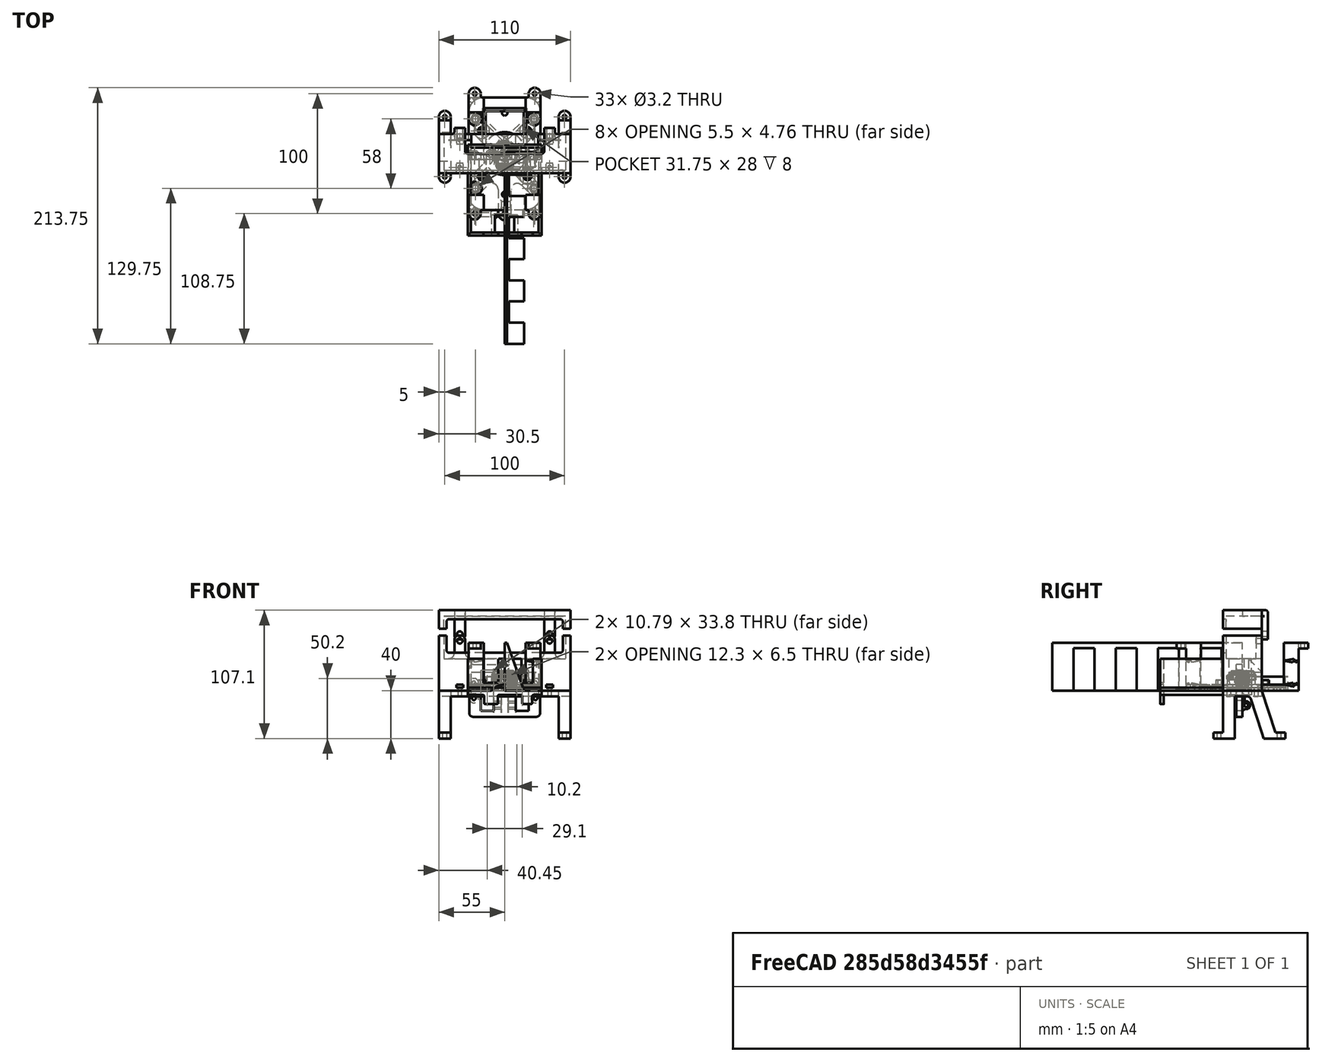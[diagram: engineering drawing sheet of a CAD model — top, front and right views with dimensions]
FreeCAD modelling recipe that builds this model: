
FCSTD DOCUMENT  (FreeCAD 1.0R39109 (Git))
Label: emaxx-kybernetes-mounts
License: All rights reserved
LicenseURL: http://en.wikipedia.org/wiki/All_rights_reserved
objects: Sketcher::SketchObject×61, PartDesign::Pad×32, PartDesign::Pocket×29, PartDesign::Fillet×29, PartDesign::Body×15, App::Part×15, Mesh::Feature×2, Spreadsheet::Sheet×1, PartDesign::SubtractivePrism×1, Part::Feature×1
note: 411 computed .brp shape members not serialized (recipe doc carries the construction recipe); baked Part::Feature solids carry a one-line shape summary decoded from their .brp

FEATURE [Sketcher::SketchObject] Sketch  label="ArduinoBoxOutlineSketch"
  ArcFitTolerance = 0
  AttachmentSupport = -> [XY_Plane001]
  FullyConstrained = true
  MakeInternals = false
  MapMode = 5
  expr: Constraints[0] = <<parameters>>.chassis_hole_diameter
  expr: Constraints[103] = <<parameters>>.margin + <<parameters>>.wall_depth + 0.25 mm
  expr: Constraints[114] = <<parameters>>.esc_width / 2 + <<parameters>>.wall_depth
  expr: Constraints[115] = <<parameters>>.esc_width / 2 + <<parameters>>.wall_depth
  expr: Constraints[121] = <<parameters>>.esc_height + <<parameters>>.wall_depth
  expr: Constraints[1] = <<parameters>>.chassis_hole_diameter
  expr: Constraints[2] = <<parameters>>.chassis_hole_spacing / 2
  expr: Constraints[4] = <<parameters>>.chassis_hole_spacing / 2
  expr: Constraints[5] = <<parameters>>.arduino_width / 2
  expr: Constraints[75] = <<parameters>>.arduino_hole1_offset_x
  expr: Constraints[77] = <<parameters>>.arduino_standoff_diameter
  expr: Constraints[78] = <<parameters>>.arduino_hole1_offset_y
  expr: Constraints[80] = <<parameters>>.arduino_standoff_diameter
  expr: Constraints[81] = <<parameters>>.arduino_standoff_diameter
  expr: Constraints[84] = <<parameters>>.arduino_standoff_diameter
  expr: Constraints[85] = <<parameters>>.arduino_hole3_offset_x
  expr: Constraints[86] = <<parameters>>.arduino_hole3_offset_y
  expr: Constraints[87] = <<parameters>>.arduino_hole4_offset_y
  expr: Constraints[88] = <<parameters>>.arduino_hole4_offset_x
  expr: Constraints[89] = <<parameters>>.arduino_hole2_offset_x
  expr: Constraints[90] = <<parameters>>.arduino_hole2_offset_y
  expr: Constraints[93] = <<parameters>>.arduino_length
  expr: Constraints[94] = <<parameters>>.wall_depth + <<parameters>>.margin + 1.75 mm
  expr: Constraints[96] = <<parameters>>.wall_depth + 5.75 mm / 2 + <<parameters>>.margin
  expr: Constraints[99] = <<parameters>>.wall_depth + 5.75 mm / 2 + <<parameters>>.margin
  sketch-geometry (43):
    g0: Circle CenterX=-25.25 CenterY=0 CenterZ=0 NormalX=0 NormalY=0 NormalZ=1 AngleXU=0 Radius=1.6
    g1: Circle CenterX=25.25 CenterY=0 CenterZ=0 NormalX=0 NormalY=0 NormalZ=1 AngleXU=0 Radius=1.6
    g2: GeomPoint [constr] X=26.67 Y=-65.54 Z=0
    g3: LineSegment StartX=26.88 StartY=-51.57 StartZ=0 EndX=25.505 EndY=-49.1884 EndZ=0
    g4: LineSegment StartX=25.505 StartY=-49.1884 StartZ=0 EndX=22.755 EndY=-49.1884 EndZ=0
    g5: LineSegment StartX=22.755 StartY=-49.1884 StartZ=0 EndX=21.38 EndY=-51.57 EndZ=0
    g6: LineSegment StartX=21.38 StartY=-51.57 StartZ=0 EndX=22.755 EndY=-53.9516 EndZ=0
    g7: LineSegment StartX=22.755 StartY=-53.9516 StartZ=0 EndX=25.505 EndY=-53.9516 EndZ=0
    g8: LineSegment StartX=25.505 StartY=-53.9516 StartZ=0 EndX=26.88 EndY=-51.57 EndZ=0
    g9: Circle [constr] CenterX=24.13 CenterY=-51.57 CenterZ=0 NormalX=0 NormalY=0 NormalZ=1 AngleXU=0 Radius=2.75
    g10: LineSegment StartX=-6.14 StartY=0.5 StartZ=0 EndX=-7.515 EndY=2.88157 EndZ=0
    g11: LineSegment StartX=-7.515 StartY=2.88157 StartZ=0 EndX=-10.265 EndY=2.88157 EndZ=0
    g12: LineSegment StartX=-10.265 StartY=2.88157 StartZ=0 EndX=-11.64 EndY=0.5 EndZ=0
    g13: LineSegment StartX=-11.64 StartY=0.5 StartZ=0 EndX=-10.265 EndY=-1.88157 EndZ=0
    g14: LineSegment StartX=-10.265 StartY=-1.88157 StartZ=0 EndX=-7.515 EndY=-1.88157 EndZ=0
    g15: LineSegment StartX=-7.515 StartY=-1.88157 StartZ=0 EndX=-6.14 EndY=0.5 EndZ=0
    g16: Circle [constr] CenterX=-8.89 CenterY=0.5 CenterZ=0 NormalX=0 NormalY=0 NormalZ=1 AngleXU=0 Radius=2.75
    g17: LineSegment StartX=20.425 StartY=-1.88157 StartZ=0 EndX=21.8 EndY=0.5 EndZ=0
    g18: LineSegment StartX=21.8 StartY=0.5 StartZ=0 EndX=20.425 EndY=2.88157 EndZ=0
    g19: LineSegment StartX=20.425 StartY=2.88157 StartZ=0 EndX=17.675 EndY=2.88157 EndZ=0
    g20: LineSegment StartX=17.675 StartY=2.88157 StartZ=0 EndX=16.3 EndY=0.5 EndZ=0
    g21: LineSegment StartX=16.3 StartY=0.5 StartZ=0 EndX=17.675 EndY=-1.88157 EndZ=0
    g22: LineSegment StartX=17.675 StartY=-1.88157 StartZ=0 EndX=20.425 EndY=-1.88157 EndZ=0
    g23: Circle [constr] CenterX=19.05 CenterY=0.5 CenterZ=0 NormalX=0 NormalY=0 NormalZ=1 AngleXU=0 Radius=2.75
    g24: LineSegment StartX=-22.755 StartY=-52.6816 StartZ=0 EndX=-21.38 EndY=-50.3 EndZ=0
    g25: LineSegment StartX=-21.38 StartY=-50.3 StartZ=0 EndX=-22.755 EndY=-47.9184 EndZ=0
    g26: LineSegment StartX=-22.755 StartY=-47.9184 StartZ=0 EndX=-25.505 EndY=-47.9184 EndZ=0
    g27: LineSegment StartX=-25.505 StartY=-47.9184 StartZ=0 EndX=-26.88 EndY=-50.3 EndZ=0
    g28: LineSegment StartX=-26.88 StartY=-50.3 StartZ=0 EndX=-25.505 EndY=-52.6816 EndZ=0
    g29: LineSegment StartX=-25.505 StartY=-52.6816 StartZ=0 EndX=-22.755 EndY=-52.6816 EndZ=0
    g30: Circle [constr] CenterX=-24.13 CenterY=-50.3 CenterZ=0 NormalX=0 NormalY=0 NormalZ=1 AngleXU=0 Radius=2.75
    g31: GeomPoint [constr] X=26.67 Y=3.04 Z=0
    g32: GeomPoint [constr] X=0 Y=7.49 Z=0
    g33: GeomPoint [constr] X=30.825 Y=0 Z=0
    g34: GeomPoint [constr] X=-30.825 Y=0 Z=0
    g35: LineSegment StartX=-30.825 StartY=-68.49 StartZ=0 EndX=30.825 EndY=-68.49 EndZ=0
    g36: LineSegment StartX=-30.825 StartY=7.49 StartZ=0 EndX=-30.825 EndY=-68.49 EndZ=0
    g37: LineSegment StartX=30.825 StartY=7.49 StartZ=0 EndX=30.825 EndY=-68.49 EndZ=0
    g38: LineSegment StartX=-30.825 StartY=7.49 StartZ=0 EndX=-18.375 EndY=7.49 EndZ=0
    g39: LineSegment StartX=30.825 StartY=7.49 StartZ=0 EndX=18.375 EndY=7.49 EndZ=0
    g40: LineSegment StartX=-18.375 StartY=7.49 StartZ=0 EndX=-18.375 EndY=37.99 EndZ=0
    g41: LineSegment StartX=18.375 StartY=7.49 StartZ=0 EndX=18.375 EndY=37.99 EndZ=0
    g42: LineSegment StartX=-18.375 StartY=37.99 StartZ=0 EndX=18.375 EndY=37.99 EndZ=0
  constraints (108):
    c: Diameter(g1) = 3.2
    c: Diameter(g0) = 3.2
    c: DistanceX(g-1,g1) = 25.25
    c: Horizontal(g0,g-1)
    c: DistanceX(g0,g-1) = 25.25
    c: DistanceX(g-1,g2) = 26.67
    c: Horizontal(g1,g0)
    c: Coincident(g3,g4)
    c: Coincident(g4,g5)
    c: Coincident(g5,g6)
    c: Coincident(g6,g7)
    c: Coincident(g7,g8)
    c: Coincident(g8,g3)
    c: Equal(g3, g4-g8) x5
    c: PointOnObject(g3,g9)
    c: PointOnObject(g4,g9)
    c: PointOnObject(g5,g9)
    c: PointOnObject(g6,g9)
    c: PointOnObject(g7,g9)
    c: PointOnObject(g8,g9)
    c: Coincident(g10,g11)
    c: Coincident(g11,g12)
    c: Coincident(g12,g13)
    c: Coincident(g13,g14)
    c: Coincident(g14,g15)
    c: Coincident(g15,g10)
    c: Equal(g10, g11-g15) x5
    c: PointOnObject(g10,g16)
    c: PointOnObject(g11,g16)
    c: PointOnObject(g12,g16)
    c: PointOnObject(g13,g16)
    c: PointOnObject(g14,g16)
    c: PointOnObject(g15,g16)
    c: Coincident(g17,g18)
    c: Coincident(g18,g19)
    c: Coincident(g19,g20)
    c: Coincident(g20,g21)
    c: Coincident(g21,g22)
    c: Coincident(g22,g17)
    c: Equal(g17, g18-g22) x5
    c: PointOnObject(g17,g23)
    c: PointOnObject(g18,g23)
    c: PointOnObject(g19,g23)
    c: PointOnObject(g20,g23)
    c: PointOnObject(g21,g23)
    c: PointOnObject(g22,g23)
    c: Coincident(g24,g25)
    c: Coincident(g25,g26)
    c: Coincident(g26,g27)
    c: Coincident(g27,g28)
    c: Coincident(g28,g29)
    c: Coincident(g29,g24)
    c: Equal(g24, g25-g29) x5
    c: PointOnObject(g24,g30)
    c: PointOnObject(g25,g30)
    c: PointOnObject(g26,g30)
    c: PointOnObject(g27,g30)
    c: PointOnObject(g28,g30)
    c: PointOnObject(g29,g30)
    c: DistanceX(g9,g2) = 2.54
    c: Horizontal(g4,g3)
    c: Distance(g6,g3) = 5.5
    c: DistanceY(g2,g9) = 13.97
    c: Horizontal(g26,g25)
    c: Distance(g25,g28) = 5.5
    c: Distance(g13,g10) = 5.5
    c: Horizontal(g11,g10)
    c: Horizontal(g19,g18)
    c: Distance(g21,g18) = 5.5
    c: DistanceX(g23,g2) = 7.62
    c: DistanceY(g2,g23) = 66.04
    c: DistanceY(g2,g16) = 66.04
    c: DistanceX(g16,g2) = 35.56
    c: DistanceX(g30,g2) = 50.8
    c: DistanceY(g2,g30) = 15.24
    c: DistanceY(g1,g23) = 0.5
    c: Vertical(g31,g2)
    c: DistanceY(g2,g31) = 68.58
    c: DistanceY(g31,g32) = 4.45
    c: Vertical(g32,g-1)
    c: DistanceX(g1,g33) = 5.575
    c: Horizontal(g33,g1)
    c: Horizontal(g0,g34)
    c: DistanceX(g34,g0) = 5.575
    c: Horizontal(g35)
    c: Vertical(g35,g33)
    c: Vertical(g34,g35)
    c: DistanceY(g35,g2) = 2.95
    c: Vertical(g36)
    c: Vertical(g37)
    c: Coincident(g35,g37)
    c: Coincident(g35,g36)
    c: Horizontal(g37,g36)
    c: Horizontal(g37,g32)
    c: Coincident(g38,g36)
    c: Horizontal(g38)
    c: Coincident(g39,g37)
    c: Horizontal(g39)
    c: DistanceX(g38,g32) = 18.375
    c: DistanceX(g32,g39) = 18.375
    c: Coincident(g40,g38)
    c: Vertical(g40)
    c: Coincident(g41,g39)
    c: Vertical(g41)
    c: Horizontal(g41,g40)
    c: DistanceY(g38,g40) = 30.5
    c: Coincident(g42,g40)
    c: Coincident(g42,g41)
FEATURE [Spreadsheet::Sheet] Spreadsheet  label="parameters"
  cells = A1='margin; B1(margin)==0.2 mm; A2='arduino_length; B2(arduino_length)==68.58 mm; C2==2700 mil; A3='arduino_width; B3(arduino_width)==53.34 mm; C3==2100 mil; A4='arduino_hole_diameter; B4(arduino_hole_diameter)==3.2 mm; C4==125 mil; A5='arduino_hole1_offset_x; B5(arduino_hole1_offset_x)==2.54 mm; C5==100 mil; A6='arduino_hole1_offset_y; B6(arduino_hole1_offset_y)==13.97 mm; C6==550 mil; A7='arduino_hole2_offset_x; B7(arduino_hole2_offset_x)==50.8 mm; C7==2000 mil; A8='arduino_hole2_offset_y; B8(arduino_hole2_offset_y)==15.24 mm; C8==600 mil; A9='arduino_hole3_offset_x; B9(arduino_hole3_offset_x)==7.62 mm; C9==300 mil; A10='arduino_hole3_offset_y; B10(arduino_hole3_offset_y)==66.04 mm; C10==2600 mil; A11='arduino_hole4_offset_x; B11(arduino_hole4_offset_x)==35.56 mm; C11==1400 mil; A12='arduino_hole4_offset_y; B12(arduino_hole4_offset_y)==66.04 mm; C12==2600 mil; A13='chassis_hole_spacing; B13(chassis_hole_spacing)==50.5 mm; A14='chassis_hole_diameter; B14(chassis_hole_diameter)==3.2 mm; A15='wall_depth; B15(wall_depth)==2.5 mm; A16='arduino_standoff_diameter; B16(arduino_standoff_diameter)==C16 + 0.5 mm; C16==5 mm; A17='esc_width; B17(esc_width)==31.75 mm; A18='esc_height; B18(esc_height)==28 mm; A19='arduino_usb_offsetx_start; B19(arduino_usb_offsetx_start)==C19 - 0.5 mm; C19==1275 mil; A20='arduino_usb_offsetx_end; B20(arduino_usb_offsetx_end)==C20 + 0.5 mm; C20==1725 mil; A21='arduino_power_offsetx_start; B21(arduino_power_offsetx_start)==C21; C21==125 mil; A22='arduino_power_offsetx_end; B22(arduino_power_offsetx_end)==C22 + 0.5 mm; C22==475 mil; C23==75 mil; A24='transmission_bump_depth; B24(transmission_bump_depth)==17.25 mm; A25='nub_hole_diameter; B25(nub_hole_diameter)==C25 + 0.5 mm; C25==6.5 mm; A27='gps_hole_spacing_x; B27(gps_hole_spacing_x)==1.5 in; A28='gps_hole_spacing_y; B28(gps_hole_spacing_y)==1.5 in; A29='gps_bolt_diameter; B29(gps_bolt_diameter)==3.2 mm; A30='gps_nut_offset; B30(gps_nut_offset)==plate_nut_diameter / sqrt(2); A31='plate_bolt_diameter; B31(plate_bolt_diameter)==3.2 mm; A32='plate_hole_spacing; B32(plate_hole_spacing)==5 cm; A33='plate_nut_diameter; B33(plate_nut_diameter)==6.5 mm; A35='rpi_hole_spacing_x; B35(rpi_hole_spacing_x)==49 mm; A36='rpi_hole_spacing_y; B36(rpi_hole_spacing_y)==58 mm; A37='rpi_standoff_diameter; B37(rpi_standoff_diameter)==C16 + 0.5 mm; A38='rpi_standoff_offset; B38(rpi_standoff_offset)==rpi_standoff_diameter / sqrt(2); A40='gps_wrap_margin; B40(gps_wrap_margin)==3 mm; A41='gps_antenna_bolt_diameter; B41(gps_antenna_bolt_diameter)==4.5 mm; A42='gps_antenna_hole_spacing; B42(gps_antenna_hole_spacing)==68 mm; A43='gps_wrap_post_size; B43(gps_wrap_post_size)==12.5 mm; A44='gps_wrap_width; B44(gps_wrap_width)==60 mm; A46='camera_mount_width; B46(camera_mount_width)==110 mm; A47='camera_mount_depth; B47(camera_mount_depth)==32.6 mm; A48='camera_mount_height; B48(camera_mount_height)==46 mm; A49='camera_bolt_diameter; B49(camera_bolt_diameter)==4.5 mm; A50='camera_height; B50(camera_height)==29.7 mm; A51='camera_width; B51(camera_width)==97 mm; A52='camera_hole_spacing; B52(camera_hole_spacing)==75 mm; A53='camera_attachment_thickness; B53(camera_attachment_thickness)==5 mm; A54='camera_depth; B54(camera_depth)==25.1 mm; A55='camera_usbc_offsetx_start; B55(camera_usbc_offsetx_start)==22.1 mm; A56='camera_usbc_offsetx_end; B56(camera_usbc_offsetx_end)==47.8 mm; A57='camera_usbc_depth; B57(camera_usbc_depth)==12.8 mm; A59='bumper_hole_spacing_x; B59(bumper_hole_spacing_x)==48.25 mm + 3.2 mm; A60='bumper_hole_spacing_y; B60(bumper_hole_spacing_y)==9.5 mm + 3.2 mm; A61='bumper_thickness; B61(bumper_thickness)==5 mm; A62='bumper_width; B62(bumper_width)==bumper_hole_spacing_x + bumper_hole_keepout; A63='bumper_height; B63(bumper_height)==bumper_switch_hole_spacing + bumper_bolt_diameter * 2 + 13 mm; A64='bumper_nub_height; B64(bumper_nub_height)==2 mm; A65='bumper_nub_fillet_radius; B65(bumper_nub_fillet_radius)==3.375 mm; A66='bumper_bolt_diameter; B66(bumper_bolt_diameter)==3.2 mm; A67='bumper_switch_hole_spacing; B67(bumper_switch_hole_spacing)==27.6 mm - 3.2 mm; A68='bumper_hole_keepout; B68(bumper_hole_keepout)==7.75 mm
FEATURE [PartDesign::Pad] Pad  label="ArduinoBoxOutline"
  Direction = (0,0,1)
  Length = 26.7
  Length2 = 10
  Profile = -> Sketch
  ReferenceAxis = -> Sketch [N_Axis]
  Suppressed = false
  Type = 0
FEATURE [Sketcher::SketchObject] Sketch001  label="ArduinoBoxCutoutSketch"
  ArcFitTolerance = 0
  AttachmentSupport = -> [Pad]
  FullyConstrained = true
  MakeInternals = false
  MapMode = 5
  Placement = pos=(0,0,26.7) rot=(0,0,1;0rad)
  expr: Constraints[11] = <<parameters>>.margin
  expr: Constraints[14] = <<parameters>>.margin + 1.75 mm
  expr: Constraints[19] = <<parameters>>.wall_depth
  expr: Constraints[20] = <<parameters>>.wall_depth
  expr: Constraints[2] = <<parameters>>.chassis_hole_spacing / 2 + <<parameters>>.wall_depth + 5.75 mm / 2 + <<parameters>>.margin
  expr: Constraints[30] = <<parameters>>.wall_depth
  expr: Constraints[31] = <<parameters>>.esc_height
  expr: Constraints[32] = <<parameters>>.esc_width
  expr: Constraints[33] = <<parameters>>.esc_width / 2
  expr: Constraints[3] = <<parameters>>.chassis_hole_spacing / 2 + <<parameters>>.wall_depth + 5.75 mm / 2 + <<parameters>>.margin
  expr: Constraints[5] = <<parameters>>.arduino_width / 2
  expr: Constraints[6] = <<parameters>>.arduino_hole3_offset_x
  expr: Constraints[7] = <<parameters>>.arduino_hole3_offset_y
  expr: Constraints[9] = <<parameters>>.arduino_length
  sketch-geometry (13):
    g0: GeomPoint [constr] X=30.825 Y=0 Z=0
    g1: GeomPoint [constr] X=-30.825 Y=0 Z=0
    g2: GeomPoint [constr] X=19.05 Y=0.5 Z=0
    g3: GeomPoint [constr] X=26.67 Y=-65.54 Z=0
    g4: GeomPoint [constr] X=26.67 Y=3.04 Z=0
    g5: LineSegment StartX=-28.325 StartY=-65.74 StartZ=0 EndX=28.325 EndY=-65.74 EndZ=0
    g6: LineSegment StartX=28.325 StartY=4.99 StartZ=0 EndX=28.325 EndY=-65.74 EndZ=0
    g7: LineSegment StartX=28.325 StartY=4.99 StartZ=0 EndX=-28.325 EndY=4.99 EndZ=0
    g8: LineSegment StartX=-28.325 StartY=4.99 StartZ=0 EndX=-28.325 EndY=-65.74 EndZ=0
    g9: LineSegment StartX=-15.875 StartY=35.49 StartZ=0 EndX=15.875 EndY=35.49 EndZ=0
    g10: LineSegment StartX=15.875 StartY=35.49 StartZ=0 EndX=15.875 EndY=7.49 EndZ=0
    g11: LineSegment StartX=15.875 StartY=7.49 StartZ=0 EndX=-15.875 EndY=7.49 EndZ=0
    g12: LineSegment StartX=-15.875 StartY=7.49 StartZ=0 EndX=-15.875 EndY=35.49 EndZ=0
  constraints (34):
    c: Horizontal(g1,g-1)
    c: Horizontal(g-1,g0)
    c: DistanceX(g1,g-1) = 30.825
    c: DistanceX(g-1,g0) = 30.825
    c: DistanceY(g0,g2) = 0.5
    c: DistanceX(g-1,g3) = 26.67
    c: DistanceX(g2,g3) = 7.62
    c: DistanceY(g3,g2) = 66.04
    c: Vertical(g4,g3)
    c: DistanceY(g3,g4) = 68.58
    c: Horizontal(g5)
    c: DistanceY(g5,g3) = 0.2
    c: Vertical(g6)
    c: Coincident(g6,g5)
    c: DistanceY(g4,g6) = 1.95
    c: Horizontal(g7)
    c: Vertical(g7,g5)
    c: Coincident(g8,g7)
    c: Coincident(g8,g5)
    c: DistanceX(g6,g0) = 2.5
    c: DistanceX(g1,g7) = 2.5
    c: Coincident(g7,g6)
    c: Coincident(g9,g10)
    c: Coincident(g10,g11)
    c: Coincident(g11,g12)
    c: Coincident(g12,g9)
    c: Horizontal(g9)
    c: Horizontal(g11)
    c: Vertical(g10)
    c: Vertical(g12)
    c: DistanceY(g6,g10) = 2.5
    c: DistanceY(g10,g9) = 28
    c: DistanceX(g9,g9) = 31.75
    c: DistanceX(g-1,g10) = 15.875
FEATURE [PartDesign::Pocket] Pocket  label="ArduinoBoxCutout"
  BaseFeature = -> Pad
  Direction = (0,0,-1)
  Length = 24.2
  Length2 = 5
  Profile = -> Sketch001
  ReferenceAxis = -> Sketch001 [N_Axis]
  Suppressed = false
  Type = 0
FEATURE [Sketcher::SketchObject] Sketch002  label="ArduinoBoxCutoutESCSketch"
  ArcFitTolerance = 0
  AttachmentSupport = -> [Pocket]
  FullyConstrained = true
  MakeInternals = false
  MapMode = 5
  Placement = pos=(0,0,26.7) rot=(0,0,1;0rad)
  expr: Constraints[16] = <<parameters>>.esc_width / 2 + <<parameters>>.wall_depth
  expr: Constraints[17] = <<parameters>>.esc_width / 2 + <<parameters>>.wall_depth
  expr: Constraints[19] = <<parameters>>.esc_height + <<parameters>>.wall_depth
  expr: Constraints[1] = <<parameters>>.arduino_width / 2
  expr: Constraints[2] = <<parameters>>.arduino_hole3_offset_y
  expr: Constraints[4] = <<parameters>>.arduino_hole3_offset_x
  expr: Constraints[6] = <<parameters>>.arduino_length
  expr: Constraints[7] = <<parameters>>.wall_depth + <<parameters>>.margin + 1.75 mm
  sketch-geometry (8):
    g0: GeomPoint [constr] X=0 Y=7.49 Z=0
    g1: GeomPoint [constr] X=19.05 Y=0.5 Z=0
    g2: GeomPoint [constr] X=26.67 Y=-65.54 Z=0
    g3: GeomPoint [constr] X=26.67 Y=3.04 Z=0
    g4: LineSegment StartX=-18.375 StartY=37.99 StartZ=0 EndX=18.375 EndY=37.99 EndZ=0
    g5: LineSegment StartX=18.375 StartY=37.99 StartZ=0 EndX=18.375 EndY=7.49 EndZ=0
    g6: LineSegment StartX=18.375 StartY=7.49 StartZ=0 EndX=-18.375 EndY=7.49 EndZ=0
    g7: LineSegment StartX=-18.375 StartY=7.49 StartZ=0 EndX=-18.375 EndY=37.99 EndZ=0
  constraints (20):
    c: PointOnObject(g0,g-2)
    c: DistanceX(g-1,g2) = 26.67
    c: DistanceY(g2,g1) = 66.04
    c: DistanceY(g-1,g1) = 0.5
    c: DistanceX(g1,g2) = 7.62
    c: Vertical(g3,g2)
    c: DistanceY(g2,g3) = 68.58
    c: DistanceY(g3,g0) = 4.45
    c: Coincident(g4,g5)
    c: Coincident(g5,g6)
    c: Coincident(g6,g7)
    c: Coincident(g7,g4)
    c: Horizontal(g4)
    c: Horizontal(g6)
    c: Vertical(g5)
    c: Vertical(g7)
    c: DistanceX(g0,g5) = 18.375
    c: DistanceX(g6,g0) = 18.375
    c: Horizontal(g0,g5)
    c: DistanceY(g5,g4) = 30.5
FEATURE [PartDesign::Pocket] Pocket001  label="ArduinoBoxCutoutESC"
  BaseFeature = -> Pocket
  Direction = (0,0,-1)
  Length = 15.2
  Length2 = 5
  Profile = -> Sketch002
  ReferenceAxis = -> Sketch002 [N_Axis]
  Suppressed = false
  Type = 0
  expr: Length = 26.7 - 9 - 2.5
FEATURE [Sketcher::SketchObject] Sketch003  label="ArduinoBoxCutoutConnectorsSketch"
  ArcFitTolerance = 0
  AttachmentSupport = -> [Pocket001]
  FullyConstrained = true
  MakeInternals = false
  MapMode = 5
  Placement = pos=(0,0,26.7) rot=(0,0,1;0rad)
  expr: Constraints[0] = <<parameters>>.arduino_width / 2
  expr: Constraints[12] = <<parameters>>.arduino_usb_offsetx_start
  expr: Constraints[13] = <<parameters>>.arduino_usb_offsetx_end
  expr: Constraints[15] = <<parameters>>.margin + <<parameters>>.wall_depth + 0.25 mm
  expr: Constraints[1] = <<parameters>>.arduino_hole3_offset_y
  expr: Constraints[26] = <<parameters>>.arduino_power_offsetx_start
  expr: Constraints[27] = <<parameters>>.arduino_power_offsetx_end
  expr: Constraints[2] = <<parameters>>.arduino_hole3_offset_x
  sketch-geometry (10):
    g0: GeomPoint [constr] X=26.67 Y=-65.54 Z=0
    g1: GeomPoint [constr] X=19.05 Y=0.5 Z=0
    g2: LineSegment StartX=-17.645 StartY=-65.54 StartZ=0 EndX=-5.215 EndY=-65.54 EndZ=0
    g3: LineSegment StartX=-5.215 StartY=-65.54 StartZ=0 EndX=-5.215 EndY=-68.49 EndZ=0
    g4: LineSegment StartX=-5.215 StartY=-68.49 StartZ=0 EndX=-17.645 EndY=-68.49 EndZ=0
    g5: LineSegment StartX=-17.645 StartY=-68.49 StartZ=0 EndX=-17.645 EndY=-65.54 EndZ=0
    g6: LineSegment StartX=14.105 StartY=-65.54 StartZ=0 EndX=23.495 EndY=-65.54 EndZ=0
    g7: LineSegment StartX=23.495 StartY=-65.54 StartZ=0 EndX=23.495 EndY=-68.49 EndZ=0
    g8: LineSegment StartX=23.495 StartY=-68.49 StartZ=0 EndX=14.105 EndY=-68.49 EndZ=0
    g9: LineSegment StartX=14.105 StartY=-68.49 StartZ=0 EndX=14.105 EndY=-65.54 EndZ=0
  constraints (28):
    c: DistanceX(g-1,g0) = 26.67
    c: DistanceY(g0,g1) = 66.04
    c: DistanceX(g1,g0) = 7.62
    c: DistanceY(g-1,g1) = 0.5
    c: Coincident(g2,g3)
    c: Coincident(g3,g4)
    c: Coincident(g4,g5)
    c: Coincident(g5,g2)
    c: Horizontal(g2)
    c: Horizontal(g4)
    c: Vertical(g3)
    c: Vertical(g5)
    c: DistanceX(g3,g0) = 31.885
    c: DistanceX(g4,g0) = 44.315
    c: Horizontal(g2,g0)
    c: DistanceY(g4,g2) = 2.95
    c: Coincident(g6,g7)
    c: Coincident(g7,g8)
    c: Coincident(g8,g9)
    c: Coincident(g9,g6)
    c: Horizontal(g6)
    c: Horizontal(g8)
    c: Vertical(g7)
    c: Vertical(g9)
    c: Horizontal(g6,g0)
    c: Horizontal(g8,g3)
    c: DistanceX(g6,g0) = 3.175
    c: DistanceX(g6,g0) = 12.565
FEATURE [PartDesign::Pocket] Pocket002  label="ArduinoBoxCutoutConnectors"
  BaseFeature = -> Pocket001
  Direction = (0,0,-1)
  Length = 20.2
  Length2 = 5
  Profile = -> Sketch003
  ReferenceAxis = -> Sketch003 [N_Axis]
  Suppressed = false
  Type = 0
  expr: Length = 26.7 mm - 5 mm - 1.5 mm
FEATURE [Sketcher::SketchObject] Sketch004  label="ArduinoBoxCutoutTransmissionBumpSketch"
  ArcFitTolerance = 0
  AttachmentSupport = -> [Pocket002]
  FullyConstrained = true
  MakeInternals = false
  MapMode = 5
  Placement = pos=(0,-68.49,0) rot=(1,0,0;1.5708rad)
  sketch-geometry (4):
    g0: GeomPoint [constr] X=-11 Y=0 Z=0
    g1: GeomPoint [constr] X=11 Y=0 Z=0
    g2: GeomPoint [constr] X=0 Y=5 Z=0
    g3: Circle CenterX=0 CenterY=-9.5 CenterZ=0 NormalX=0 NormalY=0 NormalZ=1 AngleXU=0 Radius=14.5
  constraints (9):
    c: PointOnObject(g2,g-2)
    c: DistanceY(g-1,g2) = 5
    c: Horizontal(g0,g-1)
    c: DistanceX(g0,g-1) = 11
    c: DistanceX(g-1,g1) = 11
    c: Horizontal(g1,g-1)
    c: Vertical(g3,g-1)
    c: DistanceY(g3,g-1) = 9.5
    c: Diameter(g3) = 29
FEATURE [PartDesign::Pocket] Pocket003  label="ArduinoBoxCutoutTransmissionBump"
  BaseFeature = -> Pocket002
  Direction = (0,1,-2e-16)
  Length = 17.25
  Length2 = 5
  Profile = -> Sketch004
  ReferenceAxis = -> Sketch004 [N_Axis]
  Suppressed = false
  Type = 0
  expr: Length = <<parameters>>.transmission_bump_depth
FEATURE [Sketcher::SketchObject] Sketch005  label="ArduinoBoxCutoutNubsSketch"
  ArcFitTolerance = 0
  AttachmentSupport = -> [Pocket003]
  FullyConstrained = true
  MakeInternals = false
  MapMode = 5
  Placement = pos=(0,0,2.5) rot=(0,0,1;0rad)
  expr: Constraints[1] = <<parameters>>.chassis_hole_spacing / 2
  expr: Constraints[2] = <<parameters>>.nub_hole_diameter
  expr: Constraints[5] = <<parameters>>.nub_hole_diameter
  expr: Constraints[6] = <<parameters>>.chassis_hole_spacing / 2
  sketch-geometry (3):
    g0: GeomPoint [constr] X=25.25 Y=0 Z=0
    g1: Circle CenterX=25.25 CenterY=-22 CenterZ=0 NormalX=0 NormalY=0 NormalZ=1 AngleXU=0 Radius=3.5
    g2: Circle CenterX=-25.25 CenterY=-22 CenterZ=0 NormalX=0 NormalY=0 NormalZ=1 AngleXU=0 Radius=3.5
  constraints (8):
    c: Horizontal(g0,g-1)
    c: DistanceX(g-1,g0) = 25.25
    c: Diameter(g1) = 7
    c: Vertical(g0,g1)
    c: DistanceY(g1,g0) = 22
    c: Diameter(g2) = 7
    c: DistanceX(g2,g-1) = 25.25
    c: Horizontal(g2,g1)
FEATURE [PartDesign::Pocket] Pocket004  label="ArduinoBoxCutoutNubs"
  BaseFeature = -> Pocket003
  Direction = (0,0,-1)
  Length = 2.5
  Length2 = 5
  Profile = -> Sketch005
  ReferenceAxis = -> Sketch005 [N_Axis]
  Suppressed = false
  Type = 0
FEATURE [PartDesign::Fillet] Fillet  label="ArduinoBoxInsertSmoothing1"
  Base = -> Pocket004 [Edge175,Edge176,Edge177,Edge71,Edge79,Edge77,Edge65]
  BaseFeature = -> Pocket004
  Radius = 1
  SupportTransform = false
  Suppressed = false
  UseAllEdges = false
FEATURE [PartDesign::Fillet] Fillet001  label="ArduinoBoxInsertSmoothing2"
  Base = -> Fillet [Edge27,Edge29,Edge88,Edge23,Edge21,Edge25]
  BaseFeature = -> Fillet
  Radius = 1
  SupportTransform = false
  Suppressed = false
  UseAllEdges = false
FEATURE [PartDesign::Body] Body  label="ArduinoBoxBody"
  AllowCompound = false
  Group = -> [Sketch,Pad,Sketch001,Pocket,Sketch002,Pocket001,Sketch003,Pocket002,Sketch004,Pocket003,Sketch005,Pocket004,Fillet,Fillet001]
  Origin = -> Origin001
  Tip = -> Fillet001
FEATURE [App::Part] Part  label="ArduinoBox"
  Group = -> [Body]
  Origin = -> Origin
FEATURE [Sketcher::SketchObject] Sketch007  label="TransmissionCoverHullSketch"
  ArcFitTolerance = 0
  AttachmentSupport = -> [XY_Plane005]
  FullyConstrained = true
  MakeInternals = false
  MapMode = 5
  sketch-geometry (3):
    g0: Circle CenterX=0 CenterY=0 CenterZ=0 NormalX=0 NormalY=0 NormalZ=1 AngleXU=0 Radius=17.9
    g1: Circle CenterX=-12.5 CenterY=0 CenterZ=0 NormalX=0 NormalY=0 NormalZ=1 AngleXU=0 Radius=1.6
    g2: Circle CenterX=12.5 CenterY=0 CenterZ=0 NormalX=0 NormalY=0 NormalZ=1 AngleXU=0 Radius=1.6
  constraints (8):
    c: Coincident(g0,g-1)
    c: Diameter(g0) = 35.8
    c: PointOnObject(g1,g-1)
    c: PointOnObject(g2,g-1)
    c: Diameter(g1) = 3.2
    c: Diameter(g2) = 3.2
    c: DistanceX(g0,g2) = 12.5
    c: DistanceX(g1,g0) = 12.5
FEATURE [PartDesign::Pad] Pad002  label="TransmissionCoverHull"
  Direction = (0,0,1)
  Length = 5
  Length2 = 10
  Profile = -> Sketch007
  ReferenceAxis = -> Sketch007 [N_Axis]
  Suppressed = false
  Type = 0
FEATURE [Sketcher::SketchObject] Sketch008  label="TransmissionCoverNutCatchesSketch"
  ArcFitTolerance = 0
  AttachmentSupport = -> [Pad002]
  FullyConstrained = true
  MakeInternals = false
  MapMode = 5
  Placement = pos=(0,0,5) rot=(0,0,1;0rad)
  sketch-geometry (14):
    g0: LineSegment StartX=15.3146 StartY=1.625 StartZ=0 EndX=12.5 EndY=3.25 EndZ=0
    g1: LineSegment StartX=12.5 StartY=3.25 StartZ=0 EndX=9.68542 EndY=1.625 EndZ=0
    g2: LineSegment StartX=9.68542 StartY=1.625 StartZ=0 EndX=9.68542 EndY=-1.625 EndZ=0
    g3: LineSegment StartX=9.68542 StartY=-1.625 StartZ=0 EndX=12.5 EndY=-3.25 EndZ=0
    g4: LineSegment StartX=12.5 StartY=-3.25 StartZ=0 EndX=15.3146 EndY=-1.625 EndZ=0
    g5: LineSegment StartX=15.3146 StartY=-1.625 StartZ=0 EndX=15.3146 EndY=1.625 EndZ=0
    g6: Circle [constr] CenterX=12.5 CenterY=0 CenterZ=0 NormalX=0 NormalY=0 NormalZ=1 AngleXU=0 Radius=3.25
    g7: LineSegment StartX=-12.5 StartY=3.25 StartZ=0 EndX=-15.3146 EndY=1.625 EndZ=0
    g8: LineSegment StartX=-15.3146 StartY=1.625 StartZ=0 EndX=-15.3146 EndY=-1.625 EndZ=0
    g9: LineSegment StartX=-15.3146 StartY=-1.625 StartZ=0 EndX=-12.5 EndY=-3.25 EndZ=0
    g10: LineSegment StartX=-12.5 StartY=-3.25 StartZ=0 EndX=-9.68542 EndY=-1.625 EndZ=0
    g11: LineSegment StartX=-9.68542 StartY=-1.625 StartZ=0 EndX=-9.68542 EndY=1.625 EndZ=0
    g12: LineSegment StartX=-9.68542 StartY=1.625 StartZ=0 EndX=-12.5 EndY=3.25 EndZ=0
    g13: Circle [constr] CenterX=-12.5 CenterY=0 CenterZ=0 NormalX=0 NormalY=0 NormalZ=1 AngleXU=0 Radius=3.25
  constraints (34):
    c: Coincident(g0,g1)
    c: Coincident(g1,g2)
    c: Coincident(g2,g3)
    c: Coincident(g3,g4)
    c: Coincident(g4,g5)
    c: Coincident(g5,g0)
    c: Equal(g0, g1-g5) x5
    c: PointOnObject(g0,g6)
    c: PointOnObject(g1,g6)
    c: PointOnObject(g2,g6)
    c: PointOnObject(g3,g6)
    c: PointOnObject(g4,g6)
    c: PointOnObject(g5,g6)
    c: PointOnObject(g6,g-1)
    c: Coincident(g7,g8)
    c: Coincident(g8,g9)
    c: Coincident(g9,g10)
    c: Coincident(g10,g11)
    c: Coincident(g11,g12)
    c: Coincident(g12,g7)
    c: Equal(g7, g8-g12) x5
    c: PointOnObject(g7,g13)
    c: PointOnObject(g8,g13)
    c: PointOnObject(g9,g13)
    c: PointOnObject(g10,g13)
    c: PointOnObject(g11,g13)
    c: PointOnObject(g12,g13)
    c: PointOnObject(g13,g-1)
    c: DistanceX(g-1,g6) = 12.5
    c: DistanceX(g13,g-1) = 12.5
    c: Horizontal(g7,g11)
    c: Horizontal(g1,g0)
    c: DistanceY(g9,g7) = 6.5
    c: DistanceY(g3,g0) = 6.5
FEATURE [PartDesign::Pocket] Pocket005  label="TransmissionCoverNutCatches"
  BaseFeature = -> Pad002
  Direction = (0,0,-1)
  Length = 2
  Length2 = 5
  Profile = -> Sketch008
  ReferenceAxis = -> Sketch008 [N_Axis]
  Suppressed = false
  Type = 0
FEATURE [PartDesign::Body] Body002  label="TransmissionCoverBody"
  AllowCompound = false
  Group = -> [Sketch007,Pad002,Sketch008,Pocket005]
  Origin = -> Origin005
  Tip = -> Pocket005
FEATURE [Sketcher::SketchObject] Sketch009  label="GPSMountBaseSketch"
  ArcFitTolerance = 0
  AttachmentSupport = -> [XY_Plane007]
  FullyConstrained = true
  MakeInternals = false
  MapMode = 5
  expr: Constraints[0] = <<parameters>>.gps_bolt_diameter
  expr: Constraints[10] = <<parameters>>.gps_hole_spacing_x / 2
  expr: Constraints[11] = <<parameters>>.gps_hole_spacing_y / 2
  expr: Constraints[12] = <<parameters>>.gps_nut_offset
  expr: Constraints[13] = <<parameters>>.gps_nut_offset
  expr: Constraints[14] = <<parameters>>.gps_nut_offset
  expr: Constraints[1] = <<parameters>>.gps_bolt_diameter
  expr: Constraints[22] = -(<<parameters>>.gps_hole_spacing_x / 2 - <<parameters>>.gps_nut_offset) + <<parameters>>.gps_hole_spacing_y / 2 + <<parameters>>.gps_nut_offset
  expr: Constraints[23] = -(<<parameters>>.gps_hole_spacing_x / 2 - <<parameters>>.gps_nut_offset) + <<parameters>>.gps_hole_spacing_y / 2 + <<parameters>>.gps_nut_offset
  expr: Constraints[24] = <<parameters>>.gps_nut_offset
  expr: Constraints[25] = <<parameters>>.gps_nut_offset
  expr: Constraints[2] = <<parameters>>.gps_bolt_diameter
  expr: Constraints[31] = <<parameters>>.gps_nut_offset
  expr: Constraints[3] = <<parameters>>.gps_bolt_diameter
  expr: Constraints[4] = <<parameters>>.gps_hole_spacing_x
  expr: Constraints[54] = -(<<parameters>>.gps_hole_spacing_x / 2 - <<parameters>>.gps_nut_offset) + <<parameters>>.gps_hole_spacing_y / 2 + <<parameters>>.gps_nut_offset
  expr: Constraints[55] = -(<<parameters>>.gps_hole_spacing_x / 2 - <<parameters>>.gps_nut_offset) + <<parameters>>.gps_hole_spacing_y / 2 + <<parameters>>.gps_nut_offset
  expr: Constraints[5] = <<parameters>>.gps_hole_spacing_y
  sketch-geometry (24):
    g0: Circle CenterX=19.05 CenterY=19.05 CenterZ=0 NormalX=0 NormalY=0 NormalZ=1 AngleXU=0 Radius=1.6
    g1: Circle CenterX=-19.05 CenterY=19.05 CenterZ=0 NormalX=0 NormalY=0 NormalZ=1 AngleXU=0 Radius=1.6
    g2: Circle CenterX=-19.05 CenterY=-19.05 CenterZ=0 NormalX=0 NormalY=0 NormalZ=1 AngleXU=0 Radius=1.6
    g3: Circle CenterX=19.05 CenterY=-19.05 CenterZ=0 NormalX=0 NormalY=0 NormalZ=1 AngleXU=0 Radius=1.6
    g4: GeomPoint [constr] X=-23.6462 Y=14.4538 Z=0
    g5: GeomPoint [constr] X=-23.6462 Y=-14.4538 Z=0
    g6: GeomPoint [constr] X=-14.4538 Y=-23.6462 Z=0
    g7: GeomPoint [constr] X=14.4538 Y=-23.6462 Z=0
    g8: GeomPoint [constr] X=23.6462 Y=-14.4538 Z=0
    g9: GeomPoint [constr] X=14.4538 Y=23.6462 Z=0
    g10: GeomPoint [constr] X=23.6462 Y=14.4538 Z=0
    g11: ArcOfCircle CenterX=19.05 CenterY=19.05 CenterZ=0 NormalX=0 NormalY=0 NormalZ=1 AngleXU=0 Radius=6.5 StartAngle=5.49779 EndAngle=8.63938
    g12: LineSegment StartX=14.4538 StartY=23.6462 StartZ=0 EndX=8.9e-15 EndY=9.19239 EndZ=0
    g13: LineSegment StartX=23.6462 StartY=14.4538 StartZ=0 EndX=9.19239 EndY=-3.6e-15 EndZ=0
    g14: GeomPoint [constr] X=-14.4538 Y=23.6462 Z=0
    g15: ArcOfCircle CenterX=19.05 CenterY=-19.05 CenterZ=0 NormalX=0 NormalY=0 NormalZ=1 AngleXU=0 Radius=6.5 StartAngle=3.92699 EndAngle=7.06858
    g16: ArcOfCircle CenterX=-19.05 CenterY=19.05 CenterZ=0 NormalX=0 NormalY=0 NormalZ=1 AngleXU=0 Radius=6.5 StartAngle=0.785398 EndAngle=3.92699
    g17: ArcOfCircle CenterX=-19.05 CenterY=-19.05 CenterZ=0 NormalX=0 NormalY=0 NormalZ=1 AngleXU=0 Radius=6.5 StartAngle=2.35619 EndAngle=5.49779
    g18: LineSegment StartX=23.6462 StartY=-14.4538 StartZ=0 EndX=9.19239 EndY=-3.6e-15 EndZ=0
    g19: LineSegment StartX=14.4538 StartY=-23.6462 StartZ=0 EndX=-3.6e-15 EndY=-9.19239 EndZ=0
    g20: LineSegment StartX=-14.4538 StartY=-23.6462 StartZ=0 EndX=-3.6e-15 EndY=-9.19239 EndZ=0
    g21: LineSegment StartX=-23.6462 StartY=-14.4538 StartZ=0 EndX=-9.19239 EndY=0 EndZ=0
    g22: LineSegment StartX=-9.19239 StartY=0 StartZ=0 EndX=-23.6462 EndY=14.4538 EndZ=0
    g23: LineSegment StartX=-14.4538 StartY=23.6462 StartZ=0 EndX=8.9e-15 EndY=9.19239 EndZ=0
  constraints (56):
    c: Diameter(g1) = 3.2
    c: Diameter(g0) = 3.2
    c: Diameter(g3) = 3.2
    c: Diameter(g2) = 3.2
    c: DistanceX(g1,g0) = 38.1
    c: DistanceY(g3,g0) = 38.1
    c: Horizontal(g3,g2)
    c: Horizontal(g1,g0)
    c: Vertical(g0,g3)
    c: Vertical(g1,g2)
    c: DistanceX(g1,g-1) = 19.05
    c: DistanceY(g-1,g1) = 19.05
    c: DistanceX(g9,g0) = 4.59619
    c: DistanceY(g0,g9) = 4.59619
    c: DistanceX(g0,g10) = 4.59619
    c: Coincident(g11,g0)
    c: Coincident(g11,g9)
    c: Coincident(g11,g10)
    c: Coincident(g12,g11)
    c: PointOnObject(g12,g-2)
    c: Coincident(g13,g11)
    c: PointOnObject(g13,g-1)
    c: DistanceY(g-1,g12) = 9.19239
    c: DistanceX(g-1,g13) = 9.19239
    c: DistanceY(g3,g8) = 4.59619
    c: DistanceY(g7,g3) = 4.59619
    c: Coincident(g15,g3)
    c: Coincident(g15,g7)
    c: Coincident(g15,g8)
    c: Vertical(g15,g11)
    c: Horizontal(g14,g11)
    c: DistanceX(g1,g14) = 4.59619
    c: Horizontal(g11,g4)
    c: Coincident(g16,g1)
    c: Coincident(g16,g14)
    c: Coincident(g16,g4)
    c: Horizontal(g6,g15)
    c: Vertical(g6,g16)
    c: Vertical(g5,g16)
    c: Coincident(g17,g2)
    c: Coincident(g17,g5)
    c: Coincident(g17,g6)
    c: Coincident(g18,g15)
    c: Coincident(g18,g13)
    c: Coincident(g19,g15)
    c: PointOnObject(g19,g-2)
    c: Coincident(g20,g17)
    c: Coincident(g20,g19)
    c: Coincident(g21,g17)
    c: PointOnObject(g21,g-1)
    c: Coincident(g22,g21)
    c: Coincident(g22,g16)
    c: Coincident(g23,g16)
    c: Coincident(g23,g12)
    c: DistanceX(g21,g-1) = 9.19239
    c: DistanceY(g19,g-1) = 9.19239
FEATURE [PartDesign::Pad] Pad003  label="GPSMountBase"
  Direction = (0,0,1)
  Length = 2.5
  Length2 = 10
  Profile = -> Sketch009
  ReferenceAxis = -> Sketch009 [N_Axis]
  Suppressed = false
  Type = 0
FEATURE [Sketcher::SketchObject] Sketch010  label="GPSMountPlateMountSketch"
  ArcFitTolerance = 0
  AttachmentSupport = -> [XY_Plane007]
  FullyConstrained = true
  MakeInternals = false
  MapMode = 5
  expr: Constraints[13] = <<parameters>>.plate_bolt_diameter * 1.5
  expr: Constraints[2] = <<parameters>>.plate_hole_spacing / 2
  expr: Constraints[3] = <<parameters>>.plate_hole_spacing / 2
  expr: Constraints[4] = <<parameters>>.chassis_hole_diameter
  expr: Constraints[5] = <<parameters>>.chassis_hole_diameter
  sketch-geometry (6):
    g0: Circle CenterX=-25 CenterY=0 CenterZ=0 NormalX=0 NormalY=0 NormalZ=1 AngleXU=0 Radius=1.6
    g1: Circle CenterX=25 CenterY=0 CenterZ=0 NormalX=0 NormalY=0 NormalZ=1 AngleXU=0 Radius=1.6
    g2: ArcOfCircle CenterX=-25 CenterY=0 CenterZ=0 NormalX=0 NormalY=0 NormalZ=1 AngleXU=0 Radius=4.8 StartAngle=1.5708 EndAngle=4.71239
    g3: ArcOfCircle CenterX=25 CenterY=0 CenterZ=0 NormalX=0 NormalY=0 NormalZ=1 AngleXU=0 Radius=4.8 StartAngle=4.71239 EndAngle=7.85398
    g4: LineSegment StartX=-25 StartY=-4.8 StartZ=0 EndX=25 EndY=-4.8 EndZ=0
    g5: LineSegment StartX=25 StartY=4.8 StartZ=0 EndX=-25 EndY=4.8 EndZ=0
  constraints (14):
    c: PointOnObject(g0,g-1)
    c: PointOnObject(g1,g-1)
    c: DistanceX(g-1,g1) = 25
    c: DistanceX(g0,g-1) = 25
    c: Diameter(g0) = 3.2
    c: Diameter(g1) = 3.2
    c: Tangent(g2,g4) = -1.5708
    c: Tangent(g4,g3) = -1.5708
    c: Tangent(g3,g5) = -1.5708
    c: Tangent(g5,g2) = -1.5708
    c: Equal(g2,g3)
    c: Coincident(g2,g0)
    c: Coincident(g3,g1)
    c: DistanceY(g0,g2) = 4.8
FEATURE [PartDesign::Pad] Pad004  label="GPSMountPlateMount"
  BaseFeature = -> Pad003
  Direction = (0,0,1)
  Length = 2.5
  Length2 = 10
  Profile = -> Sketch010
  ReferenceAxis = -> Sketch010 [N_Axis]
  Suppressed = false
  Type = 0
FEATURE [PartDesign::Fillet] Fillet002  label="GPSMountCornerSmoothing"
  Base = -> Pad004 [Edge73,Edge9,Edge5,Edge28,Edge76,Edge80]
  BaseFeature = -> Pad004
  Radius = 2
  SupportTransform = false
  Suppressed = false
  UseAllEdges = false
FEATURE [Sketcher::SketchObject] Sketch011  label="GPSMountPostBaseSketch"
  ArcFitTolerance = 0
  AttachmentSupport = -> [Fillet002]
  FullyConstrained = true
  MakeInternals = false
  MapMode = 5
  Placement = pos=(0,0,2.5) rot=(0,0,1;0rad)
  expr: Constraints[0] = <<parameters>>.gps_hole_spacing_x / 2
  expr: Constraints[10] = <<parameters>>.gps_bolt_diameter
  expr: Constraints[11] = <<parameters>>.gps_bolt_diameter
  expr: Constraints[16] = <<parameters>>.plate_nut_diameter * 2
  expr: Constraints[17] = <<parameters>>.plate_nut_diameter * 2
  expr: Constraints[18] = <<parameters>>.plate_nut_diameter * 2
  expr: Constraints[19] = <<parameters>>.plate_nut_diameter * 2
  expr: Constraints[1] = <<parameters>>.gps_hole_spacing_y / 2
  expr: Constraints[3] = <<parameters>>.gps_hole_spacing_y
  expr: Constraints[4] = <<parameters>>.gps_hole_spacing_x
  expr: Constraints[8] = <<parameters>>.gps_bolt_diameter
  expr: Constraints[9] = <<parameters>>.gps_bolt_diameter
  sketch-geometry (8):
    g0: Circle CenterX=19.05 CenterY=19.05 CenterZ=0 NormalX=0 NormalY=0 NormalZ=1 AngleXU=0 Radius=1.6
    g1: Circle CenterX=-19.05 CenterY=19.05 CenterZ=0 NormalX=0 NormalY=0 NormalZ=1 AngleXU=0 Radius=1.6
    g2: Circle CenterX=-19.05 CenterY=-19.05 CenterZ=0 NormalX=0 NormalY=0 NormalZ=1 AngleXU=0 Radius=1.6
    g3: Circle CenterX=19.05 CenterY=-19.05 CenterZ=0 NormalX=0 NormalY=0 NormalZ=1 AngleXU=0 Radius=1.6
    g4: Circle CenterX=-19.05 CenterY=19.05 CenterZ=0 NormalX=0 NormalY=0 NormalZ=1 AngleXU=0 Radius=6.5
    g5: Circle CenterX=19.05 CenterY=19.05 CenterZ=0 NormalX=0 NormalY=0 NormalZ=1 AngleXU=0 Radius=6.5
    g6: Circle CenterX=19.05 CenterY=-19.05 CenterZ=0 NormalX=0 NormalY=0 NormalZ=1 AngleXU=0 Radius=6.5
    g7: Circle CenterX=-19.05 CenterY=-19.05 CenterZ=0 NormalX=0 NormalY=0 NormalZ=1 AngleXU=0 Radius=6.5
  constraints (20):
    c: DistanceX(g1,g-1) = 19.05
    c: DistanceY(g-1,g1) = 19.05
    c: Vertical(g1,g2)
    c: DistanceY(g2,g1) = 38.1
    c: DistanceX(g1,g0) = 38.1
    c: Horizontal(g1,g0)
    c: Vertical(g0,g3)
    c: Horizontal(g2,g3)
    c: Diameter(g1) = 3.2
    c: Diameter(g0) = 3.2
    c: Diameter(g3) = 3.2
    c: Diameter(g2) = 3.2
    c: Coincident(g4,g1)
    c: Coincident(g5,g0)
    c: Coincident(g6,g3)
    c: Coincident(g7,g2)
    c: Diameter(g7) = 13
    c: Diameter(g6) = 13
    c: Diameter(g5) = 13
    c: Diameter(g4) = 13
FEATURE [PartDesign::Pad] Pad005  label="GPSMountPostBase"
  BaseFeature = -> Fillet002
  Direction = (0,0,1)
  Length = 2
  Length2 = 10
  Profile = -> Sketch011
  ReferenceAxis = -> Sketch011 [N_Axis]
  Suppressed = false
  Type = 0
FEATURE [Sketcher::SketchObject] Sketch012  label="GPSMountPostRiseSketch"
  ArcFitTolerance = 0
  AttachmentSupport = -> [Pad005]
  FullyConstrained = true
  MakeInternals = false
  MapMode = 5
  Placement = pos=(0,0,4.5) rot=(0,0,1;0rad)
  expr: Constraints[0] = <<parameters>>.gps_hole_spacing_x / 2
  expr: Constraints[10] = <<parameters>>.gps_bolt_diameter
  expr: Constraints[11] = <<parameters>>.gps_bolt_diameter
  expr: Constraints[16] = <<parameters>>.gps_bolt_diameter * 2
  expr: Constraints[17] = <<parameters>>.gps_bolt_diameter * 2
  expr: Constraints[18] = <<parameters>>.gps_bolt_diameter * 2
  expr: Constraints[19] = <<parameters>>.gps_bolt_diameter * 2
  expr: Constraints[1] = <<parameters>>.gps_hole_spacing_y / 2
  expr: Constraints[3] = <<parameters>>.gps_hole_spacing_y
  expr: Constraints[4] = <<parameters>>.gps_hole_spacing_x
  expr: Constraints[8] = <<parameters>>.gps_bolt_diameter
  expr: Constraints[9] = <<parameters>>.gps_bolt_diameter
  sketch-geometry (8):
    g0: Circle CenterX=19.05 CenterY=19.05 CenterZ=0 NormalX=0 NormalY=0 NormalZ=1 AngleXU=0 Radius=1.6
    g1: Circle CenterX=-19.05 CenterY=19.05 CenterZ=0 NormalX=0 NormalY=0 NormalZ=1 AngleXU=0 Radius=1.6
    g2: Circle CenterX=-19.05 CenterY=-19.05 CenterZ=0 NormalX=0 NormalY=0 NormalZ=1 AngleXU=0 Radius=1.6
    g3: Circle CenterX=19.05 CenterY=-19.05 CenterZ=0 NormalX=0 NormalY=0 NormalZ=1 AngleXU=0 Radius=1.6
    g4: Circle CenterX=-19.05 CenterY=19.05 CenterZ=0 NormalX=0 NormalY=0 NormalZ=1 AngleXU=0 Radius=3.2
    g5: Circle CenterX=19.05 CenterY=19.05 CenterZ=0 NormalX=0 NormalY=0 NormalZ=1 AngleXU=0 Radius=3.2
    g6: Circle CenterX=19.05 CenterY=-19.05 CenterZ=0 NormalX=0 NormalY=0 NormalZ=1 AngleXU=0 Radius=3.2
    g7: Circle CenterX=-19.05 CenterY=-19.05 CenterZ=0 NormalX=0 NormalY=0 NormalZ=1 AngleXU=0 Radius=3.2
  constraints (20):
    c: DistanceX(g1,g-1) = 19.05
    c: DistanceY(g-1,g1) = 19.05
    c: Vertical(g1,g2)
    c: DistanceY(g2,g1) = 38.1
    c: DistanceX(g1,g0) = 38.1
    c: Horizontal(g1,g0)
    c: Vertical(g0,g3)
    c: Horizontal(g2,g3)
    c: Diameter(g1) = 3.2
    c: Diameter(g0) = 3.2
    c: Diameter(g3) = 3.2
    c: Diameter(g2) = 3.2
    c: Coincident(g4,g1)
    c: Coincident(g5,g0)
    c: Coincident(g6,g3)
    c: Coincident(g7,g2)
    c: Diameter(g7) = 6.4
    c: Diameter(g6) = 6.4
    c: Diameter(g5) = 6.4
    c: Diameter(g4) = 6.4
FEATURE [PartDesign::Pad] Pad006  label="GPSMountPostRise"
  BaseFeature = -> Pad005
  Direction = (0,0,1)
  Length = 4.25
  Length2 = 10
  Profile = -> Sketch012
  ReferenceAxis = -> Sketch012 [N_Axis]
  Suppressed = false
  Type = 0
FEATURE [PartDesign::Fillet] Fillet003  label="GPSMountPostSmoothing"
  Base = -> Pad006 [Edge102,Edge146,Edge145,Edge103]
  BaseFeature = -> Pad006
  Radius = 1
  SupportTransform = false
  Suppressed = false
  UseAllEdges = false
FEATURE [Sketcher::SketchObject] Sketch013  label="GPSMountNutCatchesSketch"
  ArcFitTolerance = 0
  AttachmentSupport = -> [Fillet003]
  FullyConstrained = true
  MakeInternals = false
  MapMode = 5
  Placement = pos=(0,0,0) rot=(1,0,0;3.14159rad)
  expr: Constraints[68] = <<parameters>>.gps_hole_spacing_x / 2
  expr: Constraints[69] = <<parameters>>.gps_hole_spacing_y / 2
  expr: Constraints[70] = <<parameters>>.gps_hole_spacing_x
  expr: Constraints[71] = <<parameters>>.gps_hole_spacing_y
  expr: Constraints[80] = <<parameters>>.plate_nut_diameter
  expr: Constraints[81] = <<parameters>>.plate_nut_diameter
  expr: Constraints[82] = <<parameters>>.plate_nut_diameter
  expr: Constraints[83] = <<parameters>>.plate_nut_diameter
  sketch-geometry (28):
    g0: LineSegment StartX=-15.8 StartY=19.05 StartZ=0 EndX=-17.425 EndY=21.8646 EndZ=0
    g1: LineSegment StartX=-17.425 StartY=21.8646 StartZ=0 EndX=-20.675 EndY=21.8646 EndZ=0
    g2: LineSegment StartX=-20.675 StartY=21.8646 StartZ=0 EndX=-22.3 EndY=19.05 EndZ=0
    g3: LineSegment StartX=-22.3 StartY=19.05 StartZ=0 EndX=-20.675 EndY=16.2354 EndZ=0
    g4: LineSegment StartX=-20.675 StartY=16.2354 StartZ=0 EndX=-17.425 EndY=16.2354 EndZ=0
    g5: LineSegment StartX=-17.425 StartY=16.2354 StartZ=0 EndX=-15.8 EndY=19.05 EndZ=0
    g6: Circle [constr] CenterX=-19.05 CenterY=19.05 CenterZ=0 NormalX=0 NormalY=0 NormalZ=1 AngleXU=0 Radius=3.25
    g7: LineSegment StartX=22.3 StartY=19.05 StartZ=0 EndX=20.675 EndY=21.8646 EndZ=0
    g8: LineSegment StartX=20.675 StartY=21.8646 StartZ=0 EndX=17.425 EndY=21.8646 EndZ=0
    g9: LineSegment StartX=17.425 StartY=21.8646 StartZ=0 EndX=15.8 EndY=19.05 EndZ=0
    g10: LineSegment StartX=15.8 StartY=19.05 StartZ=0 EndX=17.425 EndY=16.2354 EndZ=0
    g11: LineSegment StartX=17.425 StartY=16.2354 StartZ=0 EndX=20.675 EndY=16.2354 EndZ=0
    g12: LineSegment StartX=20.675 StartY=16.2354 StartZ=0 EndX=22.3 EndY=19.05 EndZ=0
    g13: Circle [constr] CenterX=19.05 CenterY=19.05 CenterZ=0 NormalX=0 NormalY=0 NormalZ=1 AngleXU=0 Radius=3.25
    g14: LineSegment StartX=22.3 StartY=-19.05 StartZ=0 EndX=20.675 EndY=-16.2354 EndZ=0
    g15: LineSegment StartX=20.675 StartY=-16.2354 StartZ=0 EndX=17.425 EndY=-16.2354 EndZ=0
    g16: LineSegment StartX=17.425 StartY=-16.2354 StartZ=0 EndX=15.8 EndY=-19.05 EndZ=0
    g17: LineSegment StartX=15.8 StartY=-19.05 StartZ=0 EndX=17.425 EndY=-21.8646 EndZ=0
    g18: LineSegment StartX=17.425 StartY=-21.8646 StartZ=0 EndX=20.675 EndY=-21.8646 EndZ=0
    g19: LineSegment StartX=20.675 StartY=-21.8646 StartZ=0 EndX=22.3 EndY=-19.05 EndZ=0
    g20: Circle [constr] CenterX=19.05 CenterY=-19.05 CenterZ=0 NormalX=0 NormalY=0 NormalZ=1 AngleXU=0 Radius=3.25
    g21: LineSegment StartX=-15.8 StartY=-19.05 StartZ=0 EndX=-17.425 EndY=-16.2354 EndZ=0
    g22: LineSegment StartX=-17.425 StartY=-16.2354 StartZ=0 EndX=-20.675 EndY=-16.2354 EndZ=0
    g23: LineSegment StartX=-20.675 StartY=-16.2354 StartZ=0 EndX=-22.3 EndY=-19.05 EndZ=0
    g24: LineSegment StartX=-22.3 StartY=-19.05 StartZ=0 EndX=-20.675 EndY=-21.8646 EndZ=0
    g25: LineSegment StartX=-20.675 StartY=-21.8646 StartZ=0 EndX=-17.425 EndY=-21.8646 EndZ=0
    g26: LineSegment StartX=-17.425 StartY=-21.8646 StartZ=0 EndX=-15.8 EndY=-19.05 EndZ=0
    g27: Circle [constr] CenterX=-19.05 CenterY=-19.05 CenterZ=0 NormalX=0 NormalY=0 NormalZ=1 AngleXU=0 Radius=3.25
  constraints (68):
    c: Coincident(g0,g1)
    c: Coincident(g1,g2)
    c: Coincident(g2,g3)
    c: Coincident(g3,g4)
    c: Coincident(g4,g5)
    c: Coincident(g5,g0)
    c: Equal(g0, g1-g5) x5
    c: PointOnObject(g0,g6)
    c: PointOnObject(g1,g6)
    c: PointOnObject(g2,g6)
    c: PointOnObject(g3,g6)
    c: PointOnObject(g4,g6)
    c: PointOnObject(g5,g6)
    c: Coincident(g7,g8)
    c: Coincident(g8,g9)
    c: Coincident(g9,g10)
    c: Coincident(g10,g11)
    c: Coincident(g11,g12)
    c: Coincident(g12,g7)
    c: Equal(g7, g8-g12) x5
    c: PointOnObject(g7,g13)
    c: PointOnObject(g8,g13)
    c: PointOnObject(g9,g13)
    c: PointOnObject(g10,g13)
    c: PointOnObject(g11,g13)
    c: PointOnObject(g12,g13)
    c: Coincident(g14,g15)
    c: Coincident(g15,g16)
    c: Coincident(g16,g17)
    c: Coincident(g17,g18)
    c: Coincident(g18,g19)
    c: Coincident(g19,g14)
    c: Equal(g14, g15-g19) x5
    c: PointOnObject(g14,g20)
    c: PointOnObject(g15,g20)
    c: PointOnObject(g16,g20)
    c: PointOnObject(g17,g20)
    c: PointOnObject(g18,g20)
    c: PointOnObject(g19,g20)
    c: Coincident(g21,g22)
    c: Coincident(g22,g23)
    c: Coincident(g23,g24)
    c: Coincident(g24,g25)
    c: Coincident(g25,g26)
    c: Coincident(g26,g21)
    c: Equal(g21, g22-g26) x5
    c: PointOnObject(g21,g27)
    c: PointOnObject(g22,g27)
    c: PointOnObject(g23,g27)
    c: PointOnObject(g24,g27)
    c: PointOnObject(g25,g27)
    c: PointOnObject(g26,g27)
    c: DistanceX(g6,g-1) = 19.05
    c: DistanceY(g-1,g6) = 19.05
    c: DistanceX(g6,g13) = 38.1
    c: DistanceY(g27,g6) = 38.1
    c: Horizontal(g2,g0)
    c: Horizontal(g9,g7)
    c: Horizontal(g14,g16)
    c: Horizontal(g23,g21)
    c: Vertical(g27,g6)
    c: Horizontal(g6,g13)
    c: Vertical(g13,g20)
    c: Horizontal(g20,g27)
    c: DistanceX(g2,g0) = 6.5
    c: DistanceX(g9,g7) = 6.5
    c: DistanceX(g16,g14) = 6.5
    c: DistanceX(g23,g21) = 6.5
FEATURE [PartDesign::Pocket] Pocket006  label="GPSMountNutCatches"
  BaseFeature = -> Fillet003
  Direction = (0,0,1)
  Length = 2.5
  Length2 = 5
  Profile = -> Sketch013
  ReferenceAxis = -> Sketch013 [N_Axis]
  Suppressed = false
  Type = 0
FEATURE [PartDesign::Body] Body003  label="GPSMountBody"
  AllowCompound = false
  Group = -> [Sketch009,Pad003,Sketch010,Pad004,Fillet002,Sketch011,Pad005,Sketch012,Pad006,Fillet003,Sketch013,Pocket006]
  Origin = -> Origin007
  Tip = -> Pocket006
FEATURE [App::Part] Part003  label="GPSMount"
  Group = -> [Body003]
  Origin = -> Origin006
FEATURE [Sketcher::SketchObject] Sketch014  label="RPiMountBaseSketch"
  ArcFitTolerance = 0
  AttachmentSupport = -> [XY_Plane009]
  FullyConstrained = true
  MakeInternals = false
  MapMode = 5
  expr: Constraints[100] = <<parameters>>.rpi_hole_spacing_x / 2 + <<parameters>>.rpi_standoff_offset - (<<parameters>>.rpi_hole_spacing_y / 2 - <<parameters>>.rpi_standoff_offset)
  expr: Constraints[102] = <<parameters>>.rpi_standoff_offset
  expr: Constraints[113] = -(<<parameters>>.rpi_hole_spacing_x / 2 - <<parameters>>.rpi_standoff_offset) + <<parameters>>.rpi_hole_spacing_y / 2 + <<parameters>>.rpi_standoff_offset
  expr: Constraints[121] = <<parameters>>.rpi_standoff_offset
  expr: Constraints[124] = <<parameters>>.rpi_standoff_offset
  expr: Constraints[69] = <<parameters>>.plate_bolt_diameter
  expr: Constraints[74] = <<parameters>>.rpi_standoff_diameter
  expr: Constraints[75] = <<parameters>>.rpi_standoff_diameter
  expr: Constraints[76] = <<parameters>>.rpi_standoff_diameter
  expr: Constraints[77] = <<parameters>>.rpi_standoff_diameter
  expr: Constraints[78] = <<parameters>>.rpi_hole_spacing_x / 2
  expr: Constraints[79] = <<parameters>>.rpi_hole_spacing_y / 2
  expr: Constraints[84] = <<parameters>>.rpi_hole_spacing_x
  expr: Constraints[85] = <<parameters>>.rpi_hole_spacing_y
  expr: Constraints[86] = <<parameters>>.rpi_standoff_offset
  expr: Constraints[87] = <<parameters>>.rpi_standoff_offset
  expr: Constraints[88] = <<parameters>>.rpi_standoff_offset
  expr: Constraints[96] = -(<<parameters>>.rpi_hole_spacing_x / 2 - <<parameters>>.rpi_standoff_offset) + <<parameters>>.rpi_hole_spacing_y / 2 + <<parameters>>.rpi_standoff_offset
  expr: Constraints[97] = <<parameters>>.rpi_hole_spacing_x / 2 + <<parameters>>.rpi_standoff_offset - (<<parameters>>.rpi_hole_spacing_y / 2 - <<parameters>>.rpi_standoff_offset)
  sketch-geometry (45):
    g0: LineSegment StartX=25.875 StartY=26.6184 StartZ=0 EndX=27.25 EndY=29 EndZ=0
    g1: LineSegment StartX=27.25 StartY=29 StartZ=0 EndX=25.875 EndY=31.3816 EndZ=0
    g2: LineSegment StartX=25.875 StartY=31.3816 StartZ=0 EndX=23.125 EndY=31.3816 EndZ=0
    g3: LineSegment StartX=23.125 StartY=31.3816 StartZ=0 EndX=21.75 EndY=29 EndZ=0
    g4: LineSegment StartX=21.75 StartY=29 StartZ=0 EndX=23.125 EndY=26.6184 EndZ=0
    g5: LineSegment StartX=23.125 StartY=26.6184 StartZ=0 EndX=25.875 EndY=26.6184 EndZ=0
    g6: Circle [constr] CenterX=24.5 CenterY=29 CenterZ=0 NormalX=0 NormalY=0 NormalZ=1 AngleXU=0 Radius=2.75
    g7: LineSegment StartX=25.875 StartY=-31.3816 StartZ=0 EndX=27.25 EndY=-29 EndZ=0
    g8: LineSegment StartX=27.25 StartY=-29 StartZ=0 EndX=25.875 EndY=-26.6184 EndZ=0
    g9: LineSegment StartX=25.875 StartY=-26.6184 StartZ=0 EndX=23.125 EndY=-26.6184 EndZ=0
    g10: LineSegment StartX=23.125 StartY=-26.6184 StartZ=0 EndX=21.75 EndY=-29 EndZ=0
    g11: LineSegment StartX=21.75 StartY=-29 StartZ=0 EndX=23.125 EndY=-31.3816 EndZ=0
    g12: LineSegment StartX=23.125 StartY=-31.3816 StartZ=0 EndX=25.875 EndY=-31.3816 EndZ=0
    g13: Circle [constr] CenterX=24.5 CenterY=-29 CenterZ=0 NormalX=0 NormalY=0 NormalZ=1 AngleXU=0 Radius=2.75
    g14: LineSegment StartX=-23.125 StartY=-31.3816 StartZ=0 EndX=-21.75 EndY=-29 EndZ=0
    g15: LineSegment StartX=-21.75 StartY=-29 StartZ=0 EndX=-23.125 EndY=-26.6184 EndZ=0
    g16: LineSegment StartX=-23.125 StartY=-26.6184 StartZ=0 EndX=-25.875 EndY=-26.6184 EndZ=0
    g17: LineSegment StartX=-25.875 StartY=-26.6184 StartZ=0 EndX=-27.25 EndY=-29 EndZ=0
    g18: LineSegment StartX=-27.25 StartY=-29 StartZ=0 EndX=-25.875 EndY=-31.3816 EndZ=0
    g19: LineSegment StartX=-25.875 StartY=-31.3816 StartZ=0 EndX=-23.125 EndY=-31.3816 EndZ=0
    g20: Circle [constr] CenterX=-24.5 CenterY=-29 CenterZ=0 NormalX=0 NormalY=0 NormalZ=1 AngleXU=0 Radius=2.75
    g21: LineSegment StartX=-23.125 StartY=26.6184 StartZ=0 EndX=-21.75 EndY=29 EndZ=0
    g22: LineSegment StartX=-21.75 StartY=29 StartZ=0 EndX=-23.125 EndY=31.3816 EndZ=0
    g23: LineSegment StartX=-23.125 StartY=31.3816 StartZ=0 EndX=-25.875 EndY=31.3816 EndZ=0
    g24: LineSegment StartX=-25.875 StartY=31.3816 StartZ=0 EndX=-27.25 EndY=29 EndZ=0
    g25: LineSegment StartX=-27.25 StartY=29 StartZ=0 EndX=-25.875 EndY=26.6184 EndZ=0
    g26: LineSegment StartX=-25.875 StartY=26.6184 StartZ=0 EndX=-23.125 EndY=26.6184 EndZ=0
    g27: Circle [constr] CenterX=-24.5 CenterY=29 CenterZ=0 NormalX=0 NormalY=0 NormalZ=1 AngleXU=0 Radius=2.75
    g28: Circle CenterX=0 CenterY=0 CenterZ=0 NormalX=0 NormalY=0 NormalZ=1 AngleXU=0 Radius=1.6
    g29: GeomPoint [constr] X=-28.3891 Y=25.1109 Z=0
    g30: GeomPoint [constr] X=-20.6109 Y=32.8891 Z=0
    g31: ArcOfCircle CenterX=-24.5 CenterY=29 CenterZ=0 NormalX=0 NormalY=0 NormalZ=1 AngleXU=0 Radius=5.5 StartAngle=0.785398 EndAngle=3.92699
    g32: LineSegment StartX=-20.6109 StartY=32.8891 StartZ=0 EndX=7.1e-15 EndY=12.2782 EndZ=0
    g33: LineSegment StartX=-28.3891 StartY=25.1109 StartZ=0 EndX=-3.27817 EndY=0 EndZ=0
    g34: LineSegment StartX=20.6109 StartY=32.8891 StartZ=0 EndX=7.1e-15 EndY=12.2782 EndZ=0
    g35: LineSegment StartX=28.3891 StartY=25.1109 StartZ=0 EndX=3.27817 EndY=0 EndZ=0
    g36: GeomPoint [constr] X=28.3891 Y=-25.1109 Z=0
    g37: GeomPoint [constr] X=-28.3891 Y=-25.1109 Z=0
    g38: ArcOfCircle CenterX=24.5 CenterY=-29 CenterZ=0 NormalX=0 NormalY=0 NormalZ=1 AngleXU=0 Radius=5.5 StartAngle=3.92699 EndAngle=7.06858
    g39: ArcOfCircle CenterX=-24.5 CenterY=-29 CenterZ=0 NormalX=0 NormalY=0 NormalZ=1 AngleXU=0 Radius=5.5 StartAngle=2.35619 EndAngle=5.49779
    g40: LineSegment StartX=-20.6109 StartY=-32.8891 StartZ=0 EndX=0 EndY=-12.2782 EndZ=0
    g41: LineSegment StartX=-1.2e-15 StartY=-12.2782 StartZ=0 EndX=20.6109 EndY=-32.8891 EndZ=0
    g42: LineSegment StartX=28.3891 StartY=-25.1109 StartZ=0 EndX=3.27817 EndY=0 EndZ=0
    g43: LineSegment StartX=-28.3891 StartY=-25.1109 StartZ=0 EndX=-3.27817 EndY=0 EndZ=0
    g44: ArcOfCircle CenterX=24.5 CenterY=29 CenterZ=0 NormalX=0 NormalY=0 NormalZ=1 AngleXU=0 Radius=5.5 StartAngle=5.49779 EndAngle=8.63938
  constraints (110):
    c: Coincident(g0,g1)
    c: Coincident(g1,g2)
    c: Coincident(g2,g3)
    c: Coincident(g3,g4)
    c: Coincident(g4,g5)
    c: Coincident(g5,g0)
    c: Equal(g0, g1-g5) x5
    c: PointOnObject(g0,g6)
    c: PointOnObject(g1,g6)
    c: PointOnObject(g2,g6)
    c: PointOnObject(g3,g6)
    c: PointOnObject(g4,g6)
    c: PointOnObject(g5,g6)
    c: Coincident(g7,g8)
    c: Coincident(g8,g9)
    c: Coincident(g9,g10)
    c: Coincident(g10,g11)
    c: Coincident(g11,g12)
    c: Coincident(g12,g7)
    c: Equal(g7, g8-g12) x5
    c: PointOnObject(g7,g13)
    c: PointOnObject(g8,g13)
    c: PointOnObject(g9,g13)
    c: PointOnObject(g10,g13)
    c: PointOnObject(g11,g13)
    c: PointOnObject(g12,g13)
    c: Coincident(g14,g15)
    c: Coincident(g15,g16)
    c: Coincident(g16,g17)
    c: Coincident(g17,g18)
    c: Coincident(g18,g19)
    c: Coincident(g19,g14)
    c: Equal(g14, g15-g19) x5
    c: PointOnObject(g14,g20)
    c: PointOnObject(g15,g20)
    c: PointOnObject(g16,g20)
    c: PointOnObject(g17,g20)
    c: PointOnObject(g18,g20)
    c: PointOnObject(g19,g20)
    c: Coincident(g21,g22)
    c: Coincident(g22,g23)
    c: Coincident(g23,g24)
    c: Coincident(g24,g25)
    c: Coincident(g25,g26)
    c: Coincident(g26,g21)
    c: Equal(g21, g22-g26) x5
    c: PointOnObject(g21,g27)
    c: PointOnObject(g22,g27)
    c: PointOnObject(g23,g27)
    c: PointOnObject(g24,g27)
    c: PointOnObject(g25,g27)
    c: PointOnObject(g26,g27)
    c: Coincident(g28,g-1)
    c: Diameter(g28) = 3.2
    c: Horizontal(g0,g3)
    c: Horizontal(g24,g21)
    c: Horizontal(g17,g14)
    c: Horizontal(g10,g7)
    c: DistanceX(g24,g21) = 5.5
    c: DistanceX(g3,g0) = 5.5
    c: DistanceX(g10,g7) = 5.5
    c: DistanceX(g17,g14) = 5.5
    c: DistanceX(g27,g28) = 24.5
    c: DistanceY(g28,g27) = 29
    c: Vertical(g20,g27)
    c: Vertical(g6,g13)
    c: Horizontal(g13,g20)
    c: Horizontal(g6,g27)
    c: DistanceX(g27,g6) = 49
    c: DistanceY(g20,g27) = 58
    c: DistanceY(g27,g30) = 3.88909
    c: DistanceX(g29,g27) = 3.88909
    c: DistanceY(g29,g27) = 3.88909
    c: Coincident(g31,g27)
    c: Coincident(g31,g30)
    c: Coincident(g31,g29)
    c: Coincident(g32,g31)
    c: PointOnObject(g32,g-2)
    c: Coincident(g33,g31)
    c: PointOnObject(g33,g-1)
    c: DistanceY(g28,g32) = 12.2782
    c: DistanceX(g33,g28) = 3.27817
    c: Coincident(g34,g32)
    c: PointOnObject(g35,g-1)
    c: DistanceX(g28,g35) = 3.27817
    c: Vertical(g31,g37)
    c: DistanceY(g13,g36) = 3.88909
    c: Coincident(g38,g13)
    c: Coincident(g38,g36)
    c: Horizontal(g38,g37)
    c: Coincident(g39,g20)
    c: Coincident(g39,g37)
    c: Horizontal(g39,g38)
    c: Coincident(g40,g39)
    c: PointOnObject(g40,g-2)
    c: Coincident(g41,g40)
    c: Coincident(g41,g38)
    c: DistanceY(g40,g28) = 12.2782
    c: Coincident(g42,g38)
    c: Coincident(g42,g35)
    c: Coincident(g43,g39)
    c: Coincident(g43,g33)
    c: Coincident(g44,g6)
    c: Coincident(g44,g34)
    c: Coincident(g44,g35)
    c: DistanceX(g34,g44) = 3.88909
    c: Horizontal(g34,g31)
    c: Vertical(g38,g35)
    c: DistanceX(g44,g35) = 3.88909
    c: Vertical(g38,g34)
FEATURE [PartDesign::Pad] Pad007  label="RPiMountBase"
  Direction = (0,0,1)
  Length = 2.5
  Length2 = 10
  Profile = -> Sketch014
  ReferenceAxis = -> Sketch014 [N_Axis]
  Suppressed = false
  Type = 0
FEATURE [Sketcher::SketchObject] Sketch015  label="RPiMountPlateMountSketch"
  ArcFitTolerance = 0
  AttachmentSupport = -> [XY_Plane009]
  FullyConstrained = true
  MakeInternals = false
  MapMode = 5
  expr: Constraints[10] = <<parameters>>.rpi_standoff_diameter
  expr: Constraints[12] = <<parameters>>.plate_bolt_diameter
  expr: Constraints[8] = <<parameters>>.plate_bolt_diameter
  expr: Constraints[9] = <<parameters>>.plate_hole_spacing
  sketch-geometry (6):
    g0: ArcOfCircle CenterX=0 CenterY=0 CenterZ=0 NormalX=0 NormalY=0 NormalZ=1 AngleXU=0 Radius=5.5 StartAngle=0 EndAngle=3.14159
    g1: ArcOfCircle CenterX=0 CenterY=-50 CenterZ=0 NormalX=0 NormalY=0 NormalZ=1 AngleXU=0 Radius=5.5 StartAngle=3.14159 EndAngle=6.28319
    g2: LineSegment StartX=-5.5 StartY=7e-16 StartZ=0 EndX=-5.5 EndY=-50 EndZ=0
    g3: LineSegment StartX=5.5 StartY=-50 StartZ=0 EndX=5.5 EndY=0 EndZ=0
    g4: Circle CenterX=0 CenterY=0 CenterZ=0 NormalX=0 NormalY=0 NormalZ=1 AngleXU=0 Radius=1.6
    g5: Circle CenterX=0 CenterY=-50 CenterZ=0 NormalX=0 NormalY=0 NormalZ=1 AngleXU=0 Radius=1.6
  constraints (13):
    c: Tangent(g0,g2) = -1.5708
    c: Tangent(g2,g1) = -1.5708
    c: Tangent(g1,g3) = -1.5708
    c: Tangent(g3,g0) = -1.5708
    c: Equal(g0,g1)
    c: Coincident(g0,g-1)
    c: PointOnObject(g1,g-2)
    c: Coincident(g4,g0)
    c: Diameter(g4) = 3.2
    c: DistanceY(g1,g0) = 50
    c: DistanceX(g1,g1) = 5.5
    c: Coincident(g5,g1)
    c: Diameter(g5) = 3.2
FEATURE [PartDesign::Pad] Pad008  label="RPiMountPlateMount"
  BaseFeature = -> Pad007
  Direction = (0,0,1)
  Length = 2.5
  Length2 = 10
  Profile = -> Sketch015
  ReferenceAxis = -> Sketch015 [N_Axis]
  Suppressed = false
  Type = 0
FEATURE [Sketcher::SketchObject] Sketch016  label="RPiMountPostsSketch"
  ArcFitTolerance = 0
  AttachmentSupport = -> [Pad008]
  FullyConstrained = true
  MakeInternals = false
  MapMode = 5
  Placement = pos=(0,0,2.5) rot=(0,0,1;0rad)
  expr: Constraints[0] = <<parameters>>.rpi_hole_spacing_x / 2
  expr: Constraints[10] = <<parameters>>.rpi_standoff_diameter * 2
  expr: Constraints[11] = <<parameters>>.rpi_standoff_diameter * 2
  expr: Constraints[1] = <<parameters>>.rpi_hole_spacing_y / 2
  expr: Constraints[2] = <<parameters>>.rpi_hole_spacing_x
  expr: Constraints[6] = <<parameters>>.rpi_hole_spacing_y
  expr: Constraints[88] = <<parameters>>.rpi_standoff_diameter * 1.5
  expr: Constraints[89] = <<parameters>>.rpi_standoff_diameter * 1.5
  expr: Constraints[8] = <<parameters>>.rpi_standoff_diameter * 2
  expr: Constraints[90] = <<parameters>>.rpi_standoff_diameter * 1.5
  expr: Constraints[91] = <<parameters>>.rpi_standoff_diameter * 1.5
  expr: Constraints[9] = <<parameters>>.rpi_standoff_diameter * 2
  sketch-geometry (32):
    g0: Circle CenterX=-24.5 CenterY=29 CenterZ=0 NormalX=0 NormalY=0 NormalZ=1 AngleXU=0 Radius=5.5
    g1: Circle CenterX=24.5 CenterY=29 CenterZ=0 NormalX=0 NormalY=0 NormalZ=1 AngleXU=0 Radius=5.5
    g2: Circle CenterX=24.5 CenterY=-29 CenterZ=0 NormalX=0 NormalY=0 NormalZ=1 AngleXU=0 Radius=5.5
    g3: Circle CenterX=-24.5 CenterY=-29 CenterZ=0 NormalX=0 NormalY=0 NormalZ=1 AngleXU=0 Radius=5.5
    g4: LineSegment StartX=-20.375 StartY=29 StartZ=0 EndX=-22.4375 EndY=32.5724 EndZ=0
    g5: LineSegment StartX=-22.4375 StartY=32.5724 StartZ=0 EndX=-26.5625 EndY=32.5724 EndZ=0
    g6: LineSegment StartX=-26.5625 StartY=32.5724 StartZ=0 EndX=-28.625 EndY=29 EndZ=0
    g7: LineSegment StartX=-28.625 StartY=29 StartZ=0 EndX=-26.5625 EndY=25.4276 EndZ=0
    g8: LineSegment StartX=-26.5625 StartY=25.4276 StartZ=0 EndX=-22.4375 EndY=25.4276 EndZ=0
    g9: LineSegment StartX=-22.4375 StartY=25.4276 StartZ=0 EndX=-20.375 EndY=29 EndZ=0
    g10: Circle [constr] CenterX=-24.5 CenterY=29 CenterZ=0 NormalX=0 NormalY=0 NormalZ=1 AngleXU=0 Radius=4.125
    g11: LineSegment StartX=28.625 StartY=29 StartZ=0 EndX=26.5625 EndY=32.5724 EndZ=0
    g12: LineSegment StartX=26.5625 StartY=32.5724 StartZ=0 EndX=22.4375 EndY=32.5724 EndZ=0
    g13: LineSegment StartX=22.4375 StartY=32.5724 StartZ=0 EndX=20.375 EndY=29 EndZ=0
    g14: LineSegment StartX=20.375 StartY=29 StartZ=0 EndX=22.4375 EndY=25.4276 EndZ=0
    g15: LineSegment StartX=22.4375 StartY=25.4276 StartZ=0 EndX=26.5625 EndY=25.4276 EndZ=0
    g16: LineSegment StartX=26.5625 StartY=25.4276 StartZ=0 EndX=28.625 EndY=29 EndZ=0
    g17: Circle [constr] CenterX=24.5 CenterY=29 CenterZ=0 NormalX=0 NormalY=0 NormalZ=1 AngleXU=0 Radius=4.125
    g18: LineSegment StartX=28.625 StartY=-29 StartZ=0 EndX=26.5625 EndY=-25.4276 EndZ=0
    g19: LineSegment StartX=26.5625 StartY=-25.4276 StartZ=0 EndX=22.4375 EndY=-25.4276 EndZ=0
    g20: LineSegment StartX=22.4375 StartY=-25.4276 StartZ=0 EndX=20.375 EndY=-29 EndZ=0
    g21: LineSegment StartX=20.375 StartY=-29 StartZ=0 EndX=22.4375 EndY=-32.5724 EndZ=0
    g22: LineSegment StartX=22.4375 StartY=-32.5724 StartZ=0 EndX=26.5625 EndY=-32.5724 EndZ=0
    g23: LineSegment StartX=26.5625 StartY=-32.5724 StartZ=0 EndX=28.625 EndY=-29 EndZ=0
    g24: Circle [constr] CenterX=24.5 CenterY=-29 CenterZ=0 NormalX=0 NormalY=0 NormalZ=1 AngleXU=0 Radius=4.125
    g25: LineSegment StartX=-20.375 StartY=-29 StartZ=0 EndX=-22.4375 EndY=-25.4276 EndZ=0
    g26: LineSegment StartX=-22.4375 StartY=-25.4276 StartZ=0 EndX=-26.5625 EndY=-25.4276 EndZ=0
    g27: LineSegment StartX=-26.5625 StartY=-25.4276 StartZ=0 EndX=-28.625 EndY=-29 EndZ=0
    g28: LineSegment StartX=-28.625 StartY=-29 StartZ=0 EndX=-26.5625 EndY=-32.5724 EndZ=0
    g29: LineSegment StartX=-26.5625 StartY=-32.5724 StartZ=0 EndX=-22.4375 EndY=-32.5724 EndZ=0
    g30: LineSegment StartX=-22.4375 StartY=-32.5724 StartZ=0 EndX=-20.375 EndY=-29 EndZ=0
    g31: Circle [constr] CenterX=-24.5 CenterY=-29 CenterZ=0 NormalX=0 NormalY=0 NormalZ=1 AngleXU=0 Radius=4.125
  constraints (76):
    c: DistanceX(g0,g-1) = 24.5
    c: DistanceY(g-1,g0) = 29
    c: DistanceX(g0,g1) = 49
    c: Horizontal(g1,g0)
    c: Vertical(g2,g1)
    c: Vertical(g0,g3)
    c: DistanceY(g3,g0) = 58
    c: Horizontal(g3,g2)
    c: Diameter(g0) = 11
    c: Diameter(g1) = 11
    c: Diameter(g2) = 11
    c: Diameter(g3) = 11
    c: Coincident(g4,g5)
    c: Coincident(g5,g6)
    c: Coincident(g6,g7)
    c: Coincident(g7,g8)
    c: Coincident(g8,g9)
    c: Coincident(g9,g4)
    c: Equal(g4, g5-g9) x5
    c: PointOnObject(g4,g10)
    c: PointOnObject(g5,g10)
    c: PointOnObject(g6,g10)
    c: PointOnObject(g7,g10)
    c: PointOnObject(g8,g10)
    c: PointOnObject(g9,g10)
    c: Coincident(g10,g0)
    c: Coincident(g11,g12)
    c: Coincident(g12,g13)
    c: Coincident(g13,g14)
    c: Coincident(g14,g15)
    c: Coincident(g15,g16)
    c: Coincident(g16,g11)
    c: Equal(g11, g12-g16) x5
    c: PointOnObject(g11,g17)
    c: PointOnObject(g12,g17)
    c: PointOnObject(g13,g17)
    c: PointOnObject(g14,g17)
    c: PointOnObject(g15,g17)
    c: PointOnObject(g16,g17)
    c: Coincident(g17,g1)
    c: Coincident(g18,g19)
    c: Coincident(g19,g20)
    c: Coincident(g20,g21)
    c: Coincident(g21,g22)
    c: Coincident(g22,g23)
    c: Coincident(g23,g18)
    c: Equal(g18, g19-g23) x5
    c: PointOnObject(g18,g24)
    c: PointOnObject(g19,g24)
    c: PointOnObject(g20,g24)
    c: PointOnObject(g21,g24)
    c: PointOnObject(g22,g24)
    c: PointOnObject(g23,g24)
    c: Coincident(g24,g2)
    c: Coincident(g25,g26)
    c: Coincident(g26,g27)
    c: Coincident(g27,g28)
    c: Coincident(g28,g29)
    c: Coincident(g29,g30)
    c: Coincident(g30,g25)
    c: Equal(g25, g26-g30) x5
    c: PointOnObject(g25,g31)
    c: PointOnObject(g26,g31)
    c: PointOnObject(g27,g31)
    c: PointOnObject(g28,g31)
    c: PointOnObject(g29,g31)
    c: PointOnObject(g30,g31)
    c: Coincident(g31,g3)
    c: Horizontal(g6,g4)
    c: Horizontal(g13,g11)
    c: Horizontal(g20,g18)
    c: Horizontal(g27,g25)
    c: DistanceX(g6,g4) = 8.25
    c: DistanceX(g13,g11) = 8.25
    c: DistanceX(g20,g18) = 8.25
    c: DistanceX(g27,g25) = 8.25
FEATURE [PartDesign::Pad] Pad009  label="RPIMountPosts"
  BaseFeature = -> Pad008
  Direction = (0,0,1)
  Length = 1.25
  Length2 = 10
  Profile = -> Sketch016
  ReferenceAxis = -> Sketch016 [N_Axis]
  Suppressed = false
  Type = 0
FEATURE [Sketcher::SketchObject] Sketch017  label="RPiMountExpansionSketch"
  ArcFitTolerance = 0
  AttachmentSupport = -> [XY_Plane009]
  FullyConstrained = true
  MakeInternals = false
  MapMode = 5
  expr: Constraints[13] = <<parameters>>.plate_bolt_diameter
  sketch-geometry (5):
    g0: LineSegment StartX=-10 StartY=10 StartZ=0 EndX=10 EndY=10 EndZ=0
    g1: LineSegment StartX=10 StartY=10 StartZ=0 EndX=10 EndY=-10 EndZ=0
    g2: LineSegment StartX=10 StartY=-10 StartZ=0 EndX=-10 EndY=-10 EndZ=0
    g3: LineSegment StartX=-10 StartY=-10 StartZ=0 EndX=-10 EndY=10 EndZ=0
    g4: Circle CenterX=0 CenterY=0 CenterZ=0 NormalX=0 NormalY=0 NormalZ=1 AngleXU=0 Radius=1.6
  constraints (14):
    c: Coincident(g0,g1)
    c: Coincident(g1,g2)
    c: Coincident(g2,g3)
    c: Coincident(g3,g0)
    c: Horizontal(g0)
    c: Horizontal(g2)
    c: Vertical(g1)
    c: Vertical(g3)
    c: DistanceX(g0,g-1) = 10
    c: DistanceY(g-1,g0) = 10
    c: DistanceY(g2,g0) = 20
    c: DistanceX(g0,g0) = 20
    c: Coincident(g4,g-1)
    c: Diameter(g4) = 3.2
FEATURE [PartDesign::Pad] Pad010  label="RPiMountExpansion"
  BaseFeature = -> Pad009
  Direction = (0,0,1)
  Length = 2.5
  Length2 = 10
  Profile = -> Sketch017
  ReferenceAxis = -> Sketch017 [N_Axis]
  Suppressed = false
  Type = 0
FEATURE [PartDesign::Fillet] Fillet004  label="RPiMountCornerSmoothing"
  Base = -> Pad010 [Edge34,Edge7,Edge177,Edge232,Edge107,Edge47,Edge9]
  BaseFeature = -> Pad010
  Radius = 5
  SupportTransform = false
  Suppressed = false
  UseAllEdges = false
FEATURE [PartDesign::Body] Body004  label="RPiMountBody"
  AllowCompound = false
  Group = -> [Sketch014,Pad007,Sketch015,Sketch016,Pad008,Pad009,Sketch017,Pad010,Fillet004]
  Origin = -> Origin009
  Tip = -> Fillet004
FEATURE [App::Part] Part004  label="RPiMount"
  Group = -> [Body004]
  Origin = -> Origin008
FEATURE [Sketcher::SketchObject] Sketch018  label="ArduinoBoxLidCapSketch"
  ArcFitTolerance = 0
  AttachmentSupport = -> [XY_Plane011]
  FullyConstrained = true
  MakeInternals = false
  MapMode = 5
  expr: Constraints[0] = <<parameters>>.arduino_width / 2
  expr: Constraints[10] = <<parameters>>.wall_depth + 5.75 mm / 2 + <<parameters>>.margin + <<parameters>>.chassis_hole_spacing / 2
  expr: Constraints[11] = <<parameters>>.wall_depth + 5.75 mm / 2 + <<parameters>>.margin + <<parameters>>.chassis_hole_spacing / 2
  expr: Constraints[15] = <<parameters>>.arduino_hole4_offset_x
  expr: Constraints[16] = <<parameters>>.arduino_hole4_offset_y
  expr: Constraints[20] = <<parameters>>.arduino_hole3_offset_x
  expr: Constraints[22] = <<parameters>>.arduino_hole2_offset_x
  expr: Constraints[23] = <<parameters>>.arduino_hole2_offset_y
  expr: Constraints[25] = <<parameters>>.arduino_hole1_offset_y
  expr: Constraints[26] = <<parameters>>.arduino_hole1_offset_x
  expr: Constraints[27] = <<parameters>>.arduino_hole3_offset_y - 0.5 mm
  expr: Constraints[2] = <<parameters>>.arduino_length
  expr: Constraints[4] = <<parameters>>.margin + <<parameters>>.wall_depth + 0.25 mm
  expr: Constraints[9] = <<parameters>>.wall_depth + <<parameters>>.margin + 1.75 mm
  sketch-geometry (30):
    g0: GeomPoint [constr] X=26.67 Y=-65.54 Z=0
    g1: GeomPoint [constr] X=26.67 Y=3.04 Z=0
    g2: LineSegment StartX=-30.825 StartY=-68.49 StartZ=0 EndX=30.825 EndY=-68.49 EndZ=0
    g3: LineSegment StartX=-30.825 StartY=7.49 StartZ=0 EndX=-30.825 EndY=-68.49 EndZ=0
    g4: LineSegment StartX=-30.825 StartY=7.49 StartZ=0 EndX=30.825 EndY=7.49 EndZ=0
    g5: LineSegment StartX=30.825 StartY=7.49 StartZ=0 EndX=30.825 EndY=-68.49 EndZ=0
    g6: Circle CenterX=-8.89 CenterY=0.5 CenterZ=0 NormalX=0 NormalY=0 NormalZ=1 AngleXU=0 Radius=1.375
    g7: Circle CenterX=19.05 CenterY=0.5 CenterZ=0 NormalX=0 NormalY=0 NormalZ=1 AngleXU=0 Radius=1.375
    g8: Circle CenterX=-24.13 CenterY=-50.3 CenterZ=0 NormalX=0 NormalY=0 NormalZ=1 AngleXU=0 Radius=1.375
    g9: Circle CenterX=24.13 CenterY=-51.57 CenterZ=0 NormalX=0 NormalY=0 NormalZ=1 AngleXU=0 Radius=1.375
    g10: LineSegment StartX=15.4 StartY=-47.17 StartZ=0 EndX=-6.42 EndY=-47.17 EndZ=0
    g11: LineSegment StartX=-20.47 StartY=-52.67 StartZ=0 EndX=-20.47 EndY=-49.04 EndZ=0
    g12: LineSegment StartX=-6.42 StartY=-47.17 StartZ=0 EndX=-6.42 EndY=-52.67 EndZ=0
    g13: LineSegment StartX=-6.42 StartY=-52.67 StartZ=0 EndX=15.4 EndY=-52.67 EndZ=0
    g14: LineSegment StartX=-11.77 StartY=-49.04 StartZ=0 EndX=-11.77 EndY=-52.67 EndZ=0
    g15: LineSegment StartX=-20.47 StartY=-49.04 StartZ=0 EndX=-11.77 EndY=-49.04 EndZ=0
    g16: LineSegment StartX=-20.47 StartY=-52.67 StartZ=0 EndX=-11.77 EndY=-52.67 EndZ=0
    g17: LineSegment StartX=-2.42 StartY=-39.67 StartZ=0 EndX=4.48 EndY=-39.67 EndZ=0
    g18: LineSegment StartX=4.48 StartY=-39.67 StartZ=0 EndX=4.48 EndY=-45.17 EndZ=0
    g19: LineSegment StartX=4.48 StartY=-45.17 StartZ=0 EndX=-2.42 EndY=-45.17 EndZ=0
    g20: LineSegment StartX=-2.42 StartY=-45.17 StartZ=0 EndX=-2.42 EndY=-39.67 EndZ=0
    g21: LineSegment StartX=-21.15 StartY=-0.795 StartZ=0 EndX=-15.65 EndY=-0.795 EndZ=0
    g22: LineSegment StartX=-15.65 StartY=-0.795 StartZ=0 EndX=-15.65 EndY=-22.77 EndZ=0
    g23: LineSegment StartX=-15.65 StartY=-22.77 StartZ=0 EndX=-21.15 EndY=-22.77 EndZ=0
    g24: LineSegment StartX=-21.15 StartY=-22.77 StartZ=0 EndX=-21.15 EndY=-0.795 EndZ=0
    g25: LineSegment StartX=15.725 StartY=-3.145 StartZ=0 EndX=21.225 EndY=-3.145 EndZ=0
    g26: LineSegment StartX=21.225 StartY=-3.145 StartZ=0 EndX=21.225 EndY=-25.01 EndZ=0
    g27: LineSegment StartX=21.225 StartY=-25.01 StartZ=0 EndX=15.725 EndY=-25.01 EndZ=0
    g28: LineSegment StartX=15.725 StartY=-25.01 StartZ=0 EndX=15.725 EndY=-3.145 EndZ=0
    g29: LineSegment StartX=15.4 StartY=-52.67 StartZ=0 EndX=15.4 EndY=-47.17 EndZ=0
  constraints (88):
    c: DistanceX(g-1,g0) = 26.67
    c: Vertical(g1,g0)
    c: DistanceY(g0,g1) = 68.58
    c: Horizontal(g2)
    c: DistanceY(g2,g0) = 2.95
    c: Vertical(g3)
    c: Coincident(g2,g3)
    c: Horizontal(g4,g3)
    c: Coincident(g4,g3)
    c: DistanceY(g1,g4) = 4.45
    c: DistanceX(g3,g-1) = 30.825
    c: DistanceX(g-1,g4) = 30.825
    c: Coincident(g5,g4)
    c: Coincident(g5,g2)
    c: Vertical(g5)
    c: DistanceX(g6,g0) = 35.56
    c: DistanceY(g0,g6) = 66.04
    c: Diameter(g6) = 2.75
    c: Diameter(g7) = 2.75
    c: DistanceY(g-1,g7) = 0.5
    c: DistanceX(g7,g0) = 7.62
    c: Diameter(g8) = 2.75
    c: DistanceX(g8,g0) = 50.8
    c: DistanceY(g0,g8) = 15.24
    c: Diameter(g9) = 2.75
    c: DistanceY(g0,g9) = 13.97
    c: DistanceX(g9,g0) = 2.54
    c: DistanceY(g0,g-1) = 65.54
    c: DistanceX(g13,g9) = 8.73
    c: DistanceY(g13,g9) = 1.1
    c: DistanceY(g9,g10) = 4.4
    c: Horizontal(g10)
    c: DistanceX(g10,g9) = 30.55
    c: DistanceX(g11,g9) = 44.6
    c: Vertical(g11)
    c: Coincident(g12,g10)
    c: Vertical(g12)
    c: Horizontal(g12,g13)
    c: Coincident(g13,g12)
    c: Horizontal(g11,g12)
    c: Vertical(g14)
    c: Horizontal(g14,g11)
    c: Horizontal(g14,g11)
    c: Coincident(g15,g11)
    c: Coincident(g15,g14)
    c: Coincident(g16,g11)
    c: Coincident(g16,g14)
    c: DistanceX(g14,g9) = 35.9
    c: Coincident(g17,g18)
    c: Coincident(g18,g19)
    c: Coincident(g19,g20)
    c: Coincident(g20,g17)
    c: Horizontal(g17)
    c: Horizontal(g19)
    c: Vertical(g18)
    c: Vertical(g20)
    c: DistanceX(g18,g9) = 19.65
    c: DistanceY(g9,g18) = 6.4
    c: DistanceX(g19,g18) = 6.9
    c: DistanceY(g19,g17) = 5.5
    c: Coincident(g21,g22)
    c: Coincident(g22,g23)
    c: Coincident(g23,g24)
    c: Coincident(g24,g21)
    c: Horizontal(g21)
    c: Horizontal(g23)
    c: Vertical(g22)
    c: Vertical(g24)
    c: Coincident(g25,g26)
    c: Coincident(g26,g27)
    c: Coincident(g27,g28)
    c: Coincident(g28,g25)
    c: Horizontal(g25)
    c: Horizontal(g27)
    c: Vertical(g26)
    c: Vertical(g28)
    c: DistanceX(g7,g25) = 2.175
    c: DistanceY(g25,g7) = 3.645
    c: DistanceX(g27,g26) = 5.5
    c: DistanceY(g27,g25) = 21.865
    c: DistanceY(g23,g21) = 21.975
    c: DistanceX(g23,g22) = 5.5
    c: DistanceX(g21,g6) = 6.76
    c: DistanceY(g21,g6) = 1.295
    c: Coincident(g29,g13)
    c: Coincident(g29,g10)
    c: Vertical(g29)
    c: DistanceY(g9,g14) = 2.53
FEATURE [PartDesign::Pad] Pad011  label="ArduinoBoxLidCap"
  Direction = (0,0,1)
  Length = 2.5
  Length2 = 10
  Profile = -> Sketch018
  ReferenceAxis = -> Sketch018 [N_Axis]
  Suppressed = false
  Type = 0
FEATURE [Sketcher::SketchObject] Sketch019  label="ArduinoBoxLidWallsSketch"
  ArcFitTolerance = 0
  AttachmentSupport = -> [XY_Plane011]
  FullyConstrained = true
  MakeInternals = false
  MapMode = 5
  expr: Constraints[0] = <<parameters>>.arduino_width / 2
  expr: Constraints[10] = <<parameters>>.wall_depth + 5.75 mm / 2 + <<parameters>>.margin + <<parameters>>.chassis_hole_spacing / 2
  expr: Constraints[11] = <<parameters>>.wall_depth + 5.75 mm / 2 + <<parameters>>.margin + <<parameters>>.chassis_hole_spacing / 2
  expr: Constraints[15] = <<parameters>>.arduino_hole3_offset_y - 0.5 mm
  expr: Constraints[24] = <<parameters>>.wall_depth
  expr: Constraints[25] = <<parameters>>.wall_depth
  expr: Constraints[26] = <<parameters>>.wall_depth
  expr: Constraints[27] = <<parameters>>.margin
  expr: Constraints[2] = <<parameters>>.arduino_length
  expr: Constraints[4] = <<parameters>>.margin + <<parameters>>.wall_depth + 0.25 mm
  expr: Constraints[9] = <<parameters>>.wall_depth + <<parameters>>.margin + 1.75 mm
  sketch-geometry (10):
    g0: GeomPoint [constr] X=26.67 Y=-65.54 Z=0
    g1: GeomPoint [constr] X=26.67 Y=3.04 Z=0
    g2: LineSegment StartX=-30.825 StartY=-68.49 StartZ=0 EndX=30.825 EndY=-68.49 EndZ=0
    g3: LineSegment StartX=-30.825 StartY=7.49 StartZ=0 EndX=-30.825 EndY=-68.49 EndZ=0
    g4: LineSegment StartX=-30.825 StartY=7.49 StartZ=0 EndX=30.825 EndY=7.49 EndZ=0
    g5: LineSegment StartX=30.825 StartY=7.49 StartZ=0 EndX=30.825 EndY=-68.49 EndZ=0
    g6: LineSegment StartX=-28.325 StartY=4.99 StartZ=0 EndX=28.325 EndY=4.99 EndZ=0
    g7: LineSegment StartX=28.325 StartY=4.99 StartZ=0 EndX=28.325 EndY=-65.74 EndZ=0
    g8: LineSegment StartX=28.325 StartY=-65.74 StartZ=0 EndX=-28.325 EndY=-65.74 EndZ=0
    g9: LineSegment StartX=-28.325 StartY=-65.74 StartZ=0 EndX=-28.325 EndY=4.99 EndZ=0
  constraints (28):
    c: DistanceX(g-1,g0) = 26.67
    c: Vertical(g1,g0)
    c: DistanceY(g0,g1) = 68.58
    c: Horizontal(g2)
    c: DistanceY(g2,g0) = 2.95
    c: Vertical(g3)
    c: Coincident(g2,g3)
    c: Horizontal(g4,g3)
    c: Coincident(g4,g3)
    c: DistanceY(g1,g4) = 4.45
    c: DistanceX(g3,g-1) = 30.825
    c: DistanceX(g-1,g4) = 30.825
    c: Coincident(g5,g4)
    c: Coincident(g5,g2)
    c: Vertical(g5)
    c: DistanceY(g0,g-1) = 65.54
    c: Coincident(g6,g7)
    c: Coincident(g7,g8)
    c: Coincident(g8,g9)
    c: Coincident(g9,g6)
    c: Horizontal(g6)
    c: Horizontal(g8)
    c: Vertical(g7)
    c: Vertical(g9)
    c: DistanceX(g3,g6) = 2.5
    c: DistanceY(g6,g3) = 2.5
    c: DistanceX(g6,g4) = 2.5
    c: DistanceY(g7,g0) = 0.2
FEATURE [PartDesign::Pad] Pad012  label="ArduinoBoxLidWalls"
  BaseFeature = -> Pad011
  Direction = (0,0,1)
  Length = 3.6
  Length2 = 10
  Profile = -> Sketch019
  ReferenceAxis = -> Sketch019 [N_Axis]
  Reversed = true
  Suppressed = false
  Type = 0
FEATURE [Sketcher::SketchObject] Sketch020  label="ArduinoBoxLidConnectorsSketch"
  ArcFitTolerance = 0
  AttachmentSupport = -> [XY_Plane011]
  FullyConstrained = true
  MakeInternals = false
  MapMode = 5
  expr: Constraints[0] = <<parameters>>.arduino_width / 2
  expr: Constraints[18] = <<parameters>>.margin
  expr: Constraints[19] = <<parameters>>.margin + <<parameters>>.wall_depth + 0.25 mm
  expr: Constraints[1] = <<parameters>>.arduino_hole3_offset_y - 0.5 mm
  expr: Constraints[22] = <<parameters>>.arduino_power_offsetx_start + 0.5 mm
  expr: Constraints[23] = <<parameters>>.arduino_power_offsetx_end - 0.5 mm
  expr: Constraints[24] = <<parameters>>.arduino_usb_offsetx_start + 0.5 mm
  expr: Constraints[25] = <<parameters>>.arduino_usb_offsetx_end - 0.5 mm
  sketch-geometry (9):
    g0: GeomPoint [constr] X=26.67 Y=-65.54 Z=0
    g1: LineSegment StartX=-17.145 StartY=-65.74 StartZ=0 EndX=-5.715 EndY=-65.74 EndZ=0
    g2: LineSegment StartX=-5.715 StartY=-65.74 StartZ=0 EndX=-5.715 EndY=-68.49 EndZ=0
    g3: LineSegment StartX=-5.715 StartY=-68.49 StartZ=0 EndX=-17.145 EndY=-68.49 EndZ=0
    g4: LineSegment StartX=-17.145 StartY=-68.49 StartZ=0 EndX=-17.145 EndY=-65.74 EndZ=0
    g5: LineSegment StartX=14.605 StartY=-68.49 StartZ=0 EndX=22.995 EndY=-68.49 EndZ=0
    g6: LineSegment StartX=22.995 StartY=-68.49 StartZ=0 EndX=22.995 EndY=-65.74 EndZ=0
    g7: LineSegment StartX=22.995 StartY=-65.74 StartZ=0 EndX=14.605 EndY=-65.74 EndZ=0
    g8: LineSegment StartX=14.605 StartY=-65.74 StartZ=0 EndX=14.605 EndY=-68.49 EndZ=0
  constraints (26):
    c: DistanceX(g-1,g0) = 26.67
    c: DistanceY(g0,g-1) = 65.54
    c: Coincident(g1,g2)
    c: Coincident(g2,g3)
    c: Coincident(g3,g4)
    c: Coincident(g4,g1)
    c: Horizontal(g1)
    c: Horizontal(g3)
    c: Vertical(g2)
    c: Vertical(g4)
    c: Coincident(g5,g6)
    c: Coincident(g6,g7)
    c: Coincident(g7,g8)
    c: Coincident(g8,g5)
    c: Horizontal(g5)
    c: Horizontal(g7)
    c: Vertical(g6)
    c: Vertical(g8)
    c: DistanceY(g6,g0) = 0.2
    c: DistanceY(g5,g0) = 2.95
    c: Horizontal(g1,g7)
    c: Horizontal(g2,g5)
    c: DistanceX(g6,g0) = 3.675
    c: DistanceX(g7,g0) = 12.065
    c: DistanceX(g1,g0) = 32.385
    c: DistanceX(g1,g0) = 43.815
FEATURE [PartDesign::Pad] Pad013  label="ArduinoBoxLidConnectors"
  BaseFeature = -> Pad012
  Direction = (0,0,1)
  Length = 11.35
  Length2 = 10
  Profile = -> Sketch020
  ReferenceAxis = -> Sketch020 [N_Axis]
  Reversed = true
  Suppressed = false
  Type = 0
  expr: Length = 3.6 mm + 7.75 mm
FEATURE [PartDesign::Fillet] Fillet005  label="ArduinoBoxLidEdgeSmoothing"
  Base = -> Pad013 [Edge39,Edge40,Edge42,Edge41,Edge36,Edge35,Edge37,Edge38,Edge46,Edge43,Edge44,Edge31,Edge32,Edge34,Edge33,Edge27,Edge28,Edge30,Edge29,Edge63,Edge135,Edge137,Edge69,Edge142,Edge122,Edge67,Edge57]
  BaseFeature = -> Pad013
  Radius = 1
  SupportTransform = false
  Suppressed = false
  UseAllEdges = false
FEATURE [PartDesign::Body] Body005  label="ArduinoBoxLidBody"
  AllowCompound = false
  Group = -> [Sketch018,Pad011,Sketch019,Pad012,Sketch020,Pad013,Fillet005]
  Origin = -> Origin011
  Tip = -> Fillet005
FEATURE [App::Part] Part005  label="ArduinoBoxLid"
  Group = -> [Body005]
  Origin = -> Origin010
  Placement = pos=(0,0,30.3) rot=(0,0,1;0rad)
FEATURE [Sketcher::SketchObject] Sketch021  label="GPSCableWrapCapSketch"
  ArcFitTolerance = 0
  AttachmentSupport = -> [XY_Plane013]
  FullyConstrained = true
  MakeInternals = false
  MapMode = 5
  expr: Constraints[10] = <<parameters>>.plate_hole_spacing - <<parameters>>.gps_wrap_margin
  expr: Constraints[11] = <<parameters>>.plate_hole_spacing - <<parameters>>.gps_wrap_margin
  expr: Constraints[12] = <<parameters>>.gps_antenna_bolt_diameter
  expr: Constraints[13] = <<parameters>>.gps_antenna_bolt_diameter
  expr: Constraints[16] = <<parameters>>.gps_antenna_hole_spacing / 2
  expr: Constraints[17] = <<parameters>>.gps_antenna_hole_spacing / 2
  expr: Constraints[8] = <<parameters>>.gps_wrap_width / 2
  expr: Constraints[9] = <<parameters>>.gps_wrap_width / 2
  sketch-geometry (6):
    g0: LineSegment StartX=-30 StartY=47 StartZ=0 EndX=30 EndY=47 EndZ=0
    g1: LineSegment StartX=30 StartY=47 StartZ=0 EndX=30 EndY=-47 EndZ=0
    g2: LineSegment StartX=30 StartY=-47 StartZ=0 EndX=-30 EndY=-47 EndZ=0
    g3: LineSegment StartX=-30 StartY=-47 StartZ=0 EndX=-30 EndY=47 EndZ=0
    g4: Circle CenterX=0 CenterY=34 CenterZ=0 NormalX=0 NormalY=0 NormalZ=1 AngleXU=0 Radius=2.25
    g5: Circle CenterX=0 CenterY=-34 CenterZ=0 NormalX=0 NormalY=0 NormalZ=1 AngleXU=0 Radius=2.25
  constraints (18):
    c: Coincident(g0,g1)
    c: Coincident(g1,g2)
    c: Coincident(g2,g3)
    c: Coincident(g3,g0)
    c: Horizontal(g0)
    c: Horizontal(g2)
    c: Vertical(g1)
    c: Vertical(g3)
    c: DistanceX(g0,g-1) = 30
    c: DistanceX(g-1,g0) = 30
    c: DistanceY(g-1,g0) = 47
    c: DistanceY(g1,g-1) = 47
    c: Diameter(g4) = 4.5
    c: Diameter(g5) = 4.5
    c: Vertical(g-1,g5)
    c: Vertical(g-1,g4)
    c: DistanceY(g5,g-1) = 34
    c: DistanceY(g-1,g4) = 34
FEATURE [PartDesign::Pad] Pad014  label="GPSCableWrapCap"
  Direction = (0,0,1)
  Length = 5
  Length2 = 10
  Profile = -> Sketch021
  ReferenceAxis = -> Sketch021 [N_Axis]
  Suppressed = false
  Type = 0
FEATURE [Sketcher::SketchObject] Sketch022  label="GPSCableWrapSpoolSketch"
  ArcFitTolerance = 0
  AttachmentSupport = -> [Pad014]
  FullyConstrained = true
  MakeInternals = false
  MapMode = 5
  Placement = pos=(0,0,5) rot=(0,0,1;0rad)
  expr: Constraints[20] = <<parameters>>.gps_wrap_width / 2 - <<parameters>>.gps_wrap_post_size
  expr: Constraints[21] = <<parameters>>.gps_wrap_width / 2 - <<parameters>>.gps_wrap_post_size
  expr: Constraints[22] = <<parameters>>.plate_hole_spacing - <<parameters>>.gps_wrap_margin - <<parameters>>.gps_wrap_post_size
  expr: Constraints[23] = <<parameters>>.gps_wrap_post_size
  expr: Constraints[24] = <<parameters>>.plate_hole_spacing - <<parameters>>.gps_wrap_margin - <<parameters>>.gps_wrap_post_size
  sketch-geometry (12):
    g0: LineSegment StartX=-17.5 StartY=47 StartZ=0 EndX=-17.5 EndY=34.5 EndZ=0
    g1: LineSegment StartX=-17.5 StartY=34.5 StartZ=0 EndX=-30 EndY=34.5 EndZ=0
    g2: LineSegment StartX=30 StartY=34.5 StartZ=0 EndX=17.5 EndY=34.5 EndZ=0
    g3: LineSegment StartX=17.5 StartY=34.5 StartZ=0 EndX=17.5 EndY=47 EndZ=0
    g4: LineSegment StartX=-30 StartY=-34.5 StartZ=0 EndX=-17.5 EndY=-34.5 EndZ=0
    g5: LineSegment StartX=-17.5 StartY=-34.5 StartZ=0 EndX=-17.5 EndY=-47 EndZ=0
    g6: LineSegment StartX=17.5 StartY=-34.5 StartZ=0 EndX=30 EndY=-34.5 EndZ=0
    g7: LineSegment StartX=17.5 StartY=-47 StartZ=0 EndX=17.5 EndY=-34.5 EndZ=0
    g8: ArcOfCircle CenterX=-17.5 CenterY=34.5 CenterZ=0 NormalX=0 NormalY=0 NormalZ=1 AngleXU=0 Radius=12.5 StartAngle=1.5708 EndAngle=3.14159
    g9: ArcOfCircle CenterX=17.5 CenterY=34.5 CenterZ=0 NormalX=0 NormalY=0 NormalZ=1 AngleXU=0 Radius=12.5 StartAngle=0 EndAngle=1.5708
    g10: ArcOfCircle CenterX=17.5 CenterY=-34.5 CenterZ=0 NormalX=0 NormalY=0 NormalZ=1 AngleXU=0 Radius=12.5 StartAngle=4.71239 EndAngle=6.28319
    g11: ArcOfCircle CenterX=-17.5 CenterY=-34.5 CenterZ=0 NormalX=0 NormalY=0 NormalZ=1 AngleXU=0 Radius=12.5 StartAngle=3.14159 EndAngle=4.71239
  constraints (37):
    c: Coincident(g0,g1)
    c: Horizontal(g1)
    c: Vertical(g0)
    c: Coincident(g2,g3)
    c: Horizontal(g2)
    c: Vertical(g3)
    c: Coincident(g4,g5)
    c: Horizontal(g4)
    c: Vertical(g5)
    c: Coincident(g7,g6)
    c: Horizontal(g6)
    c: Vertical(g7)
    c: Horizontal(g3,g0)
    c: Horizontal(g0,g2)
    c: Vertical(g4,g1)
    c: Vertical(g4,g0)
    c: Vertical(g6,g2)
    c: Vertical(g6,g2)
    c: Horizontal(g6,g4)
    c: Horizontal(g5,g7)
    c: DistanceX(g0,g-1) = 17.5
    c: DistanceX(g-1,g3) = 17.5
    c: DistanceY(g-1,g1) = 34.5
    c: DistanceX(g1,g0) = 12.5
    c: DistanceY(g4,g-1) = 34.5
    c: Coincident(g8,g0)
    c: Coincident(g8,g1)
    c: Coincident(g8,g0)
    c: Coincident(g9,g2)
    c: Coincident(g9,g2)
    c: PointOnObject(g9,g3)
    c: Coincident(g10,g6)
    c: Coincident(g10,g7)
    c: Coincident(g10,g6)
    c: Coincident(g11,g4)
    c: Coincident(g11,g4)
    c: Coincident(g11,g5)
FEATURE [PartDesign::Pad] Pad015  label="GPSCableWrapSpool"
  BaseFeature = -> Pad014
  Direction = (0,0,1)
  Length = 20
  Length2 = 10
  Profile = -> Sketch022
  ReferenceAxis = -> Sketch022 [N_Axis]
  Suppressed = false
  Type = 0
FEATURE [Sketcher::SketchObject] Sketch023  label="GPSCableWrapPostSketch"
  ArcFitTolerance = 0
  AttachmentSupport = -> [Pad015]
  FullyConstrained = true
  MakeInternals = false
  MapMode = 5
  Placement = pos=(0,0,25) rot=(0,0,1;0rad)
  expr: Constraints[32] = <<parameters>>.gps_wrap_width / 2
  expr: Constraints[33] = <<parameters>>.gps_wrap_width / 2
  expr: Constraints[36] = <<parameters>>.gps_wrap_post_size
  expr: Constraints[37] = <<parameters>>.gps_wrap_post_size
  expr: Constraints[38] = <<parameters>>.gps_wrap_post_size
  expr: Constraints[39] = <<parameters>>.plate_hole_spacing - <<parameters>>.gps_wrap_margin
  expr: Constraints[40] = <<parameters>>.plate_hole_spacing - <<parameters>>.gps_wrap_margin
  expr: Constraints[45] = <<parameters>>.gps_wrap_post_size
  sketch-geometry (16):
    g0: LineSegment StartX=-30 StartY=47 StartZ=0 EndX=-17.5 EndY=47 EndZ=0
    g1: LineSegment StartX=-17.5 StartY=47 StartZ=0 EndX=-17.5 EndY=34.5 EndZ=0
    g2: LineSegment StartX=-17.5 StartY=34.5 StartZ=0 EndX=-30 EndY=34.5 EndZ=0
    g3: LineSegment StartX=-30 StartY=34.5 StartZ=0 EndX=-30 EndY=47 EndZ=0
    g4: LineSegment StartX=17.5 StartY=47 StartZ=0 EndX=30 EndY=47 EndZ=0
    g5: LineSegment StartX=30 StartY=47 StartZ=0 EndX=30 EndY=34.5 EndZ=0
    g6: LineSegment StartX=30 StartY=34.5 StartZ=0 EndX=17.5 EndY=34.5 EndZ=0
    g7: LineSegment StartX=17.5 StartY=34.5 StartZ=0 EndX=17.5 EndY=47 EndZ=0
    g8: LineSegment StartX=17.5 StartY=-34.5 StartZ=0 EndX=30 EndY=-34.5 EndZ=0
    g9: LineSegment StartX=30 StartY=-34.5 StartZ=0 EndX=30 EndY=-47 EndZ=0
    g10: LineSegment StartX=30 StartY=-47 StartZ=0 EndX=17.5 EndY=-47 EndZ=0
    g11: LineSegment StartX=17.5 StartY=-47 StartZ=0 EndX=17.5 EndY=-34.5 EndZ=0
    g12: LineSegment StartX=-30 StartY=-34.5 StartZ=0 EndX=-17.5 EndY=-34.5 EndZ=0
    g13: LineSegment StartX=-17.5 StartY=-34.5 StartZ=0 EndX=-17.5 EndY=-47 EndZ=0
    g14: LineSegment StartX=-17.5 StartY=-47 StartZ=0 EndX=-30 EndY=-47 EndZ=0
    g15: LineSegment StartX=-30 StartY=-47 StartZ=0 EndX=-30 EndY=-34.5 EndZ=0
  constraints (48):
    c: Coincident(g0,g1)
    c: Coincident(g1,g2)
    c: Coincident(g2,g3)
    c: Coincident(g3,g0)
    c: Horizontal(g0)
    c: Horizontal(g2)
    c: Vertical(g1)
    c: Vertical(g3)
    c: Coincident(g4,g5)
    c: Coincident(g5,g6)
    c: Coincident(g6,g7)
    c: Coincident(g7,g4)
    c: Horizontal(g4)
    c: Horizontal(g6)
    c: Vertical(g5)
    c: Vertical(g7)
    c: Coincident(g8,g9)
    c: Coincident(g9,g10)
    c: Coincident(g10,g11)
    c: Coincident(g11,g8)
    c: Horizontal(g8)
    c: Horizontal(g10)
    c: Vertical(g9)
    c: Vertical(g11)
    c: Coincident(g12,g13)
    c: Coincident(g13,g14)
    c: Coincident(g14,g15)
    c: Coincident(g15,g12)
    c: Horizontal(g12)
    c: Horizontal(g14)
    c: Vertical(g13)
    c: Vertical(g15)
    c: DistanceX(g0,g-1) = 30
    c: DistanceX(g-1,g4) = 30
    c: Horizontal(g0,g4)
    c: Horizontal(g1,g6)
    c: DistanceX(g0,g0) = 12.5
    c: DistanceX(g4,g4) = 12.5
    c: DistanceY(g2,g0) = 12.5
    c: DistanceY(g-1,g0) = 47
    c: DistanceY(g14,g-1) = 47
    c: Horizontal(g12,g8)
    c: Horizontal(g13,g10)
    c: Vertical(g12,g1)
    c: Vertical(g8,g6)
    c: DistanceY(g14,g12) = 12.5
    c: Vertical(g12,g2)
    c: Vertical(g8,g5)
FEATURE [PartDesign::Pad] Pad016  label="GPSCableWrapPost"
  BaseFeature = -> Pad015
  Direction = (0,0,1)
  Length = 10
  Length2 = 10
  Profile = -> Sketch023
  ReferenceAxis = -> Sketch023 [N_Axis]
  Suppressed = false
  Type = 0
FEATURE [PartDesign::Fillet] Fillet006  label="GPSCableWrapSpoolSmoothing"
  Base = -> Pad016 [Face5,Face25,Face34,Face7,Face10,Face36,Face35,Face9]
  BaseFeature = -> Pad016
  Radius = 1.5
  SupportTransform = false
  Suppressed = false
  UseAllEdges = false
FEATURE [Sketcher::SketchObject] Sketch024  label="GPSCableWrapFeetSketch"
  ArcFitTolerance = 0
  AttachmentSupport = -> [Fillet006]
  FullyConstrained = true
  MakeInternals = false
  MapMode = 5
  Placement = pos=(0,0,35) rot=(0,0,1;0rad)
  expr: Constraints[20] = <<parameters>>.gps_wrap_width / 2
  expr: Constraints[21] = <<parameters>>.gps_wrap_width / 2
  expr: Constraints[24] = <<parameters>>.gps_wrap_post_size
  expr: Constraints[25] = <<parameters>>.gps_wrap_post_size
  expr: Constraints[26] = <<parameters>>.gps_wrap_post_size
  expr: Constraints[27] = <<parameters>>.plate_hole_spacing - <<parameters>>.gps_wrap_margin
  expr: Constraints[28] = <<parameters>>.plate_hole_spacing - <<parameters>>.gps_wrap_margin
  expr: Constraints[33] = <<parameters>>.gps_wrap_post_size
  expr: Constraints[36] = <<parameters>>.plate_bolt_diameter
  expr: Constraints[37] = <<parameters>>.plate_bolt_diameter
  expr: Constraints[38] = <<parameters>>.plate_bolt_diameter
  expr: Constraints[39] = <<parameters>>.plate_bolt_diameter
  expr: Constraints[40] = <<parameters>>.plate_hole_spacing
  expr: Constraints[41] = <<parameters>>.plate_hole_spacing / 2
  expr: Constraints[43] = <<parameters>>.plate_hole_spacing / 2
  expr: Constraints[47] = <<parameters>>.plate_hole_spacing
  sketch-geometry (32):
    g0: LineSegment StartX=-17.5 StartY=47 StartZ=0 EndX=-17.5 EndY=34.5 EndZ=0
    g1: LineSegment StartX=-17.5 StartY=34.5 StartZ=0 EndX=-30 EndY=34.5 EndZ=0
    g2: LineSegment StartX=-30 StartY=34.5 StartZ=0 EndX=-30 EndY=47 EndZ=0
    g3: LineSegment StartX=30 StartY=47 StartZ=0 EndX=30 EndY=34.5 EndZ=0
    g4: LineSegment StartX=30 StartY=34.5 StartZ=0 EndX=17.5 EndY=34.5 EndZ=0
    g5: LineSegment StartX=17.5 StartY=34.5 StartZ=0 EndX=17.5 EndY=47 EndZ=0
    g6: LineSegment StartX=17.5 StartY=-34.5 StartZ=0 EndX=30 EndY=-34.5 EndZ=0
    g7: LineSegment StartX=30 StartY=-34.5 StartZ=0 EndX=30 EndY=-47 EndZ=0
    g8: LineSegment StartX=17.5 StartY=-47 StartZ=0 EndX=17.5 EndY=-34.5 EndZ=0
    g9: LineSegment StartX=-30 StartY=-34.5 StartZ=0 EndX=-17.5 EndY=-34.5 EndZ=0
    g10: LineSegment StartX=-17.5 StartY=-34.5 StartZ=0 EndX=-17.5 EndY=-47 EndZ=0
    g11: LineSegment StartX=-30 StartY=-47 StartZ=0 EndX=-30 EndY=-34.5 EndZ=0
    g12: Circle CenterX=-25 CenterY=50 CenterZ=0 NormalX=0 NormalY=0 NormalZ=1 AngleXU=0 Radius=1.6
    g13: Circle CenterX=25 CenterY=50 CenterZ=0 NormalX=0 NormalY=0 NormalZ=1 AngleXU=0 Radius=1.6
    g14: Circle CenterX=-25 CenterY=-50 CenterZ=0 NormalX=0 NormalY=0 NormalZ=1 AngleXU=0 Radius=1.6
    g15: Circle CenterX=25 CenterY=-50 CenterZ=0 NormalX=0 NormalY=0 NormalZ=1 AngleXU=0 Radius=1.6
    g16: LineSegment StartX=-30 StartY=47 StartZ=0 EndX=-30 EndY=50 EndZ=0
    g17: LineSegment StartX=30 StartY=47 StartZ=0 EndX=30 EndY=50 EndZ=0
    g18: ArcOfCircle CenterX=25 CenterY=50 CenterZ=0 NormalX=0 NormalY=0 NormalZ=1 AngleXU=0 Radius=5 StartAngle=0 EndAngle=3.14159
    g19: ArcOfCircle CenterX=-25 CenterY=50 CenterZ=0 NormalX=0 NormalY=0 NormalZ=1 AngleXU=0 Radius=5 StartAngle=5e-16 EndAngle=3.14159
    g20: LineSegment StartX=-20 StartY=50 StartZ=0 EndX=-20 EndY=47 EndZ=0
    g21: LineSegment StartX=-20 StartY=47 StartZ=0 EndX=-17.5 EndY=47 EndZ=0
    g22: LineSegment StartX=20 StartY=50 StartZ=0 EndX=20 EndY=47 EndZ=0
    g23: LineSegment StartX=17.5 StartY=47 StartZ=0 EndX=20 EndY=47 EndZ=0
    g24: LineSegment StartX=-30 StartY=-47 StartZ=0 EndX=-30 EndY=-50 EndZ=0
    g25: LineSegment StartX=30 StartY=-47 StartZ=0 EndX=30 EndY=-50 EndZ=0
    g26: ArcOfCircle CenterX=-25 CenterY=-50 CenterZ=0 NormalX=0 NormalY=0 NormalZ=1 AngleXU=0 Radius=5 StartAngle=3.14159 EndAngle=6.28319
    g27: ArcOfCircle CenterX=25 CenterY=-50 CenterZ=0 NormalX=0 NormalY=0 NormalZ=1 AngleXU=0 Radius=5 StartAngle=3.14159 EndAngle=6.28319
    g28: LineSegment StartX=-20 StartY=-50 StartZ=0 EndX=-20 EndY=-47 EndZ=0
    g29: LineSegment StartX=-20 StartY=-47 StartZ=0 EndX=-17.5 EndY=-47 EndZ=0
    g30: LineSegment StartX=17.5 StartY=-47 StartZ=0 EndX=20 EndY=-47 EndZ=0
    g31: LineSegment StartX=20 StartY=-47 StartZ=0 EndX=20 EndY=-50 EndZ=0
  constraints (96):
    c: Coincident(g0,g1)
    c: Coincident(g1,g2)
    c: Horizontal(g1)
    c: Vertical(g0)
    c: Vertical(g2)
    c: Coincident(g3,g4)
    c: Coincident(g4,g5)
    c: Horizontal(g4)
    c: Vertical(g3)
    c: Vertical(g5)
    c: Coincident(g6,g7)
    c: Coincident(g8,g6)
    c: Horizontal(g6)
    c: Vertical(g7)
    c: Vertical(g8)
    c: Coincident(g9,g10)
    c: Coincident(g11,g9)
    c: Horizontal(g9)
    c: Vertical(g10)
    c: Vertical(g11)
    c: DistanceX(g2,g-1) = 30
    c: DistanceX(g-1,g3) = 30
    c: Horizontal(g0,g5)
    c: Horizontal(g0,g4)
    c: DistanceX(g2,g0) = 12.5
    c: DistanceX(g5,g3) = 12.5
    c: DistanceY(g1,g2) = 12.5
    c: DistanceY(g-1,g2) = 47
    c: DistanceY(g11,g-1) = 47
    c: Horizontal(g9,g6)
    c: Horizontal(g10,g8)
    c: Vertical(g9,g0)
    c: Vertical(g6,g4)
    c: DistanceY(g11,g9) = 12.5
    c: Vertical(g9,g1)
    c: Vertical(g6,g3)
    c: Diameter(g12) = 3.2
    c: Diameter(g13) = 3.2
    c: Diameter(g14) = 3.2
    c: Diameter(g15) = 3.2
    c: DistanceY(g-1,g12) = 50
    c: DistanceX(g12,g-1) = 25
    c: Horizontal(g13,g12)
    c: DistanceX(g-1,g13) = 25
    c: Vertical(g12,g14)
    c: Vertical(g15,g13)
    c: Horizontal(g15,g14)
    c: DistanceY(g14,g-1) = 50
    c: Horizontal(g0,g2)
    c: Horizontal(g3,g5)
    c: Coincident(g16,g2)
    c: Vertical(g16)
    c: Horizontal(g16,g12)
    c: Coincident(g17,g3)
    c: Vertical(g17)
    c: Horizontal(g17,g13)
    c: Coincident(g18,g13)
    c: Coincident(g18,g17)
    c: Horizontal(g18,g13)
    c: Coincident(g19,g12)
    c: Coincident(g19,g16)
    c: Horizontal(g19,g12)
    c: Coincident(g20,g19)
    c: Vertical(g20)
    c: Horizontal(g20,g0)
    c: Coincident(g21,g20)
    c: Coincident(g21,g0)
    c: Coincident(g22,g18)
    c: Vertical(g22)
    c: Coincident(g23,g5)
    c: Coincident(g23,g22)
    c: Horizontal(g23)
    c: Horizontal(g10,g11)
    c: Horizontal(g7,g8)
    c: Coincident(g24,g11)
    c: Vertical(g24)
    c: Coincident(g25,g7)
    c: Vertical(g25)
    c: Horizontal(g15,g25)
    c: Horizontal(g24,g14)
    c: Coincident(g26,g14)
    c: Coincident(g26,g24)
    c: Coincident(g27,g15)
    c: Coincident(g27,g25)
    c: Horizontal(g27,g15)
    c: Horizontal(g14,g26)
    c: Coincident(g28,g26)
    c: Vertical(g28)
    c: Coincident(g29,g28)
    c: Coincident(g29,g10)
    c: Horizontal(g29)
    c: Coincident(g30,g8)
    c: Horizontal(g30)
    c: Coincident(g31,g30)
    c: Coincident(g31,g27)
    c: Vertical(g31)
FEATURE [PartDesign::Pad] Pad017  label="GPSCableWrapFeet"
  BaseFeature = -> Fillet006
  Direction = (0,0,1)
  Length = 5
  Length2 = 10
  Profile = -> Sketch024
  ReferenceAxis = -> Sketch024 [N_Axis]
  Suppressed = false
  Type = 0
FEATURE [PartDesign::Fillet] Fillet007  label="GPSCableWrapFeetSmoothing"
  Base = -> Pad017 [Edge231,Edge224,Edge254,Edge255]
  BaseFeature = -> Pad017
  Radius = 1
  SupportTransform = false
  Suppressed = false
  UseAllEdges = false
FEATURE [PartDesign::Body] Body006  label="GPSCableWrapBody"
  AllowCompound = false
  Group = -> [Sketch021,Pad014,Sketch022,Pad015,Sketch023,Pad016,Fillet006,Sketch024,Pad017,Fillet007]
  Origin = -> Origin013
  Tip = -> Fillet007
FEATURE [App::Part] Part006  label="GPSCableWrap"
  Group = -> [Body006]
  Origin = -> Origin012
FEATURE [Sketcher::SketchObject] Sketch025
  ArcFitTolerance = 0
  AttachmentSupport = -> [XZ_Plane015]
  FullyConstrained = true
  MakeInternals = false
  MapMode = 5
  Placement = pos=(0,0,0) rot=(1,0,0;1.5708rad)
  sketch-geometry (3):
    g0: LineSegment StartX=0 StartY=0 StartZ=0 EndX=0 EndY=45 EndZ=0
    g1: LineSegment StartX=0 StartY=0 StartZ=0 EndX=16.38 EndY=0 EndZ=0
    g2: LineSegment StartX=0 StartY=45 StartZ=0 EndX=16.38 EndY=0 EndZ=0
  constraints (8):
    c: Coincident(g0,g-1)
    c: PointOnObject(g0,g-2)
    c: Coincident(g1,g0)
    c: PointOnObject(g1,g-1)
    c: DistanceY(g0,g0) = 45
    c: DistanceX(g0,g1) = 16.38
    c: Coincident(g2,g0)
    c: Coincident(g2,g1)
FEATURE [PartDesign::Pad] Pad018
  Direction = (0,-1,2e-16)
  Length = 158.75
  Length2 = 10
  Placement = pos=(0,0,0) rot=(1,0,0;1.5708rad)
  Profile = -> Sketch025
  ReferenceAxis = -> Sketch025 [N_Axis]
  Suppressed = false
  Type = 0
FEATURE [Sketcher::SketchObject] Sketch026
  ArcFitTolerance = 0
  AttachmentSupport = -> [Pad018]
  FullyConstrained = true
  MakeInternals = false
  MapMode = 5
  Placement = pos=(0,0,0) rot=(1,0,0;3.14159rad)
  expr: Constraints[39] = 1 * 158.75 / 9
  expr: Constraints[40] = 2 * 158.75 / 9
  expr: Constraints[41] = 3 * 158.75 / 9
  expr: Constraints[42] = 4 * 158.75 / 9
  expr: Constraints[43] = 5 * 158.75 / 9
  expr: Constraints[44] = 6 * 158.75 / 9
  expr: Constraints[45] = 7 * 158.75 / 9
  expr: Constraints[46] = 8 * 158.75 / 9
  expr: Constraints[47] = 16.38
  sketch-geometry (16):
    g0: LineSegment StartX=3.5 StartY=35.2778 StartZ=0 EndX=16.38 EndY=35.2778 EndZ=0
    g1: LineSegment StartX=16.38 StartY=35.2778 StartZ=0 EndX=16.38 EndY=17.6389 EndZ=0
    g2: LineSegment StartX=16.38 StartY=17.6389 StartZ=0 EndX=3.5 EndY=17.6389 EndZ=0
    g3: LineSegment StartX=3.5 StartY=17.6389 StartZ=0 EndX=3.5 EndY=35.2778 EndZ=0
    g4: LineSegment StartX=3.5 StartY=141.111 StartZ=0 EndX=16.38 EndY=141.111 EndZ=0
    g5: LineSegment StartX=16.38 StartY=141.111 StartZ=0 EndX=16.38 EndY=123.472 EndZ=0
    g6: LineSegment StartX=16.38 StartY=123.472 StartZ=0 EndX=3.5 EndY=123.472 EndZ=0
    g7: LineSegment StartX=3.5 StartY=123.472 StartZ=0 EndX=3.5 EndY=141.111 EndZ=0
    g8: LineSegment StartX=3.5 StartY=105.833 StartZ=0 EndX=16.38 EndY=105.833 EndZ=0
    g9: LineSegment StartX=16.38 StartY=105.833 StartZ=0 EndX=16.38 EndY=88.1944 EndZ=0
    g10: LineSegment StartX=16.38 StartY=88.1944 StartZ=0 EndX=3.5 EndY=88.1944 EndZ=0
    g11: LineSegment StartX=3.5 StartY=88.1944 StartZ=0 EndX=3.5 EndY=105.833 EndZ=0
    g12: LineSegment StartX=3.5 StartY=70.5556 StartZ=0 EndX=16.38 EndY=70.5556 EndZ=0
    g13: LineSegment StartX=16.38 StartY=70.5556 StartZ=0 EndX=16.38 EndY=52.9167 EndZ=0
    g14: LineSegment StartX=16.38 StartY=52.9167 StartZ=0 EndX=3.5 EndY=52.9167 EndZ=0
    g15: LineSegment StartX=3.5 StartY=52.9167 StartZ=0 EndX=3.5 EndY=70.5556 EndZ=0
  constraints (48):
    c: Coincident(g0,g1)
    c: Coincident(g1,g2)
    c: Coincident(g2,g3)
    c: Coincident(g3,g0)
    c: Horizontal(g0)
    c: Horizontal(g2)
    c: Vertical(g1)
    c: Vertical(g3)
    c: Coincident(g4,g5)
    c: Coincident(g5,g6)
    c: Coincident(g6,g7)
    c: Coincident(g7,g4)
    c: Horizontal(g4)
    c: Horizontal(g6)
    c: Vertical(g5)
    c: Vertical(g7)
    c: Coincident(g8,g9)
    c: Coincident(g9,g10)
    c: Coincident(g10,g11)
    c: Coincident(g11,g8)
    c: Horizontal(g8)
    c: Horizontal(g10)
    c: Vertical(g9)
    c: Vertical(g11)
    c: Coincident(g12,g13)
    c: Coincident(g13,g14)
    c: Coincident(g14,g15)
    c: Coincident(g15,g12)
    c: Horizontal(g12)
    c: Horizontal(g14)
    c: Vertical(g13)
    c: Vertical(g15)
    c: Vertical(g0,g14)
    c: Vertical(g8,g6)
    c: Vertical(g10,g12)
    c: Vertical(g5,g8)
    c: Vertical(g9,g12)
    c: Vertical(g13,g0)
    c: DistanceX(g-1,g2) = 3.5
    c: DistanceY(g-1,g2) = 17.6389
    c: DistanceY(g-1,g0) = 35.2778
    c: DistanceY(g-1,g14) = 52.9167
    c: DistanceY(g-1,g12) = 70.5556
    c: DistanceY(g-1,g10) = 88.1944
    c: DistanceY(g-1,g8) = 105.833
    c: DistanceY(g-1,g6) = 123.472
    c: DistanceY(g-1,g4) = 141.111
    c: DistanceX(g-1,g1) = 16.38
FEATURE [PartDesign::Pocket] Pocket007
  BaseFeature = -> Pad018
  Direction = (0,0,1)
  Length = 45
  Length2 = 5
  Placement = pos=(0,0,0) rot=(1,0,0;1.5708rad)
  Profile = -> Sketch026
  ReferenceAxis = -> Sketch026 [N_Axis]
  Suppressed = false
  Type = 0
  expr: Length = 45
FEATURE [Sketcher::SketchObject] Sketch027
  ArcFitTolerance = 0
  AttachmentSupport = -> [Pocket007]
  FullyConstrained = true
  MakeInternals = false
  MapMode = 5
  Placement = pos=(0,-158.75,0) rot=(1,0,0;1.5708rad)
  sketch-geometry (4):
    g0: LineSegment StartX=0 StartY=45 StartZ=0 EndX=5 EndY=45 EndZ=0
    g1: LineSegment StartX=5 StartY=45 StartZ=0 EndX=5 EndY=40 EndZ=0
    g2: LineSegment StartX=5 StartY=40 StartZ=0 EndX=0 EndY=40 EndZ=0
    g3: LineSegment StartX=0 StartY=40 StartZ=0 EndX=0 EndY=45 EndZ=0
  constraints (12):
    c: Coincident(g0,g1)
    c: Coincident(g1,g2)
    c: Coincident(g2,g3)
    c: Coincident(g3,g0)
    c: Horizontal(g0)
    c: Horizontal(g2)
    c: Vertical(g1)
    c: Vertical(g3)
    c: PointOnObject(g0,g-2)
    c: DistanceY(g-1,g2) = 40
    c: DistanceX(g-1,g1) = 5
    c: DistanceY(g-1,g0) = 45
FEATURE [PartDesign::Pocket] Pocket008
  BaseFeature = -> Pocket007
  Direction = (0,1,-2e-16)
  Length = 200
  Length2 = 5
  Placement = pos=(0,0,0) rot=(1,0,0;1.5708rad)
  Profile = -> Sketch027
  ReferenceAxis = -> Sketch027 [N_Axis]
  Suppressed = false
  Type = 0
FEATURE [PartDesign::Body] Body007  label="BatteryShimBody"
  AllowCompound = false
  Group = -> [Sketch025,Pad018,Sketch026,Pocket007,Sketch027,Pocket008]
  Origin = -> Origin015
  Tip = -> Pocket008
FEATURE [App::Part] Part007  label="BatteryShim"
  Group = -> [Body007]
  Origin = -> Origin014
FEATURE [Mesh::Feature] OAK_D_Pro_enclosure  label="OAK-D-Pro"
  Placement = pos=(-48.5,11.2,26.75) rot=(1,0,0;1.5708rad)
  expr: .Placement.Base.z = 26.75 mm
FEATURE [Sketcher::SketchObject] Sketch028  label="CameraMountHullSketch"
  ArcFitTolerance = 0
  AttachmentSupport = -> [XY_Plane017]
  FullyConstrained = true
  MakeInternals = false
  MapMode = 5
  expr: Constraints[10] = <<parameters>>.camera_mount_width
  expr: Constraints[11] = <<parameters>>.camera_mount_depth
  expr: Constraints[8] = <<parameters>>.camera_mount_width / 2
  expr: Constraints[9] = <<parameters>>.camera_mount_depth / 2
  sketch-geometry (4):
    g0: LineSegment StartX=-55 StartY=16.3 StartZ=0 EndX=55 EndY=16.3 EndZ=0
    g1: LineSegment StartX=55 StartY=16.3 StartZ=0 EndX=55 EndY=-16.3 EndZ=0
    g2: LineSegment StartX=55 StartY=-16.3 StartZ=0 EndX=-55 EndY=-16.3 EndZ=0
    g3: LineSegment StartX=-55 StartY=-16.3 StartZ=0 EndX=-55 EndY=16.3 EndZ=0
  constraints (12):
    c: Coincident(g0,g1)
    c: Coincident(g1,g2)
    c: Coincident(g2,g3)
    c: Coincident(g3,g0)
    c: Horizontal(g0)
    c: Horizontal(g2)
    c: Vertical(g1)
    c: Vertical(g3)
    c: DistanceX(g0,g-1) = 55
    c: DistanceY(g-1,g0) = 16.3
    c: DistanceX(g0,g0) = 110
    c: DistanceY(g2,g0) = 32.6
FEATURE [PartDesign::Pad] Pad019  label="CameraMountHull"
  Direction = (0,0,1)
  Length = 46
  Length2 = 10
  Profile = -> Sketch028
  ReferenceAxis = -> Sketch028 [N_Axis]
  Suppressed = false
  Type = 0
  expr: Length = <<parameters>>.camera_mount_height
FEATURE [Sketcher::SketchObject] Sketch029  label="CameraBodyCutoutSketch"
  ArcFitTolerance = 0
  AttachmentSupport = -> [Pad019]
  FullyConstrained = true
  MakeInternals = false
  MapMode = 5
  Placement = pos=(0,0,46) rot=(0,0,1;0rad)
  expr: Constraints[1] = <<parameters>>.camera_width / 2 + <<parameters>>.margin + 2 mm
  expr: Constraints[26] = <<parameters>>.camera_hole_spacing / 2 + <<parameters>>.camera_bolt_diameter
  expr: Constraints[27] = <<parameters>>.camera_hole_spacing / 2 + <<parameters>>.camera_bolt_diameter
  expr: Constraints[28] = <<parameters>>.camera_bolt_diameter * 2
  expr: Constraints[29] = <<parameters>>.camera_bolt_diameter * 2
  expr: Constraints[31] = <<parameters>>.camera_attachment_thickness
  expr: Constraints[32] = <<parameters>>.camera_depth
  expr: Constraints[3] = <<parameters>>.camera_width / 2 + <<parameters>>.margin + 2 mm
  expr: Constraints[5] = <<parameters>>.camera_mount_depth / 2
  sketch-geometry (12):
    g0: LineSegment StartX=-50.7 StartY=16.3 StartZ=0 EndX=-42 EndY=16.3 EndZ=0
    g1: LineSegment StartX=42 StartY=16.3 StartZ=0 EndX=50.7 EndY=16.3 EndZ=0
    g2: LineSegment StartX=-50.7 StartY=16.3 StartZ=0 EndX=-50.7 EndY=-13.8 EndZ=0
    g3: LineSegment StartX=50.7 StartY=16.3 StartZ=0 EndX=50.7 EndY=-13.8 EndZ=0
    g4: LineSegment StartX=-42 StartY=16.3 StartZ=0 EndX=-42 EndY=11.3 EndZ=0
    g5: LineSegment StartX=-42 StartY=11.3 StartZ=0 EndX=-33 EndY=11.3 EndZ=0
    g6: LineSegment StartX=-33 StartY=11.3 StartZ=0 EndX=-33 EndY=16.3 EndZ=0
    g7: LineSegment StartX=42 StartY=16.3 StartZ=0 EndX=42 EndY=11.3 EndZ=0
    g8: LineSegment StartX=42 StartY=11.3 StartZ=0 EndX=33 EndY=11.3 EndZ=0
    g9: LineSegment StartX=33 StartY=11.3 StartZ=0 EndX=33 EndY=16.3 EndZ=0
    g10: LineSegment StartX=33 StartY=16.3 StartZ=0 EndX=-33 EndY=16.3 EndZ=0
    g11: LineSegment StartX=-50.7 StartY=-13.8 StartZ=0 EndX=50.7 EndY=-13.8 EndZ=0
  constraints (36):
    c: Horizontal(g0)
    c: DistanceX(g0,g-1) = 50.7
    c: Horizontal(g1)
    c: DistanceX(g-1,g1) = 50.7
    c: Horizontal(g1,g0)
    c: DistanceY(g-1,g0) = 16.3
    c: Coincident(g2,g0)
    c: Vertical(g2)
    c: Coincident(g3,g1)
    c: Vertical(g3)
    c: Coincident(g4,g0)
    c: Vertical(g4)
    c: Coincident(g5,g4)
    c: Horizontal(g5)
    c: Coincident(g6,g5)
    c: Vertical(g6)
    c: Coincident(g7,g1)
    c: Vertical(g7)
    c: Coincident(g8,g7)
    c: Horizontal(g8)
    c: Coincident(g9,g8)
    c: Vertical(g9)
    c: Coincident(g10,g9)
    c: Coincident(g10,g6)
    c: Horizontal(g10)
    c: Horizontal(g0,g6)
    c: DistanceX(g0,g-1) = 42
    c: DistanceX(g-1,g1) = 42
    c: DistanceX(g9,g1) = 9
    c: DistanceX(g0,g6) = 9
    c: Horizontal(g8,g5)
    c: DistanceY(g4,g0) = 5
    c: DistanceY(g2,g4) = 25.1
    c: Horizontal(g3,g2)
    c: Coincident(g11,g2)
    c: Coincident(g11,g3)
FEATURE [PartDesign::Pocket] Pocket009  label="CameraBodyCutout"
  BaseFeature = -> Pad019
  Direction = (0,0,-1)
  Length = 19.35
  Length2 = 5
  Profile = -> Sketch029
  ReferenceAxis = -> Sketch029 [N_Axis]
  Suppressed = false
  Type = 0
  expr: Length = <<parameters>>.camera_height / 2 + <<parameters>>.camera_bolt_diameter
FEATURE [Sketcher::SketchObject] Sketch030  label="CameraBoltHolesSketch"
  ArcFitTolerance = 0
  AttachmentSupport = -> [Pocket009]
  FullyConstrained = true
  MakeInternals = false
  MapMode = 5
  Placement = pos=(0,16.3,0) rot=(0,0.707107,0.707107;3.14159rad)
  expr: Constraints[0] = <<parameters>>.camera_hole_spacing / 2
  expr: Constraints[1] = <<parameters>>.camera_hole_spacing / 2
  expr: Constraints[3] = <<parameters>>.camera_mount_height - <<parameters>>.camera_bolt_diameter
  expr: Constraints[4] = <<parameters>>.camera_bolt_diameter
  expr: Constraints[5] = <<parameters>>.camera_bolt_diameter
  sketch-geometry (2):
    g0: Circle CenterX=-37.5 CenterY=41.5 CenterZ=0 NormalX=0 NormalY=0 NormalZ=1 AngleXU=0 Radius=2.25
    g1: Circle CenterX=37.5 CenterY=41.5 CenterZ=0 NormalX=0 NormalY=0 NormalZ=1 AngleXU=0 Radius=2.25
  constraints (6):
    c: DistanceX(g0,g-1) = 37.5
    c: DistanceX(g-1,g1) = 37.5
    c: Horizontal(g0,g1)
    c: DistanceY(g-1,g0) = 41.5
    c: Diameter(g0) = 4.5
    c: Diameter(g1) = 4.5
FEATURE [PartDesign::Pocket] Pocket010  label="CameraBoltHoles"
  BaseFeature = -> Pocket009
  Direction = (0,-1,2e-16)
  Length = 5
  Length2 = 5
  Profile = -> Sketch030
  ReferenceAxis = -> Sketch030 [N_Axis]
  Suppressed = false
  Type = 0
  expr: Length = <<parameters>>.camera_attachment_thickness
FEATURE [PartDesign::Fillet] Fillet008  label="CameraAttachmentSmoothing1"
  Base = -> Pocket010 [Edge48,Edge45,Edge42,Edge44]
  BaseFeature = -> Pocket010
  Radius = 3.5
  SupportTransform = false
  Suppressed = false
  UseAllEdges = false
  expr: Radius = <<parameters>>.camera_bolt_diameter - 1 mm
FEATURE [Sketcher::SketchObject] Sketch031  label="CameraOpeningSketch"
  ArcFitTolerance = 0
  AttachmentSupport = -> [Fillet008]
  FullyConstrained = true
  MakeInternals = false
  MapMode = 5
  Placement = pos=(0,0,46) rot=(0,0,1;0rad)
  expr: Constraints[10] = <<parameters>>.camera_width / 2
  expr: Constraints[11] = <<parameters>>.camera_mount_depth / 2 - (<<parameters>>.camera_mount_depth - <<parameters>>.camera_depth - <<parameters>>.camera_attachment_thickness)
  expr: Constraints[8] = <<parameters>>.camera_mount_depth / 2
  expr: Constraints[9] = <<parameters>>.camera_width / 2
  sketch-geometry (4):
    g0: LineSegment StartX=-48.5 StartY=-13.8 StartZ=0 EndX=48.5 EndY=-13.8 EndZ=0
    g1: LineSegment StartX=48.5 StartY=-13.8 StartZ=0 EndX=48.5 EndY=-16.3 EndZ=0
    g2: LineSegment StartX=48.5 StartY=-16.3 StartZ=0 EndX=-48.5 EndY=-16.3 EndZ=0
    g3: LineSegment StartX=-48.5 StartY=-16.3 StartZ=0 EndX=-48.5 EndY=-13.8 EndZ=0
  constraints (12):
    c: Coincident(g0,g1)
    c: Coincident(g1,g2)
    c: Coincident(g2,g3)
    c: Coincident(g3,g0)
    c: Horizontal(g0)
    c: Horizontal(g2)
    c: Vertical(g1)
    c: Vertical(g3)
    c: DistanceY(g2,g-1) = 16.3
    c: DistanceX(g0,g-1) = 48.5
    c: DistanceX(g-1,g0) = 48.5
    c: DistanceY(g0,g-1) = 13.8
FEATURE [PartDesign::Pocket] Pocket011  label="CameraOpening"
  BaseFeature = -> Fillet008
  Direction = (0,0,-1)
  Length = 14.4
  Length2 = 5
  Profile = -> Sketch031
  ReferenceAxis = -> Sketch031 [N_Axis]
  Suppressed = false
  Type = 0
  expr: Length = <<parameters>>.camera_height * 1 / 3 + <<parameters>>.camera_bolt_diameter
FEATURE [PartDesign::Fillet] Fillet009  label="CameraOpeningSmoothing"
  Base = -> Pocket011 [Edge78,Edge75]
  BaseFeature = -> Pocket011
  Radius = 2
  SupportTransform = false
  Suppressed = false
  UseAllEdges = false
FEATURE [PartDesign::Fillet] Fillet010  label="CameraAttachmentSmoothing2"
  Base = -> Fillet009 [Edge33,Edge29,Edge31,Edge27]
  BaseFeature = -> Fillet009
  Radius = 5
  SupportTransform = false
  Suppressed = false
  UseAllEdges = false
FEATURE [Sketcher::SketchObject] Sketch032  label="USBCYAdapterCutoutSketch"
  ArcFitTolerance = 0
  AttachmentSupport = -> [Fillet010]
  FullyConstrained = true
  MakeInternals = false
  MapMode = 5
  Placement = pos=(0,0,26.65) rot=(0,0,1;0rad)
  expr: Constraints[11] = <<parameters>>.camera_usbc_depth
  expr: Constraints[12] = <<parameters>>.camera_width / 2 - <<parameters>>.camera_usbc_offsetx_start
  expr: Constraints[13] = <<parameters>>.camera_width / 2 - <<parameters>>.camera_usbc_offsetx_end
  expr: Constraints[1] = <<parameters>>.camera_depth - (<<parameters>>.camera_mount_depth / 2 - <<parameters>>.camera_attachment_thickness) - 2.4 mm
  sketch-geometry (5):
    g0: GeomPoint [constr] X=0 Y=-11.4 Z=0
    g1: LineSegment StartX=0.7 StartY=1.4 StartZ=0 EndX=26.4 EndY=1.4 EndZ=0
    g2: LineSegment StartX=26.4 StartY=1.4 StartZ=0 EndX=26.4 EndY=-11.4 EndZ=0
    g3: LineSegment StartX=26.4 StartY=-11.4 StartZ=0 EndX=0.7 EndY=-11.4 EndZ=0
    g4: LineSegment StartX=0.7 StartY=-11.4 StartZ=0 EndX=0.7 EndY=1.4 EndZ=0
  constraints (14):
    c: PointOnObject(g0,g-2)
    c: DistanceY(g0,g-1) = 11.4
    c: Coincident(g1,g2)
    c: Coincident(g2,g3)
    c: Coincident(g3,g4)
    c: Coincident(g4,g1)
    c: Horizontal(g1)
    c: Horizontal(g3)
    c: Vertical(g2)
    c: Vertical(g4)
    c: Horizontal(g3,g0)
    c: DistanceY(g2,g1) = 12.8
    c: DistanceX(g0,g2) = 26.4
    c: DistanceX(g0,g3) = 0.7
FEATURE [PartDesign::Pocket] Pocket012  label="USBCYAdapterCutout"
  BaseFeature = -> Fillet010
  Direction = (0,0,-1)
  Length = 11.6
  Length2 = 5
  Profile = -> Sketch032
  ReferenceAxis = -> Sketch032 [N_Axis]
  Suppressed = false
  Type = 0
  expr: Length = 11.6
FEATURE [Sketcher::SketchObject] Sketch033  label="USBCCutoutSketch"
  ArcFitTolerance = 0
  AttachmentSupport = -> [Pocket012]
  FullyConstrained = true
  MakeInternals = false
  MapMode = 5
  Placement = pos=(0,0,15.05) rot=(0,0,1;0rad)
  expr: Constraints[19] = <<parameters>>.camera_usbc_depth
  expr: Constraints[21] = <<parameters>>.camera_width / 2 - <<parameters>>.camera_usbc_offsetx_end + 1.55 mm
  expr: Constraints[22] = <<parameters>>.camera_width / 2 - <<parameters>>.camera_usbc_offsetx_start - 1.52 mm
  expr: Constraints[23] = <<parameters>>.camera_width / 2 - (<<parameters>>.camera_usbc_offsetx_start + <<parameters>>.camera_usbc_offsetx_end) / 2 - 4.78 mm
  expr: Constraints[24] = <<parameters>>.camera_width / 2 - (<<parameters>>.camera_usbc_offsetx_start + <<parameters>>.camera_usbc_offsetx_end) / 2 + 4.73 mm
  expr: Constraints[25] = <<parameters>>.camera_depth - (<<parameters>>.camera_mount_depth / 2 - <<parameters>>.camera_attachment_thickness) - 2.4 mm
  sketch-geometry (9):
    g0: GeomPoint [constr] X=0 Y=-11.4 Z=0
    g1: LineSegment StartX=2.25 StartY=1.4 StartZ=0 EndX=8.77 EndY=1.4 EndZ=0
    g2: LineSegment StartX=8.77 StartY=1.4 StartZ=0 EndX=8.77 EndY=-11.4 EndZ=0
    g3: LineSegment StartX=8.77 StartY=-11.4 StartZ=0 EndX=2.25 EndY=-11.4 EndZ=0
    g4: LineSegment StartX=2.25 StartY=-11.4 StartZ=0 EndX=2.25 EndY=1.4 EndZ=0
    g5: LineSegment StartX=18.28 StartY=1.4 StartZ=0 EndX=24.88 EndY=1.4 EndZ=0
    g6: LineSegment StartX=24.88 StartY=1.4 StartZ=0 EndX=24.88 EndY=-11.4 EndZ=0
    g7: LineSegment StartX=24.88 StartY=-11.4 StartZ=0 EndX=18.28 EndY=-11.4 EndZ=0
    g8: LineSegment StartX=18.28 StartY=-11.4 StartZ=0 EndX=18.28 EndY=1.4 EndZ=0
  constraints (26):
    c: PointOnObject(g0,g-2)
    c: Coincident(g1,g2)
    c: Coincident(g2,g3)
    c: Coincident(g3,g4)
    c: Coincident(g4,g1)
    c: Horizontal(g1)
    c: Horizontal(g3)
    c: Vertical(g2)
    c: Vertical(g4)
    c: Coincident(g5,g6)
    c: Coincident(g6,g7)
    c: Coincident(g7,g8)
    c: Coincident(g8,g5)
    c: Horizontal(g5)
    c: Horizontal(g7)
    c: Vertical(g6)
    c: Vertical(g8)
    c: Horizontal(g2,g7)
    c: Horizontal(g0,g3)
    c: DistanceY(g6,g5) = 12.8
    c: Horizontal(g5,g1)
    c: DistanceX(g0,g3) = 2.25
    c: DistanceX(g0,g6) = 24.88
    c: DistanceX(g0,g2) = 8.77
    c: DistanceX(g0,g7) = 18.28
    c: DistanceY(g0,g-1) = 11.4
FEATURE [PartDesign::Pocket] Pocket013  label="USBCCutout"
  BaseFeature = -> Pocket012
  Direction = (0,0,-1)
  Length = 22
  Length2 = 5
  Profile = -> Sketch033
  ReferenceAxis = -> Sketch033 [N_Axis]
  Suppressed = false
  Type = 0
  expr: Length = 22
FEATURE [Sketcher::SketchObject] Sketch034  label="USBCCableCutoutSketch"
  ArcFitTolerance = 0
  AttachmentSupport = -> [Pocket013]
  FullyConstrained = true
  MakeInternals = false
  MapMode = 5
  Placement = pos=(0,16.3,0) rot=(0,0.707107,0.707107;3.14159rad)
  expr: Constraints[18] = <<parameters>>.camera_width / 2 - <<parameters>>.camera_usbc_offsetx_end + 1.55 mm
  expr: Constraints[19] = <<parameters>>.camera_width / 2 - <<parameters>>.camera_usbc_offsetx_start - 1.52 mm
  expr: Constraints[20] = <<parameters>>.camera_width / 2 - (<<parameters>>.camera_usbc_offsetx_start + <<parameters>>.camera_usbc_offsetx_end) / 2 + 4.73 mm
  expr: Constraints[21] = <<parameters>>.camera_width / 2 - (<<parameters>>.camera_usbc_offsetx_start + <<parameters>>.camera_usbc_offsetx_end) / 2 - 4.78 mm
  sketch-geometry (8):
    g0: LineSegment StartX=-24.88 StartY=15.25 StartZ=0 EndX=-18.28 EndY=15.25 EndZ=0
    g1: LineSegment StartX=-18.28 StartY=15.25 StartZ=0 EndX=-18.28 EndY=0 EndZ=0
    g2: LineSegment StartX=-18.28 StartY=0 StartZ=0 EndX=-24.88 EndY=0 EndZ=0
    g3: LineSegment StartX=-24.88 StartY=0 StartZ=0 EndX=-24.88 EndY=15.25 EndZ=0
    g4: LineSegment StartX=-8.77 StartY=15.25 StartZ=0 EndX=-2.25 EndY=15.25 EndZ=0
    g5: LineSegment StartX=-2.25 StartY=15.25 StartZ=0 EndX=-2.25 EndY=0 EndZ=0
    g6: LineSegment StartX=-2.25 StartY=0 StartZ=0 EndX=-8.77 EndY=0 EndZ=0
    g7: LineSegment StartX=-8.77 StartY=0 StartZ=0 EndX=-8.77 EndY=15.25 EndZ=0
  constraints (24):
    c: Coincident(g0,g1)
    c: Coincident(g1,g2)
    c: Coincident(g2,g3)
    c: Coincident(g3,g0)
    c: Horizontal(g0)
    c: Horizontal(g2)
    c: Vertical(g1)
    c: Vertical(g3)
    c: PointOnObject(g1,g-1)
    c: Coincident(g4,g5)
    c: Coincident(g5,g6)
    c: Coincident(g6,g7)
    c: Coincident(g7,g4)
    c: Horizontal(g4)
    c: Horizontal(g6)
    c: Vertical(g5)
    c: Vertical(g7)
    c: PointOnObject(g5,g-1)
    c: DistanceX(g5,g-1) = 2.25
    c: DistanceX(g2,g-1) = 24.88
    c: DistanceX(g1,g-1) = 18.28
    c: DistanceX(g6,g-1) = 8.77
    c: Horizontal(g4,g0)
    c: DistanceY(g-1,g4) = 15.25
FEATURE [PartDesign::Pocket] Pocket014  label="USBCCableCutout"
  BaseFeature = -> Pocket013
  Direction = (0,-1,2e-16)
  Length = 17.55
  Length2 = 5
  Profile = -> Sketch034
  ReferenceAxis = -> Sketch034 [N_Axis]
  Suppressed = false
  Type = 0
  expr: Length = <<parameters>>.camera_depth / 2 + <<parameters>>.camera_attachment_thickness
FEATURE [PartDesign::Fillet] Fillet011  label="USBCSmoothing"
  Base = -> Pocket014 [Edge84,Edge86,Edge83,Edge92,Edge32,Edge30,Edge28,Edge26]
  BaseFeature = -> Pocket014
  Radius = 1.5
  SupportTransform = false
  Suppressed = false
  UseAllEdges = false
FEATURE [Sketcher::SketchObject] Sketch035  label="CameraMountBoltHolesSketch"
  ArcFitTolerance = 0
  AttachmentSupport = -> [Fillet011]
  FullyConstrained = true
  MakeInternals = false
  MapMode = 5
  Placement = pos=(0,0,0) rot=(1,0,0;3.14159rad)
  expr: Constraints[0] = <<parameters>>.camera_mount_depth / 2 - <<parameters>>.plate_bolt_diameter * 1.5
  expr: Constraints[10] = <<parameters>>.plate_bolt_diameter
  expr: Constraints[11] = <<parameters>>.plate_bolt_diameter
  expr: Constraints[1] = <<parameters>>.camera_mount_depth / 2 - <<parameters>>.plate_bolt_diameter * 1.5
  expr: Constraints[2] = <<parameters>>.camera_hole_spacing / 2
  expr: Constraints[3] = <<parameters>>.camera_hole_spacing / 2
  expr: Constraints[8] = <<parameters>>.plate_bolt_diameter
  expr: Constraints[9] = <<parameters>>.plate_bolt_diameter
  sketch-geometry (4):
    g0: Circle CenterX=-37.5 CenterY=11.5 CenterZ=0 NormalX=0 NormalY=0 NormalZ=1 AngleXU=0 Radius=1.6
    g1: Circle CenterX=-37.5 CenterY=-11.5 CenterZ=0 NormalX=0 NormalY=0 NormalZ=1 AngleXU=0 Radius=1.6
    g2: Circle CenterX=37.5 CenterY=-11.5 CenterZ=0 NormalX=0 NormalY=0 NormalZ=1 AngleXU=0 Radius=1.6
    g3: Circle CenterX=37.5 CenterY=11.5 CenterZ=0 NormalX=0 NormalY=0 NormalZ=1 AngleXU=0 Radius=1.6
  constraints (12):
    c: DistanceY(g1,g-1) = 11.5
    c: DistanceY(g-1,g0) = 11.5
    c: DistanceX(g0,g-1) = 37.5
    c: DistanceX(g-1,g3) = 37.5
    c: Vertical(g2,g3)
    c: Vertical(g1,g0)
    c: Horizontal(g2,g1)
    c: Horizontal(g0,g3)
    c: Diameter(g1) = 3.2
    c: Diameter(g0) = 3.2
    c: Diameter(g3) = 3.2
    c: Diameter(g2) = 3.2
FEATURE [PartDesign::Pocket] Pocket015  label="CameraMountBoltHoles"
  BaseFeature = -> Fillet011
  Direction = (0,0,1)
  Length = 5
  Length2 = 5
  Profile = -> Sketch035
  ReferenceAxis = -> Sketch035 [N_Axis]
  Suppressed = false
  Type = 0
FEATURE [Sketcher::SketchObject] Sketch036  label="CameraMountNutCatches1Sketch"
  ArcFitTolerance = 0
  AttachmentSupport = -> [Pocket015]
  FullyConstrained = true
  MakeInternals = false
  MapMode = 5
  Placement = pos=(0,16.3,0) rot=(0,0.707107,0.707107;3.14159rad)
  expr: Constraints[16] = <<parameters>>.camera_hole_spacing / 2 + 5.6 mm / 2
  expr: Constraints[17] = <<parameters>>.camera_hole_spacing / 2 + 5.6 mm / 2
  sketch-geometry (8):
    g0: LineSegment StartX=-40.3 StartY=5.1 StartZ=0 EndX=-34.7 EndY=5.1 EndZ=0
    g1: LineSegment StartX=-34.7 StartY=5.1 StartZ=0 EndX=-34.7 EndY=2.5 EndZ=0
    g2: LineSegment StartX=-34.7 StartY=2.5 StartZ=0 EndX=-40.3 EndY=2.5 EndZ=0
    g3: LineSegment StartX=-40.3 StartY=2.5 StartZ=0 EndX=-40.3 EndY=5.1 EndZ=0
    g4: LineSegment StartX=34.7 StartY=5.1 StartZ=0 EndX=40.3 EndY=5.1 EndZ=0
    g5: LineSegment StartX=40.3 StartY=5.1 StartZ=0 EndX=40.3 EndY=2.5 EndZ=0
    g6: LineSegment StartX=40.3 StartY=2.5 StartZ=0 EndX=34.7 EndY=2.5 EndZ=0
    g7: LineSegment StartX=34.7 StartY=2.5 StartZ=0 EndX=34.7 EndY=5.1 EndZ=0
  constraints (24):
    c: Coincident(g0,g1)
    c: Coincident(g1,g2)
    c: Coincident(g2,g3)
    c: Coincident(g3,g0)
    c: Horizontal(g0)
    c: Horizontal(g2)
    c: Vertical(g1)
    c: Vertical(g3)
    c: Coincident(g4,g5)
    c: Coincident(g5,g6)
    c: Coincident(g6,g7)
    c: Coincident(g7,g4)
    c: Horizontal(g4)
    c: Horizontal(g6)
    c: Vertical(g5)
    c: Vertical(g7)
    c: DistanceX(g2,g-1) = 40.3
    c: DistanceX(g-1,g4) = 40.3
    c: DistanceX(g4,g4) = 5.6
    c: DistanceX(g0,g0) = 5.6
    c: Horizontal(g6,g1)
    c: DistanceY(g-1,g1) = 2.5
    c: DistanceY(g2,g0) = 2.6
    c: Horizontal(g4,g0)
FEATURE [PartDesign::Pocket] Pocket016  label="CameraMountNutCatches1"
  BaseFeature = -> Pocket015
  Direction = (0,-1,2e-16)
  Length = 8.3
  Length2 = 5
  Profile = -> Sketch036
  ReferenceAxis = -> Sketch036 [N_Axis]
  Suppressed = false
  Type = 0
  expr: Length = <<parameters>>.plate_bolt_diameter * 1.5 + <<parameters>>.plate_nut_diameter / 2 + 0.25 mm
FEATURE [Sketcher::SketchObject] Sketch037  label="CameraMountNutCatches2Sketch"
  ArcFitTolerance = 0
  AttachmentSupport = -> [Pocket015]
  FullyConstrained = true
  MakeInternals = false
  MapMode = 5
  Placement = pos=(0,-16.3,0) rot=(1,0,0;1.5708rad)
  expr: Constraints[16] = <<parameters>>.camera_hole_spacing / 2 + 5.6 mm / 2
  expr: Constraints[17] = <<parameters>>.camera_hole_spacing / 2 + 5.6 mm / 2
  sketch-geometry (8):
    g0: LineSegment StartX=-40.3 StartY=5.1 StartZ=0 EndX=-34.7 EndY=5.1 EndZ=0
    g1: LineSegment StartX=-34.7 StartY=5.1 StartZ=0 EndX=-34.7 EndY=2.5 EndZ=0
    g2: LineSegment StartX=-34.7 StartY=2.5 StartZ=0 EndX=-40.3 EndY=2.5 EndZ=0
    g3: LineSegment StartX=-40.3 StartY=2.5 StartZ=0 EndX=-40.3 EndY=5.1 EndZ=0
    g4: LineSegment StartX=34.7 StartY=5.1 StartZ=0 EndX=40.3 EndY=5.1 EndZ=0
    g5: LineSegment StartX=40.3 StartY=5.1 StartZ=0 EndX=40.3 EndY=2.5 EndZ=0
    g6: LineSegment StartX=40.3 StartY=2.5 StartZ=0 EndX=34.7 EndY=2.5 EndZ=0
    g7: LineSegment StartX=34.7 StartY=2.5 StartZ=0 EndX=34.7 EndY=5.1 EndZ=0
  constraints (24):
    c: Coincident(g0,g1)
    c: Coincident(g1,g2)
    c: Coincident(g2,g3)
    c: Coincident(g3,g0)
    c: Horizontal(g0)
    c: Horizontal(g2)
    c: Vertical(g1)
    c: Vertical(g3)
    c: Coincident(g4,g5)
    c: Coincident(g5,g6)
    c: Coincident(g6,g7)
    c: Coincident(g7,g4)
    c: Horizontal(g4)
    c: Horizontal(g6)
    c: Vertical(g5)
    c: Vertical(g7)
    c: DistanceX(g2,g-1) = 40.3
    c: DistanceX(g-1,g4) = 40.3
    c: DistanceX(g4,g4) = 5.6
    c: DistanceX(g0,g0) = 5.6
    c: Horizontal(g6,g1)
    c: DistanceY(g-1,g1) = 2.5
    c: DistanceY(g2,g0) = 2.6
    c: Horizontal(g4,g0)
FEATURE [PartDesign::Pocket] Pocket017  label="CameraMountNutCatches2"
  BaseFeature = -> Pocket016
  Direction = (0,1,-2e-16)
  Length = 8.3
  Length2 = 5
  Profile = -> Sketch037
  ReferenceAxis = -> Sketch037 [N_Axis]
  Suppressed = false
  Type = 0
  expr: Length = <<parameters>>.plate_bolt_diameter * 1.5 + <<parameters>>.plate_nut_diameter / 2 + 0.25 mm
FEATURE [Sketcher::SketchObject] Sketch038  label="CameraStandPlateSketch"
  ArcFitTolerance = 0
  AttachmentSupport = -> [XY_Plane019]
  FullyConstrained = true
  MakeInternals = false
  MapMode = 5
  expr: Constraints[10] = <<parameters>>.camera_mount_depth / 2
  expr: Constraints[11] = <<parameters>>.camera_mount_depth
  expr: Constraints[8] = <<parameters>>.camera_mount_width / 2
  expr: Constraints[9] = <<parameters>>.camera_mount_width
  sketch-geometry (4):
    g0: LineSegment StartX=-55 StartY=16.3 StartZ=0 EndX=55 EndY=16.3 EndZ=0
    g1: LineSegment StartX=55 StartY=16.3 StartZ=0 EndX=55 EndY=-16.3 EndZ=0
    g2: LineSegment StartX=55 StartY=-16.3 StartZ=0 EndX=-55 EndY=-16.3 EndZ=0
    g3: LineSegment StartX=-55 StartY=-16.3 StartZ=0 EndX=-55 EndY=16.3 EndZ=0
  constraints (12):
    c: Coincident(g0,g1)
    c: Coincident(g1,g2)
    c: Coincident(g2,g3)
    c: Coincident(g3,g0)
    c: Horizontal(g0)
    c: Horizontal(g2)
    c: Vertical(g1)
    c: Vertical(g3)
    c: DistanceX(g0,g-1) = 55
    c: DistanceX(g0,g0) = 110
    c: DistanceY(g-1,g0) = 16.3
    c: DistanceY(g2,g0) = 32.6
FEATURE [PartDesign::Pad] Pad020  label="CameraStandPlate"
  Direction = (0,0,1)
  Length = 5
  Length2 = 10
  Profile = -> Sketch038
  ReferenceAxis = -> Sketch038 [N_Axis]
  Reversed = true
  Suppressed = false
  Type = 0
FEATURE [Sketcher::SketchObject] Sketch039  label="CameraStandBoltHolesSketch"
  ArcFitTolerance = 0
  AttachmentSupport = -> [Pad020]
  FullyConstrained = true
  MakeInternals = false
  MapMode = 5
  Placement = pos=(0,0,-5) rot=(1,0,0;3.14159rad)
  expr: Constraints[0] = <<parameters>>.camera_mount_depth / 2 - <<parameters>>.plate_bolt_diameter * 1.5
  expr: Constraints[10] = <<parameters>>.plate_bolt_diameter
  expr: Constraints[11] = <<parameters>>.plate_bolt_diameter
  expr: Constraints[1] = <<parameters>>.camera_mount_depth / 2 - <<parameters>>.plate_bolt_diameter * 1.5
  expr: Constraints[2] = <<parameters>>.camera_hole_spacing / 2
  expr: Constraints[3] = <<parameters>>.camera_hole_spacing / 2
  expr: Constraints[8] = <<parameters>>.plate_bolt_diameter
  expr: Constraints[9] = <<parameters>>.plate_bolt_diameter
  sketch-geometry (4):
    g0: Circle CenterX=-37.5 CenterY=11.5 CenterZ=0 NormalX=0 NormalY=0 NormalZ=1 AngleXU=0 Radius=1.6
    g1: Circle CenterX=-37.5 CenterY=-11.5 CenterZ=0 NormalX=0 NormalY=0 NormalZ=1 AngleXU=0 Radius=1.6
    g2: Circle CenterX=37.5 CenterY=-11.5 CenterZ=0 NormalX=0 NormalY=0 NormalZ=1 AngleXU=0 Radius=1.6
    g3: Circle CenterX=37.5 CenterY=11.5 CenterZ=0 NormalX=0 NormalY=0 NormalZ=1 AngleXU=0 Radius=1.6
  constraints (12):
    c: DistanceY(g1,g-1) = 11.5
    c: DistanceY(g-1,g0) = 11.5
    c: DistanceX(g0,g-1) = 37.5
    c: DistanceX(g-1,g3) = 37.5
    c: Vertical(g2,g3)
    c: Vertical(g1,g0)
    c: Horizontal(g2,g1)
    c: Horizontal(g0,g3)
    c: Diameter(g1) = 3.2
    c: Diameter(g0) = 3.2
    c: Diameter(g3) = 3.2
    c: Diameter(g2) = 3.2
FEATURE [PartDesign::Pocket] Pocket018  label="CameraStandBoltHoles"
  BaseFeature = -> Pad020
  Direction = (0,0,1)
  Length = 5
  Length2 = 5
  Profile = -> Sketch039
  ReferenceAxis = -> Sketch039 [N_Axis]
  Suppressed = false
  Type = 0
FEATURE [Sketcher::SketchObject] Sketch040  label="CameraStandLegsSketch"
  ArcFitTolerance = 0
  AttachmentSupport = -> [Pocket018]
  FullyConstrained = true
  MakeInternals = false
  MapMode = 5
  expr: Constraints[32] = <<parameters>>.camera_mount_depth / 2
  expr: Constraints[37] = <<parameters>>.camera_mount_width / 2
  expr: Constraints[38] = <<parameters>>.camera_mount_width / 2
  expr: Constraints[46] = 50
  expr: Constraints[51] = <<parameters>>.camera_mount_depth / 2 - 10 mm
  sketch-geometry (18):
    g0: LineSegment StartX=-55 StartY=27.7 StartZ=0 EndX=-45 EndY=27.7 EndZ=0
    g1: LineSegment StartX=-45 StartY=27.7 StartZ=0 EndX=-45 EndY=6.3 EndZ=0
    g2: LineSegment StartX=-45 StartY=6.3 StartZ=0 EndX=-55 EndY=6.3 EndZ=0
    g3: LineSegment StartX=-55 StartY=6.3 StartZ=0 EndX=-55 EndY=27.7 EndZ=0
    g4: LineSegment StartX=45 StartY=27.7 StartZ=0 EndX=55 EndY=27.7 EndZ=0
    g5: LineSegment StartX=55 StartY=27.7 StartZ=0 EndX=55 EndY=6.3 EndZ=0
    g6: LineSegment StartX=55 StartY=6.3 StartZ=0 EndX=45 EndY=6.3 EndZ=0
    g7: LineSegment StartX=45 StartY=6.3 StartZ=0 EndX=45 EndY=27.7 EndZ=0
    g8: LineSegment StartX=45 StartY=-6.3 StartZ=0 EndX=55 EndY=-6.3 EndZ=0
    g9: LineSegment StartX=55 StartY=-6.3 StartZ=0 EndX=55 EndY=-16.3 EndZ=0
    g10: LineSegment StartX=55 StartY=-16.3 StartZ=0 EndX=45 EndY=-16.3 EndZ=0
    g11: LineSegment StartX=45 StartY=-16.3 StartZ=0 EndX=45 EndY=-6.3 EndZ=0
    g12: LineSegment StartX=-55 StartY=-6.3 StartZ=0 EndX=-45 EndY=-6.3 EndZ=0
    g13: LineSegment StartX=-45 StartY=-6.3 StartZ=0 EndX=-45 EndY=-16.3 EndZ=0
    g14: LineSegment StartX=-45 StartY=-16.3 StartZ=0 EndX=-55 EndY=-16.3 EndZ=0
    g15: LineSegment StartX=-55 StartY=-16.3 StartZ=0 EndX=-55 EndY=-6.3 EndZ=0
    g16: GeomPoint [constr] X=-50 Y=-19.3 Z=0
    g17: GeomPoint [constr] X=-50 Y=30.7 Z=0
  constraints (52):
    c: Coincident(g0,g1)
    c: Coincident(g1,g2)
    c: Coincident(g2,g3)
    c: Coincident(g3,g0)
    c: Horizontal(g0)
    c: Horizontal(g2)
    c: Vertical(g1)
    c: Vertical(g3)
    c: Coincident(g4,g5)
    c: Coincident(g5,g6)
    c: Coincident(g6,g7)
    c: Coincident(g7,g4)
    c: Horizontal(g4)
    c: Horizontal(g6)
    c: Vertical(g5)
    c: Vertical(g7)
    c: Coincident(g8,g9)
    c: Coincident(g9,g10)
    c: Coincident(g10,g11)
    c: Coincident(g11,g8)
    c: Horizontal(g8)
    c: Horizontal(g10)
    c: Vertical(g9)
    c: Vertical(g11)
    c: Coincident(g12,g13)
    c: Coincident(g13,g14)
    c: Coincident(g14,g15)
    c: Coincident(g15,g12)
    c: Horizontal(g12)
    c: Horizontal(g14)
    c: Vertical(g13)
    c: Vertical(g15)
    c: DistanceY(g14,g-1) = 16.3
    c: Horizontal(g13,g10)
    c: Horizontal(g4,g0)
    c: Vertical(g5,g8)
    c: Vertical(g12,g2)
    c: DistanceX(g0,g-1) = 55
    c: DistanceX(g-1,g4) = 55
    c: DistanceX(g4,g4) = 10
    c: Horizontal(g1,g6)
    c: Vertical(g1,g12)
    c: DistanceX(g0,g0) = 10
    c: DistanceY(g9,g8) = 10
    c: Vertical(g8,g6)
    c: Horizontal(g12,g8)
    c: DistanceX(g16,g-1) = 50
    c: DistanceY(g16,g14) = 3
    c: Vertical(g17,g16)
    c: DistanceY(g16,g17) = 50
    c: DistanceY(g0,g17) = 3
    c: DistanceY(g-1,g1) = 6.3
FEATURE [PartDesign::Pad] Pad021  label="CameraStandLegs"
  BaseFeature = -> Pocket018
  Direction = (0,0,1)
  Length = 35
  Length2 = 10
  Profile = -> Sketch040
  ReferenceAxis = -> Sketch040 [N_Axis]
  Reversed = true
  Suppressed = false
  Type = 0
FEATURE [Sketcher::SketchObject] MirroredSketch  label="CameraStandFeetSketch"
  ArcFitTolerance = 0
  AttachmentSupport = -> [Pad021]
  FullyConstrained = true
  MakeInternals = false
  MapMode = 5
  Placement = pos=(0,0,-35) rot=(1,0,0;3.14159rad)
  expr: Constraints[20] = <<parameters>>.camera_mount_depth / 2
  expr: Constraints[21] = <<parameters>>.camera_mount_width / 2
  expr: Constraints[22] = <<parameters>>.camera_mount_width / 2
  expr: Constraints[48] = <<parameters>>.plate_bolt_diameter
  expr: Constraints[49] = <<parameters>>.plate_bolt_diameter
  expr: Constraints[63] = <<parameters>>.camera_mount_depth / 2 - 10 mm
  expr: Constraints[65] = <<parameters>>.plate_bolt_diameter
  expr: Constraints[66] = <<parameters>>.plate_bolt_diameter
  sketch-geometry (30):
    g0: LineSegment StartX=-45 StartY=-27.7 StartZ=0 EndX=-45 EndY=-6.3 EndZ=0
    g1: LineSegment StartX=-45 StartY=-6.3 StartZ=0 EndX=-55 EndY=-6.3 EndZ=0
    g2: LineSegment StartX=-55 StartY=-6.3 StartZ=0 EndX=-55 EndY=-27.7 EndZ=0
    g3: LineSegment StartX=55 StartY=-27.7 StartZ=0 EndX=55 EndY=-6.3 EndZ=0
    g4: LineSegment StartX=55 StartY=-6.3 StartZ=0 EndX=45 EndY=-6.3 EndZ=0
    g5: LineSegment StartX=45 StartY=-6.3 StartZ=0 EndX=45 EndY=-27.7 EndZ=0
    g6: LineSegment StartX=45 StartY=6.3 StartZ=0 EndX=55 EndY=6.3 EndZ=0
    g7: LineSegment StartX=55 StartY=6.3 StartZ=0 EndX=55 EndY=16.3 EndZ=0
    g8: LineSegment StartX=45 StartY=16.3 StartZ=0 EndX=45 EndY=6.3 EndZ=0
    g9: LineSegment StartX=-55 StartY=6.3 StartZ=0 EndX=-45 EndY=6.3 EndZ=0
    g10: LineSegment StartX=-45 StartY=6.3 StartZ=0 EndX=-45 EndY=16.3 EndZ=0
    g11: LineSegment StartX=-55 StartY=16.3 StartZ=0 EndX=-55 EndY=6.3 EndZ=0
    g12: GeomPoint [constr] X=-50 Y=19.3 Z=0
    g13: GeomPoint [constr] X=-50 Y=-30.7 Z=0
    g14: LineSegment StartX=-55 StartY=16.3 StartZ=0 EndX=-55 EndY=19.3 EndZ=0
    g15: LineSegment StartX=-45 StartY=16.3 StartZ=0 EndX=-45 EndY=19.3 EndZ=0
    g16: ArcOfCircle CenterX=-50 CenterY=19.3 CenterZ=0 NormalX=0 NormalY=0 NormalZ=1 AngleXU=0 Radius=5 StartAngle=0 EndAngle=3.14159
    g17: Circle CenterX=-50 CenterY=19.3 CenterZ=0 NormalX=0 NormalY=0 NormalZ=1 AngleXU=0 Radius=1.6
    g18: LineSegment StartX=45 StartY=16.3 StartZ=0 EndX=45 EndY=19.3 EndZ=0
    g19: LineSegment StartX=55 StartY=16.3 StartZ=0 EndX=55 EndY=19.3 EndZ=0
    g20: Circle CenterX=50 CenterY=19.3 CenterZ=0 NormalX=0 NormalY=0 NormalZ=1 AngleXU=0 Radius=1.6
    g21: ArcOfCircle CenterX=50 CenterY=19.3 CenterZ=0 NormalX=0 NormalY=0 NormalZ=1 AngleXU=0 Radius=5 StartAngle=0 EndAngle=3.14159
    g22: Circle CenterX=-50 CenterY=-30.7 CenterZ=0 NormalX=0 NormalY=0 NormalZ=1 AngleXU=0 Radius=1.6
    g23: Circle CenterX=50 CenterY=-30.7 CenterZ=0 NormalX=0 NormalY=0 NormalZ=1 AngleXU=0 Radius=1.6
    g24: LineSegment StartX=-55 StartY=-27.7 StartZ=0 EndX=-55 EndY=-30.7 EndZ=0
    g25: LineSegment StartX=-45 StartY=-27.7 StartZ=0 EndX=-45 EndY=-30.7 EndZ=0
    g26: LineSegment StartX=45 StartY=-27.7 StartZ=0 EndX=45 EndY=-30.7 EndZ=0
    g27: LineSegment StartX=55 StartY=-27.7 StartZ=0 EndX=55 EndY=-30.7 EndZ=0
    g28: ArcOfCircle CenterX=-50 CenterY=-30.7 CenterZ=0 NormalX=0 NormalY=0 NormalZ=1 AngleXU=0 Radius=5 StartAngle=3.14159 EndAngle=6.28319
    g29: ArcOfCircle CenterX=50 CenterY=-30.7 CenterZ=0 NormalX=0 NormalY=0 NormalZ=1 AngleXU=0 Radius=5 StartAngle=3.14159 EndAngle=6.28318
  constraints (86):
    c: Coincident(g0,g1)
    c: Coincident(g1,g2)
    c: Horizontal(g1)
    c: Vertical(g0)
    c: Vertical(g2)
    c: Coincident(g3,g4)
    c: Coincident(g4,g5)
    c: Horizontal(g4)
    c: Vertical(g3)
    c: Vertical(g5)
    c: Coincident(g6,g7)
    c: Coincident(g8,g6)
    c: Horizontal(g6)
    c: Vertical(g7)
    c: Vertical(g8)
    c: Coincident(g9,g10)
    c: Coincident(g11,g9)
    c: Horizontal(g9)
    c: Vertical(g10)
    c: Vertical(g11)
    c: DistanceY(g-1,g11) = 16.3
    c: DistanceX(g11,g-1) = 55
    c: DistanceX(g-1,g7) = 55
    c: Horizontal(g10,g8)
    c: Horizontal(g8,g7)
    c: Horizontal(g10,g11)
    c: Horizontal(g9,g6)
    c: DistanceY(g6,g7) = 10
    c: DistanceX(g11,g10) = 10
    c: DistanceX(g8,g7) = 10
    c: DistanceY(g11,g12) = 3
    c: Coincident(g14,g11)
    c: Vertical(g14)
    c: Coincident(g15,g10)
    c: Vertical(g15)
    c: Horizontal(g12,g15)
    c: Horizontal(g12,g14)
    c: Coincident(g16,g12)
    c: Coincident(g16,g14)
    c: Coincident(g16,g15)
    c: Coincident(g17,g16)
    c: Coincident(g18,g8)
    c: Vertical(g18)
    c: Coincident(g19,g7)
    c: Vertical(g19)
    c: Horizontal(g20,g16)
    c: Horizontal(g20,g18)
    c: Horizontal(g19,g20)
    c: Diameter(g20) = 3.2
    c: Diameter(g17) = 3.2
    c: Coincident(g21,g20)
    c: Coincident(g21,g18)
    c: Coincident(g21,g19)
    c: Coincident(g22,g13)
    c: Vertical(g23,g20)
    c: Vertical(g22,g16)
    c: Horizontal(g22,g23)
    c: DistanceY(g22,g2) = 3
    c: Horizontal(g0,g4)
    c: Vertical(g9,g1)
    c: Vertical(g3,g6)
    c: Vertical(g4,g6)
    c: Vertical(g0,g9)
    c: DistanceY(g1,g-1) = 6.3
    c: DistanceY(g22,g16) = 50
    c: Diameter(g22) = 3.2
    c: Diameter(g23) = 3.2
    c: Horizontal(g0,g2)
    c: Horizontal(g5,g3)
    c: Horizontal(g5,g0)
    c: Coincident(g24,g2)
    c: Vertical(g24)
    c: Coincident(g25,g0)
    c: Vertical(g25)
    c: Coincident(g26,g5)
    c: Vertical(g26)
    c: Coincident(g27,g3)
    c: Vertical(g27)
    c: Horizontal(g23,g26)
    c: Horizontal(g22,g24)
    c: Coincident(g28,g22)
    c: Coincident(g28,g24)
    c: Coincident(g28,g25)
    c: Coincident(g29,g23)
    c: Coincident(g29,g26)
    c: Coincident(g29,g27)
FEATURE [PartDesign::Pad] Pad022  label="CameraStandFeet"
  BaseFeature = -> Pad021
  Direction = (0,0,-1)
  Length = 5
  Length2 = 10
  Profile = -> MirroredSketch
  ReferenceAxis = -> MirroredSketch [N_Axis]
  Suppressed = false
  Type = 0
FEATURE [Sketcher::SketchObject] Sketch041  label="CameraStandLegCutoutSketch"
  ArcFitTolerance = 0
  AttachmentSupport = -> [Pad022]
  FullyConstrained = true
  MakeInternals = false
  MapMode = 5
  Placement = pos=(55,0,0) rot=(0.57735,0.57735,0.57735;2.0944rad)
  expr: Constraints[1] = <<parameters>>.camera_mount_depth / 2
  expr: Constraints[2] = 50 mm - (<<parameters>>.camera_mount_depth + 6 mm)
  expr: Constraints[6] = <<parameters>>.camera_mount_depth / 2 - 10 mm
  sketch-geometry (6):
    g0: LineSegment StartX=16.3 StartY=0 StartZ=0 EndX=27.7 EndY=-35 EndZ=0
    g1: LineSegment StartX=17.7 StartY=-40 StartZ=0 EndX=6.3 EndY=-5 EndZ=0
    g2: LineSegment StartX=6.3 StartY=-5 StartZ=0 EndX=6.3 EndY=-40 EndZ=0
    g3: LineSegment StartX=6.3 StartY=-40 StartZ=0 EndX=17.7 EndY=-40 EndZ=0
    g4: LineSegment StartX=16.3 StartY=0 StartZ=0 EndX=27.7 EndY=0 EndZ=0
    g5: LineSegment StartX=27.7 StartY=0 StartZ=0 EndX=27.7 EndY=-35 EndZ=0
  constraints (18):
    c: PointOnObject(g0,g-1)
    c: DistanceX(g-1,g0) = 16.3
    c: DistanceX(g0,g0) = 11.4
    c: DistanceY(g1,g-1) = 40
    c: DistanceX(g1,g0) = 10
    c: DistanceY(g1,g-1) = 5
    c: DistanceX(g-1,g1) = 6.3
    c: DistanceY(g1,g0) = 5
    c: Coincident(g2,g1)
    c: Vertical(g2)
    c: Horizontal(g2,g1)
    c: Coincident(g3,g2)
    c: Coincident(g3,g1)
    c: Coincident(g4,g0)
    c: PointOnObject(g4,g-1)
    c: Vertical(g4,g0)
    c: Coincident(g5,g4)
    c: Coincident(g5,g0)
FEATURE [PartDesign::Pocket] Pocket019  label="CameraStandLegCutout"
  BaseFeature = -> Pad022
  Direction = (-1,0,0)
  Length = 110
  Length2 = 5
  Profile = -> Sketch041
  ReferenceAxis = -> Sketch041 [N_Axis]
  Suppressed = false
  Type = 0
  expr: Length = <<parameters>>.camera_mount_width
FEATURE [PartDesign::Fillet] Fillet012  label="CameraStandLegSmoothing"
  Base = -> Pocket019 [Edge62,Edge85]
  BaseFeature = -> Pocket019
  Radius = 2.5
  SupportTransform = false
  Suppressed = false
  UseAllEdges = false
FEATURE [PartDesign::Body] Body009  label="CameraStandBody"
  AllowCompound = false
  Group = -> [Sketch038,Pad020,Sketch039,Pocket018,Sketch040,Pad021,MirroredSketch,Pad022,Sketch041,Pocket019,Fillet012]
  Origin = -> Origin019
  Tip = -> Fillet012
FEATURE [App::Part] Part009  label="CameraStand"
  Group = -> [Body009]
  Origin = -> Origin018
FEATURE [Sketcher::SketchObject] Sketch042
  ArcFitTolerance = 0
  AttachmentSupport = -> [XY_Plane021]
  FullyConstrained = true
  MakeInternals = false
  MapMode = 5
  expr: Constraints[11] = 17.75 mm
  expr: Constraints[8] = 17.75 mm / 2
  sketch-geometry (4):
    g0: LineSegment StartX=-8.875 StartY=5 StartZ=0 EndX=8.875 EndY=5 EndZ=0
    g1: LineSegment StartX=8.875 StartY=5 StartZ=0 EndX=8.875 EndY=-5 EndZ=0
    g2: LineSegment StartX=8.875 StartY=-5 StartZ=0 EndX=-8.875 EndY=-5 EndZ=0
    g3: LineSegment StartX=-8.875 StartY=-5 StartZ=0 EndX=-8.875 EndY=5 EndZ=0
  constraints (12):
    c: Coincident(g0,g1)
    c: Coincident(g1,g2)
    c: Coincident(g2,g3)
    c: Coincident(g3,g0)
    c: Horizontal(g0)
    c: Horizontal(g2)
    c: Vertical(g1)
    c: Vertical(g3)
    c: DistanceX(g0,g-1) = 8.875
    c: DistanceY(g-1,g0) = 5
    c: DistanceY(g1,g0) = 10
    c: DistanceX(g0,g0) = 17.75
FEATURE [PartDesign::Pad] Pad023
  Direction = (0,0,1)
  Length = 16.625
  Length2 = 10
  Profile = -> Sketch042
  ReferenceAxis = -> Sketch042 [N_Axis]
  Suppressed = false
  Type = 0
FEATURE [Sketcher::SketchObject] Sketch043
  ArcFitTolerance = 0
  AttachmentSupport = -> [Pad023]
  FullyConstrained = true
  MakeInternals = false
  MapMode = 5
  Placement = pos=(0,-5,0) rot=(1,0,0;1.5708rad)
  expr: Constraints[10] = 12.3 / 2
  expr: Constraints[11] = 12.3 / 2
  expr: Constraints[12] = 6.5 mm / 2
  expr: Constraints[13] = 6.5 mm / 2
  sketch-geometry (5):
    g0: GeomPoint [constr] X=0 Y=10.2 Z=0
    g1: LineSegment StartX=-6.15 StartY=13.45 StartZ=0 EndX=6.15 EndY=13.45 EndZ=0
    g2: LineSegment StartX=6.15 StartY=13.45 StartZ=0 EndX=6.15 EndY=6.95 EndZ=0
    g3: LineSegment StartX=6.15 StartY=6.95 StartZ=0 EndX=-6.15 EndY=6.95 EndZ=0
    g4: LineSegment StartX=-6.15 StartY=6.95 StartZ=0 EndX=-6.15 EndY=13.45 EndZ=0
  constraints (14):
    c: PointOnObject(g0,g-2)
    c: DistanceY(g-1,g0) = 10.2
    c: Coincident(g1,g2)
    c: Coincident(g2,g3)
    c: Coincident(g3,g4)
    c: Coincident(g4,g1)
    c: Horizontal(g1)
    c: Horizontal(g3)
    c: Vertical(g2)
    c: Vertical(g4)
    c: DistanceX(g3,g-1) = 6.15
    c: DistanceX(g-1,g2) = 6.15
    c: DistanceY(g3,g0) = 3.25
    c: DistanceY(g0,g1) = 3.25
FEATURE [PartDesign::Pocket] Pocket020
  BaseFeature = -> Pad023
  Direction = (0,1,-2e-16)
  Length = 10
  Length2 = 5
  Profile = -> Sketch043
  ReferenceAxis = -> Sketch043 [N_Axis]
  Suppressed = false
  Type = 0
FEATURE [PartDesign::Fillet] Fillet013
  Base = -> Pocket020 [Edge17,Edge18,Edge20,Edge22]
  BaseFeature = -> Pocket020
  Radius = 1
  SupportTransform = false
  Suppressed = false
  UseAllEdges = false
FEATURE [PartDesign::Fillet] Fillet014
  Base = -> Fillet013 [Edge34,Edge31]
  BaseFeature = -> Fillet013
  Radius = 2.5
  SupportTransform = false
  Suppressed = false
  UseAllEdges = false
FEATURE [PartDesign::Fillet] Fillet015
  Base = -> Fillet014 [Edge5,Edge1]
  BaseFeature = -> Fillet014
  Radius = 2
  SupportTransform = false
  Suppressed = false
  UseAllEdges = false
FEATURE [PartDesign::Fillet] Fillet016
  Base = -> Fillet015 [Edge50]
  BaseFeature = -> Fillet015
  Radius = 2
  SupportTransform = false
  Suppressed = false
  UseAllEdges = false
FEATURE [Sketcher::SketchObject] Sketch044
  ArcFitTolerance = 0
  AttachmentSupport = -> [XY_Plane021]
  FullyConstrained = true
  MakeInternals = false
  MapMode = 5
  expr: Constraints[2] = <<parameters>>.plate_bolt_diameter
  sketch-geometry (5):
    g0: Circle CenterX=-1 CenterY=8 CenterZ=0 NormalX=0 NormalY=0 NormalZ=1 AngleXU=0 Radius=1.6
    g1: LineSegment StartX=-6 StartY=8 StartZ=0 EndX=-6 EndY=0 EndZ=0
    g2: LineSegment StartX=4 StartY=8 StartZ=0 EndX=4 EndY=0 EndZ=0
    g3: ArcOfCircle CenterX=-1 CenterY=8 CenterZ=0 NormalX=0 NormalY=0 NormalZ=1 AngleXU=0 Radius=5 StartAngle=0 EndAngle=3.14159
    g4: LineSegment StartX=-6 StartY=0 StartZ=0 EndX=4 EndY=0 EndZ=0
  constraints (15):
    c: DistanceY(g-1,g0) = 8
    c: DistanceX(g0,g-1) = 1
    c: Diameter(g0) = 3.2
    c: Vertical(g1)
    c: Vertical(g2)
    c: Horizontal(g2,g0)
    c: Horizontal(g0,g1)
    c: DistanceX(g0,g2) = 5
    c: Coincident(g3,g0)
    c: Coincident(g3,g1)
    c: Coincident(g3,g2)
    c: Horizontal(g-1,g1)
    c: Horizontal(g-1,g2)
    c: Coincident(g4,g1)
    c: Coincident(g4,g2)
FEATURE [PartDesign::Pad] Pad024
  BaseFeature = -> Fillet016
  Direction = (0,0,1)
  Length = 2.5
  Length2 = 10
  Profile = -> Sketch044
  ReferenceAxis = -> Sketch044 [N_Axis]
  Suppressed = false
  Type = 0
FEATURE [PartDesign::Fillet] Fillet017
  Base = -> Pad024 [Edge58,Edge61,Edge60]
  BaseFeature = -> Pad024
  Radius = 1
  SupportTransform = false
  Suppressed = false
  UseAllEdges = false
FEATURE [PartDesign::Body] Body010  label="USBCBraceBody"
  AllowCompound = false
  Group = -> [Sketch042,Pad023,Sketch043,Pocket020,Fillet013,Fillet014,Fillet015,Fillet016,Sketch044,Pad024,Fillet017]
  Origin = -> Origin021
  Tip = -> Fillet017
FEATURE [App::Part] Part010  label="USBCBrace"
  Group = -> [Body010]
  Origin = -> Origin020
FEATURE [Sketcher::SketchObject] Sketch045  label="CameraMountLidHullSketch"
  ArcFitTolerance = 0
  AttachmentSupport = -> [XY_Plane023]
  FullyConstrained = true
  MakeInternals = false
  MapMode = 5
  expr: Constraints[10] = <<parameters>>.camera_mount_depth / 2
  expr: Constraints[11] = <<parameters>>.camera_mount_depth
  expr: Constraints[8] = <<parameters>>.camera_mount_width / 2
  expr: Constraints[9] = <<parameters>>.camera_mount_width
  sketch-geometry (4):
    g0: LineSegment StartX=-55 StartY=16.3 StartZ=0 EndX=55 EndY=16.3 EndZ=0
    g1: LineSegment StartX=55 StartY=16.3 StartZ=0 EndX=55 EndY=-16.3 EndZ=0
    g2: LineSegment StartX=55 StartY=-16.3 StartZ=0 EndX=-55 EndY=-16.3 EndZ=0
    g3: LineSegment StartX=-55 StartY=-16.3 StartZ=0 EndX=-55 EndY=16.3 EndZ=0
  constraints (12):
    c: Coincident(g0,g1)
    c: Coincident(g1,g2)
    c: Coincident(g2,g3)
    c: Coincident(g3,g0)
    c: Horizontal(g0)
    c: Horizontal(g2)
    c: Vertical(g1)
    c: Vertical(g3)
    c: DistanceX(g0,g-1) = 55
    c: DistanceX(g0,g0) = 110
    c: DistanceY(g-1,g0) = 16.3
    c: DistanceY(g2,g0) = 32.6
FEATURE [PartDesign::Pad] Pad025  label="CameraMountLidHull"
  Direction = (0,0,1)
  Length = 15.35
  Length2 = 10
  Profile = -> Sketch045
  ReferenceAxis = -> Sketch045 [N_Axis]
  Suppressed = false
  Type = 0
  expr: Length = <<parameters>>.camera_height / 2 - <<parameters>>.camera_bolt_diameter + 5 mm
FEATURE [Sketcher::SketchObject] Sketch046  label="CameraMountLidMountSketch"
  ArcFitTolerance = 0
  AttachmentSupport = -> [Pad025]
  FullyConstrained = true
  MakeInternals = false
  MapMode = 5
  Placement = pos=(0,16.3,0) rot=(0,0.707107,0.707107;3.14159rad)
  expr: Constraints[16] = <<parameters>>.camera_hole_spacing / 2 + <<parameters>>.camera_bolt_diameter
  expr: Constraints[17] = <<parameters>>.camera_bolt_diameter * 2
  expr: Constraints[18] = <<parameters>>.camera_hole_spacing / 2 + <<parameters>>.camera_bolt_diameter
  expr: Constraints[19] = <<parameters>>.camera_bolt_diameter * 2
  expr: Constraints[21] = <<parameters>>.camera_height / 2 - <<parameters>>.camera_bolt_diameter + 5 mm
  expr: Constraints[23] = <<parameters>>.camera_bolt_diameter * 2
  expr: Constraints[25] = <<parameters>>.camera_bolt_diameter
  expr: Constraints[26] = <<parameters>>.camera_bolt_diameter
  expr: Constraints[27] = <<parameters>>.camera_bolt_diameter
  expr: Constraints[28] = <<parameters>>.camera_bolt_diameter
  expr: Constraints[29] = <<parameters>>.camera_bolt_diameter
  sketch-geometry (10):
    g0: LineSegment StartX=-42 StartY=15.35 StartZ=0 EndX=-33 EndY=15.35 EndZ=0
    g1: LineSegment StartX=-33 StartY=15.35 StartZ=0 EndX=-33 EndY=-9 EndZ=0
    g2: LineSegment StartX=-33 StartY=-9 StartZ=0 EndX=-42 EndY=-9 EndZ=0
    g3: LineSegment StartX=-42 StartY=-9 StartZ=0 EndX=-42 EndY=15.35 EndZ=0
    g4: LineSegment StartX=33 StartY=15.35 StartZ=0 EndX=42 EndY=15.35 EndZ=0
    g5: LineSegment StartX=42 StartY=15.35 StartZ=0 EndX=42 EndY=-9 EndZ=0
    g6: LineSegment StartX=42 StartY=-9 StartZ=0 EndX=33 EndY=-9 EndZ=0
    g7: LineSegment StartX=33 StartY=-9 StartZ=0 EndX=33 EndY=15.35 EndZ=0
    g8: Circle CenterX=-37.5 CenterY=-4.5 CenterZ=0 NormalX=0 NormalY=0 NormalZ=1 AngleXU=0 Radius=2.25
    g9: Circle CenterX=37.5 CenterY=-4.5 CenterZ=0 NormalX=0 NormalY=0 NormalZ=1 AngleXU=0 Radius=2.25
  constraints (30):
    c: Coincident(g0,g1)
    c: Coincident(g1,g2)
    c: Coincident(g2,g3)
    c: Coincident(g3,g0)
    c: Horizontal(g0)
    c: Horizontal(g2)
    c: Vertical(g1)
    c: Vertical(g3)
    c: Coincident(g4,g5)
    c: Coincident(g5,g6)
    c: Coincident(g6,g7)
    c: Coincident(g7,g4)
    c: Horizontal(g4)
    c: Horizontal(g6)
    c: Vertical(g5)
    c: Vertical(g7)
    c: DistanceX(g0,g-1) = 42
    c: DistanceX(g0,g0) = 9
    c: DistanceX(g-1,g4) = 42
    c: DistanceX(g4,g4) = 9
    c: Horizontal(g4,g0)
    c: DistanceY(g-1,g0) = 15.35
    c: Horizontal(g1,g6)
    c: DistanceY(g5,g-1) = 9
    c: Horizontal(g9,g8)
    c: DistanceX(g8,g1) = 4.5
    c: DistanceY(g2,g8) = 4.5
    c: Diameter(g8) = 4.5
    c: Diameter(g9) = 4.5
    c: DistanceX(g9,g5) = 4.5
FEATURE [PartDesign::Pad] Pad026  label="CameraMountLidMount"
  BaseFeature = -> Pad025
  Direction = (0,1,-2e-16)
  Length = 5
  Length2 = 10
  Profile = -> Sketch046
  ReferenceAxis = -> Sketch046 [N_Axis]
  Suppressed = false
  Type = 0
  expr: Length = <<parameters>>.camera_attachment_thickness
FEATURE [PartDesign::Fillet] Fillet018
  Base = -> Pad026 [Edge48,Edge46,Edge38,Edge13]
  BaseFeature = -> Pad026
  Radius = 3.5
  SupportTransform = false
  Suppressed = false
  UseAllEdges = false
  expr: Radius = <<parameters>>.camera_bolt_diameter - 1 mm
FEATURE [Sketcher::SketchObject] Sketch047
  ArcFitTolerance = 0
  AttachmentSupport = -> [Fillet018]
  FullyConstrained = true
  MakeInternals = false
  MapMode = 5
  Placement = pos=(0,0,0) rot=(1,0,0;3.14159rad)
  expr: Constraints[10] = <<parameters>>.camera_width / 2 + <<parameters>>.margin + 2 mm
  expr: Constraints[11] = <<parameters>>.camera_depth + <<parameters>>.camera_attachment_thickness
  expr: Constraints[8] = <<parameters>>.camera_mount_depth / 2
  expr: Constraints[9] = <<parameters>>.camera_width / 2 + <<parameters>>.margin + 2 mm
  sketch-geometry (4):
    g0: LineSegment StartX=-50.7 StartY=13.8 StartZ=0 EndX=50.7 EndY=13.8 EndZ=0
    g1: LineSegment StartX=50.7 StartY=13.8 StartZ=0 EndX=50.7 EndY=-16.3 EndZ=0
    g2: LineSegment StartX=50.7 StartY=-16.3 StartZ=0 EndX=-50.7 EndY=-16.3 EndZ=0
    g3: LineSegment StartX=-50.7 StartY=-16.3 StartZ=0 EndX=-50.7 EndY=13.8 EndZ=0
  constraints (12):
    c: Coincident(g0,g1)
    c: Coincident(g1,g2)
    c: Coincident(g2,g3)
    c: Coincident(g3,g0)
    c: Horizontal(g0)
    c: Horizontal(g2)
    c: Vertical(g1)
    c: Vertical(g3)
    c: DistanceY(g1,g-1) = 16.3
    c: DistanceX(g-1,g1) = 50.7
    c: DistanceX(g2,g-1) = 50.7
    c: DistanceY(g1,g0) = 30.1
FEATURE [PartDesign::Pocket] Pocket021  label="CameraMountLidCutout"
  BaseFeature = -> Fillet018
  Direction = (0,0,1)
  Length = 10.35
  Length2 = 5
  Profile = -> Sketch047
  ReferenceAxis = -> Sketch047 [N_Axis]
  Suppressed = false
  Type = 0
  expr: Length = <<parameters>>.camera_height / 2 - <<parameters>>.camera_bolt_diameter
FEATURE [Sketcher::SketchObject] Sketch048
  ArcFitTolerance = 0
  AttachmentSupport = -> [Pocket021]
  FullyConstrained = true
  MakeInternals = false
  MapMode = 5
  Placement = pos=(0,0,0) rot=(1,0,0;3.14159rad)
  expr: Constraints[10] = <<parameters>>.camera_depth + <<parameters>>.camera_attachment_thickness - <<parameters>>.camera_mount_depth / 2
  expr: Constraints[11] = <<parameters>>.camera_mount_depth / 2
  expr: Constraints[8] = <<parameters>>.camera_width / 2
  expr: Constraints[9] = <<parameters>>.camera_width / 2
  sketch-geometry (4):
    g0: LineSegment StartX=-48.5 StartY=16.3 StartZ=0 EndX=48.5 EndY=16.3 EndZ=0
    g1: LineSegment StartX=48.5 StartY=16.3 StartZ=0 EndX=48.5 EndY=13.8 EndZ=0
    g2: LineSegment StartX=48.5 StartY=13.8 StartZ=0 EndX=-48.5 EndY=13.8 EndZ=0
    g3: LineSegment StartX=-48.5 StartY=13.8 StartZ=0 EndX=-48.5 EndY=16.3 EndZ=0
  constraints (12):
    c: Coincident(g0,g1)
    c: Coincident(g1,g2)
    c: Coincident(g2,g3)
    c: Coincident(g3,g0)
    c: Horizontal(g0)
    c: Horizontal(g2)
    c: Vertical(g1)
    c: Vertical(g3)
    c: DistanceX(g2,g-1) = 48.5
    c: DistanceX(g-1,g1) = 48.5
    c: DistanceY(g-1,g2) = 13.8
    c: DistanceY(g-1,g0) = 16.3
FEATURE [PartDesign::Pocket] Pocket022  label="CameraMountLidOpening"
  BaseFeature = -> Pocket021
  Direction = (0,0,1)
  Length = 7.85
  Length2 = 5
  Profile = -> Sketch048
  ReferenceAxis = -> Sketch048 [N_Axis]
  Suppressed = false
  Type = 0
  expr: Length = <<parameters>>.camera_height / 2 - <<parameters>>.camera_bolt_diameter - 2.5 mm
FEATURE [PartDesign::Fillet] Fillet019
  Base = -> Pocket022 [Edge59,Edge79]
  BaseFeature = -> Pocket022
  Radius = 2
  SupportTransform = false
  Suppressed = false
  UseAllEdges = false
FEATURE [Sketcher::SketchObject] Sketch049
  ArcFitTolerance = 0
  AttachmentSupport = -> [Fillet019]
  FullyConstrained = true
  MakeInternals = false
  MapMode = 5
  Placement = pos=(0,0,15.35) rot=(0,0,1;0rad)
  expr: Constraints[10] = <<parameters>>.camera_hole_spacing / 2 - <<parameters>>.camera_bolt_diameter
  expr: Constraints[11] = <<parameters>>.camera_mount_depth / 2
  expr: Constraints[9] = <<parameters>>.camera_hole_spacing / 2 - <<parameters>>.camera_bolt_diameter
  sketch-geometry (4):
    g0: LineSegment StartX=-33 StartY=16.3 StartZ=0 EndX=33 EndY=16.3 EndZ=0
    g1: LineSegment StartX=33 StartY=16.3 StartZ=0 EndX=33 EndY=0 EndZ=0
    g2: LineSegment StartX=33 StartY=0 StartZ=0 EndX=-33 EndY=0 EndZ=0
    g3: LineSegment StartX=-33 StartY=0 StartZ=0 EndX=-33 EndY=16.3 EndZ=0
  constraints (12):
    c: Coincident(g0,g1)
    c: Coincident(g1,g2)
    c: Coincident(g2,g3)
    c: Coincident(g3,g0)
    c: Horizontal(g0)
    c: Horizontal(g2)
    c: Vertical(g1)
    c: Vertical(g3)
    c: PointOnObject(g1,g-1)
    c: DistanceX(g0,g-1) = 33
    c: DistanceX(g-1,g0) = 33
    c: DistanceY(g1,g0) = 16.3
FEATURE [PartDesign::Pocket] Pocket023
  BaseFeature = -> Fillet019
  Direction = (0,0,-1)
  Length = 5
  Length2 = 5
  Profile = -> Sketch049
  ReferenceAxis = -> Sketch049 [N_Axis]
  Suppressed = false
  Type = 0
FEATURE [PartDesign::Fillet] Fillet020
  Base = -> Pocket023 [Edge51,Edge54,Edge27,Edge31,Edge92,Edge91]
  BaseFeature = -> Pocket023
  Radius = 2
  SupportTransform = false
  Suppressed = false
  UseAllEdges = false
FEATURE [PartDesign::Fillet] Fillet021
  Base = -> Fillet020 [Edge58,Edge29]
  BaseFeature = -> Fillet020
  Radius = 2
  SupportTransform = false
  Suppressed = false
  UseAllEdges = false
FEATURE [PartDesign::Body] Body011  label="CameraMountLidBody"
  AllowCompound = false
  Group = -> [Sketch045,Pad025,Sketch046,Pad026,Fillet018,Sketch047,Pocket021,Sketch048,Pocket022,Fillet019,Sketch049,Pocket023,Fillet020,Fillet021]
  Origin = -> Origin023
  Placement = pos=(0,0,51.75) rot=(0,0,1;0rad)
  Tip = -> Fillet021
FEATURE [App::Part] Part011  label="CameraMountLid"
  Group = -> [Body011]
  Origin = -> Origin022
  Placement = pos=(0,0,-5.7) rot=(0,0,1;0rad)
FEATURE [PartDesign::SubtractivePrism] Prism  label="CameraHeatsinkCutout"
  AttacherType = Attacher::AttachEngine3D
  AttachmentOffset = pos=(0,0,-56) rot=(0,0,1;0.785398rad)
  AttachmentSupport = -> [Pocket017]
  BaseFeature = -> Pocket017
  Circumradius = 16
  FirstAngle = 0
  Height = 56
  MapMode = 7
  Placement = pos=(-28,16.3,26.65) rot=(0.678598,0.281085,0.678598;2.59356rad)
  Polygon = 3
  SecondAngle = 0
  Suppressed = false
FEATURE [PartDesign::Body] Body008  label="CameraMountBody"
  AllowCompound = false
  Group = -> [Sketch028,Pad019,Sketch029,Pocket009,Sketch030,Pocket010,Fillet008,Sketch031,Pocket011,Fillet009,Fillet010,Sketch032,Pocket012,Sketch033,Pocket013,Sketch034,Pocket014,Fillet011,Sketch035,Pocket015,Sketch036,Pocket016,Sketch037,Pocket017,Prism]
  Origin = -> Origin017
  Tip = -> Prism
FEATURE [App::Part] Part008  label="CameraMount"
  Group = -> [Body008]
  Origin = -> Origin016
FEATURE [Mesh::Feature] y_adapter_20211129  label="USBC-Y-Adapter"
  Placement = pos=(0.8,1.3,33.68) rot=(1,0,0;3.14159rad)
FEATURE [Sketcher::SketchObject] Sketch050
  ArcFitTolerance = 0
  AttachmentSupport = -> [YZ_Plane025]
  FullyConstrained = true
  MakeInternals = false
  MapMode = 5
  Placement = pos=(0,0,0) rot=(0.57735,0.57735,0.57735;2.0944rad)
  sketch-geometry (4):
    g0: LineSegment StartX=0 StartY=0 StartZ=0 EndX=-12.5 EndY=0 EndZ=0
    g1: LineSegment StartX=-12.5 StartY=0 StartZ=0 EndX=-12.5 EndY=1.45 EndZ=0
    g2: LineSegment StartX=0 StartY=0 StartZ=0 EndX=-2e-16 EndY=1.125 EndZ=0
    g3: LineSegment StartX=-12.5 StartY=1.45 StartZ=0 EndX=0 EndY=1.125 EndZ=0
  constraints (11):
    c: Coincident(g0,g-1)
    c: PointOnObject(g0,g-1)
    c: Coincident(g1,g0)
    c: Vertical(g1)
    c: Coincident(g2,g0)
    c: PointOnObject(g2,g-2)
    c: Coincident(g3,g1)
    c: Coincident(g3,g2)
    c: DistanceX(g0,g0) = 12.5
    c: DistanceY(g0,g2) = 1.125
    c: DistanceY(g0,g1) = 1.45
FEATURE [PartDesign::Pad] Pad027
  Direction = (1,0,0)
  Length = 25.4
  Length2 = 10
  Placement = pos=(0,0,0) rot=(0.57735,0.57735,0.57735;2.0944rad)
  Profile = -> Sketch050
  ReferenceAxis = -> Sketch050 [N_Axis]
  Suppressed = false
  Type = 0
FEATURE [Sketcher::SketchObject] Sketch051
  ArcFitTolerance = 0
  AttachmentSupport = -> [Pad027]
  FullyConstrained = true
  MakeInternals = false
  MapMode = 5
  Placement = pos=(0,0,0) rot=(0.707107,0.707107,0;3.14159rad)
  expr: Constraints[10] = 12.5 / 2 - 2.6 / 2
  expr: Constraints[11] = 12.5 / 2 + 2.6 / 2
  expr: Constraints[8] = 25.4 / 2 - 8.5 / 2
  expr: Constraints[9] = 25.4 / 2 + 8.5 / 2
  sketch-geometry (4):
    g0: LineSegment StartX=-7.55 StartY=16.95 StartZ=0 EndX=-4.95 EndY=16.95 EndZ=0
    g1: LineSegment StartX=-4.95 StartY=16.95 StartZ=0 EndX=-4.95 EndY=8.45 EndZ=0
    g2: LineSegment StartX=-4.95 StartY=8.45 StartZ=0 EndX=-7.55 EndY=8.45 EndZ=0
    g3: LineSegment StartX=-7.55 StartY=8.45 StartZ=0 EndX=-7.55 EndY=16.95 EndZ=0
  constraints (12):
    c: Coincident(g0,g1)
    c: Coincident(g1,g2)
    c: Coincident(g2,g3)
    c: Coincident(g3,g0)
    c: Horizontal(g0)
    c: Horizontal(g2)
    c: Vertical(g1)
    c: Vertical(g3)
    c: DistanceY(g-1,g1) = 8.45
    c: DistanceY(g-1,g0) = 16.95
    c: DistanceX(g1,g-1) = 4.95
    c: DistanceX(g2,g-1) = 7.55
FEATURE [PartDesign::Pocket] Pocket024
  BaseFeature = -> Pad027
  Direction = (0,0,1)
  Length = 2
  Length2 = 5
  Placement = pos=(0,0,0) rot=(0.57735,0.57735,0.57735;2.0944rad)
  Profile = -> Sketch051
  ReferenceAxis = -> Sketch051 [N_Axis]
  Suppressed = false
  Type = 0
FEATURE [PartDesign::Fillet] Fillet022
  Base = -> Pocket024 [Edge11,Edge10,Edge14,Edge12]
  BaseFeature = -> Pocket024
  Placement = pos=(0,0,0) rot=(0.57735,0.57735,0.57735;2.0944rad)
  Radius = 3
  SupportTransform = false
  Suppressed = false
  UseAllEdges = false
FEATURE [PartDesign::Fillet] Fillet023
  Base = -> Fillet022 [Edge29,Edge31,Edge33,Edge35]
  BaseFeature = -> Fillet022
  Placement = pos=(0,0,0) rot=(0.57735,0.57735,0.57735;2.0944rad)
  Radius = 1
  SupportTransform = false
  Suppressed = false
  UseAllEdges = false
FEATURE [PartDesign::Body] Body012  label="USBCShimBody"
  AllowCompound = false
  Group = -> [Sketch050,Pad027,Sketch051,Pocket024,Fillet022,Fillet023]
  Origin = -> Origin025
  Tip = -> Fillet023
FEATURE [App::Part] Part012  label="USBC-Y-Shim"
  Group = -> [Body012]
  Origin = -> Origin024
  Placement = pos=(26.25,-11.25,25.58) rot=(0,0,1;3.14159rad)
FEATURE [Sketcher::SketchObject] Sketch052
  ArcFitTolerance = 0
  AttachmentSupport = -> [XY_Plane027]
  FullyConstrained = true
  MakeInternals = false
  MapMode = 5
  sketch-geometry (4):
    g0: LineSegment StartX=0 StartY=0 StartZ=0 EndX=14 EndY=0 EndZ=0
    g1: LineSegment StartX=14 StartY=0 StartZ=0 EndX=14 EndY=6.4 EndZ=0
    g2: LineSegment StartX=14 StartY=6.4 StartZ=0 EndX=0 EndY=6.4 EndZ=0
    g3: LineSegment StartX=0 StartY=6.4 StartZ=0 EndX=0 EndY=0 EndZ=0
  constraints (11):
    c: Coincident(g0,g1)
    c: Coincident(g1,g2)
    c: Coincident(g2,g3)
    c: Coincident(g3,g0)
    c: Horizontal(g0)
    c: Horizontal(g2)
    c: Vertical(g1)
    c: Vertical(g3)
    c: Coincident(g0,g-1)
    c: DistanceX(g0,g1) = 14
    c: DistanceY(g0,g1) = 6.4
FEATURE [PartDesign::Pad] Pad028
  Direction = (0,0,1)
  Length = 2.2
  Length2 = 10
  Profile = -> Sketch052
  ReferenceAxis = -> Sketch052 [N_Axis]
  Suppressed = false
  Type = 0
FEATURE [PartDesign::Body] Body013  label="USBCSpacerBody"
  AllowCompound = false
  Group = -> [Sketch052,Pad028]
  Origin = -> Origin027
  Tip = -> Pad028
FEATURE [App::Part] Part013  label="USBCSpacer"
  Group = -> [Body013]
  Origin = -> Origin026
FEATURE [Sketcher::SketchObject] Sketch053  label="BumperHullSketch"
  ArcFitTolerance = 0
  AttachmentSupport = -> [XZ_Plane029]
  FullyConstrained = true
  MakeInternals = false
  MapMode = 5
  Placement = pos=(0,0,0) rot=(1,0,0;1.5708rad)
  expr: Constraints[0] = <<parameters>>.plate_bolt_diameter
  expr: Constraints[10] = <<parameters>>.bumper_hole_spacing_x / 2
  expr: Constraints[11] = <<parameters>>.bumper_hole_spacing_y / 2
  expr: Constraints[1] = <<parameters>>.plate_bolt_diameter
  expr: Constraints[20] = <<parameters>>.bumper_width
  expr: Constraints[21] = <<parameters>>.bumper_height
  expr: Constraints[22] = <<parameters>>.bumper_height / 2
  expr: Constraints[23] = <<parameters>>.bumper_width / 2
  expr: Constraints[2] = <<parameters>>.plate_bolt_diameter
  expr: Constraints[3] = <<parameters>>.plate_bolt_diameter
  expr: Constraints[4] = <<parameters>>.bumper_hole_spacing_x
  expr: Constraints[5] = <<parameters>>.bumper_hole_spacing_y
  sketch-geometry (8):
    g0: Circle CenterX=25.725 CenterY=6.35 CenterZ=0 NormalX=0 NormalY=0 NormalZ=1 AngleXU=0 Radius=1.6
    g1: Circle CenterX=-25.725 CenterY=6.35 CenterZ=0 NormalX=0 NormalY=0 NormalZ=1 AngleXU=0 Radius=1.6
    g2: Circle CenterX=-25.725 CenterY=-6.35 CenterZ=0 NormalX=0 NormalY=0 NormalZ=1 AngleXU=0 Radius=1.6
    g3: Circle CenterX=25.725 CenterY=-6.35 CenterZ=0 NormalX=0 NormalY=0 NormalZ=1 AngleXU=0 Radius=1.6
    g4: LineSegment StartX=-29.6 StartY=21.9 StartZ=0 EndX=29.6 EndY=21.9 EndZ=0
    g5: LineSegment StartX=29.6 StartY=21.9 StartZ=0 EndX=29.6 EndY=-21.9 EndZ=0
    g6: LineSegment StartX=29.6 StartY=-21.9 StartZ=0 EndX=-29.6 EndY=-21.9 EndZ=0
    g7: LineSegment StartX=-29.6 StartY=-21.9 StartZ=0 EndX=-29.6 EndY=21.9 EndZ=0
  constraints (24):
    c: Diameter(g1) = 3.2
    c: Diameter(g0) = 3.2
    c: Diameter(g3) = 3.2
    c: Diameter(g2) = 3.2
    c: DistanceX(g1,g0) = 51.45
    c: DistanceY(g2,g1) = 12.7
    c: Horizontal(g1,g0)
    c: Vertical(g0,g3)
    c: Horizontal(g2,g3)
    c: Vertical(g1,g2)
    c: DistanceX(g1,g-1) = 25.725
    c: DistanceY(g-1,g1) = 6.35
    c: Coincident(g4,g5)
    c: Coincident(g5,g6)
    c: Coincident(g6,g7)
    c: Coincident(g7,g4)
    c: Horizontal(g4)
    c: Horizontal(g6)
    c: Vertical(g5)
    c: Vertical(g7)
    c: DistanceX(g4,g4) = 59.2
    c: DistanceY(g6,g4) = 43.8
    c: DistanceY(g-1,g4) = 21.9
    c: DistanceX(g4,g-1) = 29.6
FEATURE [PartDesign::Pad] Pad029  label="BumperHull"
  Direction = (0,-1,2e-16)
  Length = 5
  Length2 = 10
  Placement = pos=(0,0,0) rot=(1,0,0;1.5708rad)
  Profile = -> Sketch053
  ReferenceAxis = -> Sketch053 [N_Axis]
  Suppressed = false
  Type = 0
  expr: Length = <<parameters>>.bumper_thickness
FEATURE [Sketcher::SketchObject] Sketch054  label="BumperNubsSketch"
  ArcFitTolerance = 0
  AttachmentSupport = -> [Pad029]
  FullyConstrained = true
  MakeInternals = false
  MapMode = 5
  Placement = pos=(0,0,0) rot=(-1,0,0;1.5708rad)
  expr: Constraints[0] = <<parameters>>.plate_bolt_diameter
  expr: Constraints[10] = <<parameters>>.bumper_hole_spacing_x / 2
  expr: Constraints[11] = <<parameters>>.bumper_hole_spacing_y / 2
  expr: Constraints[16] = <<parameters>>.bumper_hole_keepout
  expr: Constraints[17] = <<parameters>>.bumper_hole_keepout
  expr: Constraints[18] = <<parameters>>.bumper_hole_keepout
  expr: Constraints[19] = <<parameters>>.bumper_hole_keepout
  expr: Constraints[1] = <<parameters>>.plate_bolt_diameter
  expr: Constraints[2] = <<parameters>>.plate_bolt_diameter
  expr: Constraints[3] = <<parameters>>.plate_bolt_diameter
  expr: Constraints[4] = <<parameters>>.bumper_hole_spacing_x
  expr: Constraints[5] = <<parameters>>.bumper_hole_spacing_y
  sketch-geometry (8):
    g0: Circle CenterX=25.725 CenterY=6.35 CenterZ=0 NormalX=0 NormalY=0 NormalZ=1 AngleXU=0 Radius=1.6
    g1: Circle CenterX=-25.725 CenterY=6.35 CenterZ=0 NormalX=0 NormalY=0 NormalZ=1 AngleXU=0 Radius=1.6
    g2: Circle CenterX=-25.725 CenterY=-6.35 CenterZ=0 NormalX=0 NormalY=0 NormalZ=1 AngleXU=0 Radius=1.6
    g3: Circle CenterX=25.725 CenterY=-6.35 CenterZ=0 NormalX=0 NormalY=0 NormalZ=1 AngleXU=0 Radius=1.6
    g4: Circle CenterX=-25.725 CenterY=6.35 CenterZ=0 NormalX=0 NormalY=0 NormalZ=1 AngleXU=0 Radius=3.875
    g5: Circle CenterX=-25.725 CenterY=-6.35 CenterZ=0 NormalX=0 NormalY=0 NormalZ=1 AngleXU=0 Radius=3.875
    g6: Circle CenterX=25.725 CenterY=-6.35 CenterZ=0 NormalX=0 NormalY=0 NormalZ=1 AngleXU=0 Radius=3.875
    g7: Circle CenterX=25.725 CenterY=6.35 CenterZ=0 NormalX=0 NormalY=0 NormalZ=1 AngleXU=0 Radius=3.875
  constraints (20):
    c: Diameter(g1) = 3.2
    c: Diameter(g0) = 3.2
    c: Diameter(g3) = 3.2
    c: Diameter(g2) = 3.2
    c: DistanceX(g1,g0) = 51.45
    c: DistanceY(g2,g1) = 12.7
    c: Horizontal(g1,g0)
    c: Vertical(g0,g3)
    c: Horizontal(g2,g3)
    c: Vertical(g1,g2)
    c: DistanceX(g1,g-1) = 25.725
    c: DistanceY(g-1,g1) = 6.35
    c: Coincident(g4,g1)
    c: Coincident(g5,g2)
    c: Coincident(g6,g3)
    c: Coincident(g7,g0)
    c: Diameter(g4) = 7.75
    c: Diameter(g7) = 7.75
    c: Diameter(g6) = 7.75
    c: Diameter(g5) = 7.75
FEATURE [PartDesign::Pad] Pad030  label="BumperNubs"
  BaseFeature = -> Pad029
  Direction = (0,1,2e-16)
  Length = 2
  Length2 = 10
  Placement = pos=(0,0,0) rot=(1,0,0;1.5708rad)
  Profile = -> Sketch054
  ReferenceAxis = -> Sketch054 [N_Axis]
  Suppressed = false
  Type = 0
  expr: Length = <<parameters>>.bumper_nub_height
FEATURE [Sketcher::SketchObject] Sketch055  label="BumperSwitchMountsSketch"
  ArcFitTolerance = 0
  AttachmentSupport = -> [Pad030]
  FullyConstrained = true
  MakeInternals = false
  MapMode = 5
  Placement = pos=(0,0,0) rot=(-1,0,0;1.5708rad)
  expr: Constraints[32] = (<<parameters>>.bumper_hole_spacing_x - <<parameters>>.bumper_hole_keepout) / 2 - 0.5 "
  expr: Constraints[33] = (<<parameters>>.bumper_hole_spacing_x - <<parameters>>.bumper_hole_keepout) / 2 - 0.5 "
  expr: Constraints[40] = <<parameters>>.bumper_bolt_diameter * 2
  expr: Constraints[41] = <<parameters>>.bumper_bolt_diameter * 2
  expr: Constraints[44] = <<parameters>>.bumper_switch_hole_spacing / 2 - <<parameters>>.bumper_bolt_diameter
  expr: Constraints[46] = <<parameters>>.bumper_switch_hole_spacing / 2 - <<parameters>>.bumper_bolt_diameter
  sketch-geometry (16):
    g0: LineSegment StartX=2.8 StartY=15.4 StartZ=0 EndX=9.15 EndY=15.4 EndZ=0
    g1: LineSegment StartX=9.15 StartY=15.4 StartZ=0 EndX=9.15 EndY=9 EndZ=0
    g2: LineSegment StartX=9.15 StartY=9 StartZ=0 EndX=2.8 EndY=9 EndZ=0
    g3: LineSegment StartX=2.8 StartY=9 StartZ=0 EndX=2.8 EndY=15.4 EndZ=0
    g4: LineSegment StartX=2.8 StartY=-9 StartZ=0 EndX=9.15 EndY=-9 EndZ=0
    g5: LineSegment StartX=9.15 StartY=-9 StartZ=0 EndX=9.15 EndY=-15.4 EndZ=0
    g6: LineSegment StartX=9.15 StartY=-15.4 StartZ=0 EndX=2.8 EndY=-15.4 EndZ=0
    g7: LineSegment StartX=2.8 StartY=-15.4 StartZ=0 EndX=2.8 EndY=-9 EndZ=0
    g8: LineSegment StartX=-9.15 StartY=-9 StartZ=0 EndX=-2.8 EndY=-9 EndZ=0
    g9: LineSegment StartX=-2.8 StartY=-9 StartZ=0 EndX=-2.8 EndY=-15.4 EndZ=0
    g10: LineSegment StartX=-2.8 StartY=-15.4 StartZ=0 EndX=-9.15 EndY=-15.4 EndZ=0
    g11: LineSegment StartX=-9.15 StartY=-15.4 StartZ=0 EndX=-9.15 EndY=-9 EndZ=0
    g12: LineSegment StartX=-9.15 StartY=15.4 StartZ=0 EndX=-2.8 EndY=15.4 EndZ=0
    g13: LineSegment StartX=-2.8 StartY=15.4 StartZ=0 EndX=-2.8 EndY=9 EndZ=0
    g14: LineSegment StartX=-2.8 StartY=9 StartZ=0 EndX=-9.15 EndY=9 EndZ=0
    g15: LineSegment StartX=-9.15 StartY=9 StartZ=0 EndX=-9.15 EndY=15.4 EndZ=0
  constraints (48):
    c: Coincident(g0,g1)
    c: Coincident(g1,g2)
    c: Coincident(g2,g3)
    c: Coincident(g3,g0)
    c: Horizontal(g0)
    c: Horizontal(g2)
    c: Vertical(g1)
    c: Vertical(g3)
    c: Coincident(g4,g5)
    c: Coincident(g5,g6)
    c: Coincident(g6,g7)
    c: Coincident(g7,g4)
    c: Horizontal(g4)
    c: Horizontal(g6)
    c: Vertical(g5)
    c: Vertical(g7)
    c: Coincident(g8,g9)
    c: Coincident(g9,g10)
    c: Coincident(g10,g11)
    c: Coincident(g11,g8)
    c: Horizontal(g8)
    c: Horizontal(g10)
    c: Vertical(g9)
    c: Vertical(g11)
    c: Coincident(g12,g13)
    c: Coincident(g13,g14)
    c: Coincident(g14,g15)
    c: Coincident(g15,g12)
    c: Horizontal(g12)
    c: Horizontal(g14)
    c: Vertical(g13)
    c: Vertical(g15)
    c: DistanceX(g12,g-1) = 9.15
    c: DistanceX(g-1,g0) = 9.15
    c: Vertical(g14,g8)
    c: Vertical(g1,g4)
    c: Vertical(g4,g2)
    c: Horizontal(g13,g2)
    c: Vertical(g13,g8)
    c: Horizontal(g8,g4)
    c: DistanceY(g14,g12) = 6.4
    c: DistanceY(g10,g8) = 6.4
    c: DistanceX(g12,g12) = 6.35
    c: DistanceX(g0,g0) = 6.35
    c: DistanceY(g-1,g13) = 9
    c: Horizontal(g0,g12)
    c: DistanceY(g8,g-1) = 9
    c: Horizontal(g9,g6)
FEATURE [PartDesign::Pad] Pad031  label="BumperSwitchMounts"
  BaseFeature = -> Pad030
  Direction = (0,1,2e-16)
  Length = 6.4
  Length2 = 10
  Placement = pos=(0,0,0) rot=(1,0,0;1.5708rad)
  Profile = -> Sketch055
  ReferenceAxis = -> Sketch055 [N_Axis]
  Suppressed = false
  Type = 0
  expr: Length = <<parameters>>.bumper_bolt_diameter * 2
FEATURE [Sketcher::SketchObject] Sketch056  label="BumperSwitchCutoutsSketch"
  ArcFitTolerance = 0
  AttachmentSupport = -> [Pad031]
  FullyConstrained = true
  MakeInternals = false
  MapMode = 5
  Placement = pos=(0,0,0) rot=(-1,0,0;1.5708rad)
  expr: Constraints[16] = (<<parameters>>.bumper_hole_spacing_x - <<parameters>>.bumper_hole_keepout) / 2 - 0.075 "
  expr: Constraints[17] = (<<parameters>>.bumper_hole_spacing_x - <<parameters>>.bumper_hole_keepout) / 2 - 0.075 "
  expr: Constraints[20] = <<parameters>>.bumper_switch_hole_spacing / 2 + <<parameters>>.bumper_bolt_diameter + 1.5 mm
  expr: Constraints[21] = <<parameters>>.bumper_switch_hole_spacing + (<<parameters>>.bumper_bolt_diameter + 1.5 mm) * 2
  sketch-geometry (8):
    g0: LineSegment StartX=-19.945 StartY=16.9 StartZ=0 EndX=-9.155 EndY=16.9 EndZ=0
    g1: LineSegment StartX=-9.155 StartY=16.9 StartZ=0 EndX=-9.155 EndY=-16.9 EndZ=0
    g2: LineSegment StartX=-9.155 StartY=-16.9 StartZ=0 EndX=-19.945 EndY=-16.9 EndZ=0
    g3: LineSegment StartX=-19.945 StartY=-16.9 StartZ=0 EndX=-19.945 EndY=16.9 EndZ=0
    g4: LineSegment StartX=9.155 StartY=16.9 StartZ=0 EndX=19.945 EndY=16.9 EndZ=0
    g5: LineSegment StartX=19.945 StartY=16.9 StartZ=0 EndX=19.945 EndY=-16.9 EndZ=0
    g6: LineSegment StartX=19.945 StartY=-16.9 StartZ=0 EndX=9.155 EndY=-16.9 EndZ=0
    g7: LineSegment StartX=9.155 StartY=-16.9 StartZ=0 EndX=9.155 EndY=16.9 EndZ=0
  constraints (24):
    c: Coincident(g0,g1)
    c: Coincident(g1,g2)
    c: Coincident(g2,g3)
    c: Coincident(g3,g0)
    c: Horizontal(g0)
    c: Horizontal(g2)
    c: Vertical(g1)
    c: Vertical(g3)
    c: Coincident(g4,g5)
    c: Coincident(g5,g6)
    c: Coincident(g6,g7)
    c: Coincident(g7,g4)
    c: Horizontal(g4)
    c: Horizontal(g6)
    c: Vertical(g5)
    c: Vertical(g7)
    c: DistanceX(g0,g-1) = 19.945
    c: DistanceX(g-1,g4) = 19.945
    c: DistanceX(g4,g4) = 10.79
    c: DistanceX(g0,g0) = 10.79
    c: DistanceY(g-1,g0) = 16.9
    c: DistanceY(g2,g0) = 33.8
    c: Horizontal(g0,g4)
    c: Horizontal(g1,g6)
FEATURE [PartDesign::Pocket] Pocket025  label="BumperSwitchCutouts"
  BaseFeature = -> Pad031
  Direction = (0,-1,-2e-16)
  Length = 5
  Length2 = 5
  Placement = pos=(0,0,0) rot=(1,0,0;1.5708rad)
  Profile = -> Sketch056
  ReferenceAxis = -> Sketch056 [N_Axis]
  Suppressed = false
  Type = 0
  expr: Length = <<parameters>>.bumper_thickness
FEATURE [Sketcher::SketchObject] Sketch057  label="BumperSwitchBoltsSketch"
  ArcFitTolerance = 0
  AttachmentSupport = -> [Pocket025]
  FullyConstrained = true
  MakeInternals = false
  MapMode = 5
  Placement = pos=(-9.15,0,0) rot=(0.707107,0,-0.707107;3.14159rad)
  expr: Constraints[0] = <<parameters>>.bumper_switch_hole_spacing / 2
  expr: Constraints[1] = <<parameters>>.bumper_switch_hole_spacing / 2
  expr: Constraints[3] = <<parameters>>.bumper_bolt_diameter
  expr: Constraints[4] = <<parameters>>.bumper_bolt_diameter
  expr: Constraints[5] = <<parameters>>.bumper_bolt_diameter
  sketch-geometry (2):
    g0: Circle CenterX=-12.2 CenterY=-3.2 CenterZ=0 NormalX=0 NormalY=0 NormalZ=1 AngleXU=0 Radius=1.6
    g1: Circle CenterX=12.2 CenterY=-3.2 CenterZ=0 NormalX=0 NormalY=0 NormalZ=1 AngleXU=0 Radius=1.6
  constraints (6):
    c: DistanceX(g0,g-1) = 12.2
    c: DistanceX(g-1,g1) = 12.2
    c: Horizontal(g0,g1)
    c: DistanceY(g0,g-1) = 3.2
    c: Diameter(g0) = 3.2
    c: Diameter(g1) = 3.2
FEATURE [PartDesign::Pocket] Pocket026  label="BumperSwitchBolts"
  BaseFeature = -> Pocket025
  Direction = (1,0,2e-16)
  Length = 19.05
  Length2 = 5
  Placement = pos=(0,0,0) rot=(1,0,0;1.5708rad)
  Profile = -> Sketch057
  ReferenceAxis = -> Sketch057 [N_Axis]
  Suppressed = false
  Type = 0
  expr: Length = 0.75 "
FEATURE [PartDesign::Fillet] Fillet024  label="BumperNubsSmoothing"
  Base = -> Pocket026 [Edge114,Edge98,Edge60,Edge72]
  BaseFeature = -> Pocket026
  Placement = pos=(0,0,0) rot=(1,0,0;1.5708rad)
  Radius = 1.9
  SupportTransform = false
  Suppressed = false
  UseAllEdges = false
FEATURE [PartDesign::Fillet] Fillet025  label="BumperSwitchMountsSmoothing"
  Base = -> Fillet024 [Edge89,Edge59,Edge109,Edge79,Edge107,Edge77,Edge57,Edge87,Edge39,Edge26,Edge16,Edge30,Edge31,Edge17,Edge27,Edge40]
  BaseFeature = -> Fillet024
  Placement = pos=(0,0,0) rot=(1,0,0;1.5708rad)
  Radius = 3
  SupportTransform = false
  Suppressed = false
  UseAllEdges = false
  expr: Radius = <<parameters>>.bumper_bolt_diameter - 0.2 mm
FEATURE [PartDesign::Fillet] Fillet026  label="BumperHullSmoothing"
  Base = -> Fillet025 [Edge78,Edge76,Edge73,Edge74]
  BaseFeature = -> Fillet025
  Placement = pos=(0,0,0) rot=(1,0,0;1.5708rad)
  Radius = 3.2
  SupportTransform = false
  Suppressed = false
  UseAllEdges = false
  expr: Radius = <<parameters>>.bumper_bolt_diameter
FEATURE [PartDesign::Body] Body014  label="BumperBody"
  AllowCompound = false
  Group = -> [Sketch053,Pad029,Sketch054,Pad030,Sketch055,Pad031,Sketch056,Pocket025,Sketch057,Pocket026,Fillet024,Fillet025,Fillet026]
  Origin = -> Origin029
  Tip = -> Fillet026
FEATURE [App::Part] Part014  label="Bumper"
  Group = -> [Body014]
  Origin = -> Origin028
FEATURE [Sketcher::SketchObject] Sketch058  label="USBCCouplerHullSketch"
  ArcFitTolerance = 0
  AttachmentSupport = -> [XZ_Plane031]
  FullyConstrained = true
  MakeInternals = false
  MapMode = 5
  Placement = pos=(0,0,0) rot=(1,0,0;1.5708rad)
  sketch-geometry (4):
    g0: LineSegment StartX=0 StartY=13 StartZ=0 EndX=20.4 EndY=13 EndZ=0
    g1: LineSegment StartX=20.4 StartY=13 StartZ=0 EndX=20.4 EndY=0 EndZ=0
    g2: LineSegment StartX=20.4 StartY=0 StartZ=0 EndX=0 EndY=0 EndZ=0
    g3: LineSegment StartX=0 StartY=0 StartZ=0 EndX=0 EndY=13 EndZ=0
  constraints (11):
    c: Coincident(g0,g1)
    c: Coincident(g1,g2)
    c: Coincident(g2,g3)
    c: Coincident(g3,g0)
    c: Horizontal(g0)
    c: Horizontal(g2)
    c: Vertical(g1)
    c: Vertical(g3)
    c: DistanceX(g0,g0) = 20.4
    c: Coincident(g2,g-1)
    c: DistanceY(g2,g0) = 13
FEATURE [PartDesign::Pad] Pad032  label="USBCCouplerHull"
  Direction = (0,-1,2e-16)
  Length = 12.5
  Length2 = 10
  Placement = pos=(0,0,0) rot=(1,0,0;1.5708rad)
  Profile = -> Sketch058
  ReferenceAxis = -> Sketch058 [N_Axis]
  Suppressed = false
  Type = 0
FEATURE [Sketcher::SketchObject] Sketch059  label="USBCCouplerASketch"
  ArcFitTolerance = 0
  AttachmentSupport = -> [Pad032]
  FullyConstrained = true
  MakeInternals = false
  MapMode = 5
  Placement = pos=(0,-12.5,0) rot=(1,0,0;1.5708rad)
  sketch-geometry (4):
    g0: LineSegment StartX=3.2 StartY=9.8 StartZ=0 EndX=17.2 EndY=9.8 EndZ=0
    g1: LineSegment StartX=17.2 StartY=9.8 StartZ=0 EndX=17.2 EndY=3.2 EndZ=0
    g2: LineSegment StartX=17.2 StartY=3.2 StartZ=0 EndX=3.2 EndY=3.2 EndZ=0
    g3: LineSegment StartX=3.2 StartY=3.2 StartZ=0 EndX=3.2 EndY=9.8 EndZ=0
  constraints (12):
    c: Coincident(g0,g1)
    c: Coincident(g1,g2)
    c: Coincident(g2,g3)
    c: Coincident(g3,g0)
    c: Horizontal(g0)
    c: Horizontal(g2)
    c: Vertical(g1)
    c: Vertical(g3)
    c: DistanceX(g0,g0) = 14
    c: DistanceY(g1,g0) = 6.6
    c: DistanceX(g-1,g2) = 3.2
    c: DistanceY(g-1,g2) = 3.2
FEATURE [PartDesign::Pocket] Pocket027  label="USBCCouplerA"
  BaseFeature = -> Pad032
  Direction = (0,1,-2e-16)
  Length = 7.5
  Length2 = 5
  Placement = pos=(0,0,0) rot=(1,0,0;1.5708rad)
  Profile = -> Sketch059
  ReferenceAxis = -> Sketch059 [N_Axis]
  Suppressed = false
  Type = 0
FEATURE [Sketcher::SketchObject] Sketch060  label="USBCCouplerCSketch"
  ArcFitTolerance = 0
  AttachmentSupport = -> [Pocket027]
  FullyConstrained = true
  MakeInternals = false
  MapMode = 5
  Placement = pos=(0,1.4e-15,0) rot=(-1,0,0;1.5708rad)
  expr: Constraints[11] = 3.2 + (6.6 - 6.5) / 2
  expr: Constraints[8] = 3.2 + (14 - 12.3) / 2
  sketch-geometry (4):
    g0: LineSegment StartX=4.05 StartY=-3.25 StartZ=0 EndX=16.35 EndY=-3.25 EndZ=0
    g1: LineSegment StartX=16.35 StartY=-3.25 StartZ=0 EndX=16.35 EndY=-9.75 EndZ=0
    g2: LineSegment StartX=16.35 StartY=-9.75 StartZ=0 EndX=4.05 EndY=-9.75 EndZ=0
    g3: LineSegment StartX=4.05 StartY=-9.75 StartZ=0 EndX=4.05 EndY=-3.25 EndZ=0
  constraints (12):
    c: Coincident(g0,g1)
    c: Coincident(g1,g2)
    c: Coincident(g2,g3)
    c: Coincident(g3,g0)
    c: Horizontal(g0)
    c: Horizontal(g2)
    c: Vertical(g1)
    c: Vertical(g3)
    c: DistanceX(g-1,g0) = 4.05
    c: DistanceX(g0,g0) = 12.3
    c: DistanceY(g1,g0) = 6.5
    c: DistanceY(g0,g-1) = 3.25
FEATURE [PartDesign::Pocket] Pocket028  label="USBCCouplerC"
  BaseFeature = -> Pocket027
  Direction = (0,-1,-2e-16)
  Length = 5
  Length2 = 5
  Placement = pos=(0,0,0) rot=(1,0,0;1.5708rad)
  Profile = -> Sketch060
  ReferenceAxis = -> Sketch060 [N_Axis]
  Suppressed = false
  Type = 0
FEATURE [PartDesign::Fillet] Fillet027  label="USBCCouplerMatingRounding"
  Base = -> Pocket028 [Edge24,Edge21,Edge22,Edge26,Edge30,Edge32,Edge34,Edge29]
  BaseFeature = -> Pocket028
  Placement = pos=(0,0,0) rot=(1,0,0;1.5708rad)
  Radius = 1
  SupportTransform = false
  Suppressed = false
  UseAllEdges = false
FEATURE [PartDesign::Fillet] Fillet028  label="USBCCouplerRounding"
  Base = -> Fillet027 [Edge29,Edge32,Edge30,Edge34]
  BaseFeature = -> Fillet027
  Placement = pos=(0,0,0) rot=(1,0,0;1.5708rad)
  Radius = 3.2
  SupportTransform = false
  Suppressed = false
  UseAllEdges = false
FEATURE [PartDesign::Body] Body015  label="USBCCouplerBody"
  AllowCompound = false
  Group = -> [Sketch058,Pad032,Sketch059,Pocket027,Sketch060,Pocket028,Fillet027,Fillet028]
  Origin = -> Origin031
  Tip = -> Fillet028
FEATURE [App::Part] Part015  label="USBCCoupler"
  Group = -> [Body015]
  Origin = -> Origin030
FEATURE [Part::Feature] Part__Feature  label="E4T-X-197-D-H-M-X"
  Placement = pos=(0,1.1e-15,5) rot=(1,0,0;1.5708rad)
  shape: bbox 23.63 x 24.86 x 13.62 mm, 678 faces, 7 solids (baked)
FEATURE [App::Part] Part002  label="TransmissionCover"
  Group = -> [Body002,Part__Feature]
  Origin = -> Origin004
